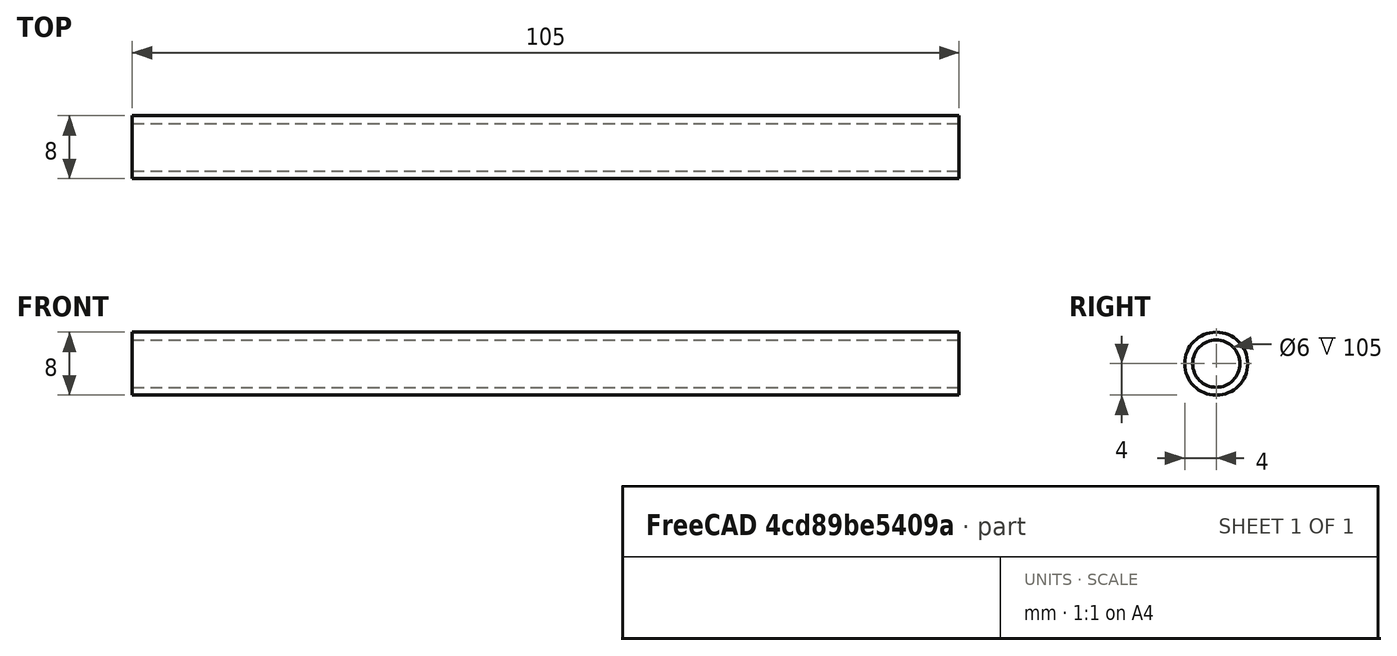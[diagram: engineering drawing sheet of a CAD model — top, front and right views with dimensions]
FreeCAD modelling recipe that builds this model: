
FCSTD DOCUMENT  (FreeCAD 0.19R24344 (Git))
Label: Inexpensive-Treadmill_Assembly
License: All rights reserved
LicenseURL: http://en.wikipedia.org/wiki/All_rights_reserved
objects: App::Link×22, App::DocumentObjectGroup×2, PartDesign::CoordinateSystem×1, App::FeaturePython×1, Part::FeaturePython×1, App::Part×1
note: 2 computed .brp shape members not serialized (recipe doc carries the construction recipe); baked Part::Feature solids carry a one-line shape summary decoded from their .brp
EXTERNAL_REF file=../../Miscellaneous/Baseplate/Baseplate.FCStd obj=Body
EXTERNAL_REF file=../../Miscellaneous/Baseplate/Baseplate.FCStd obj=LCS_Camera_Stand
EXTERNAL_REF file=../Stand_Camera-Case/Stand_Camera-Case.FCStd obj=LCS_Baseplate_Right
EXTERNAL_REF file=../Stand_Camera-Case/Stand_Camera-Case.FCStd obj=Body
EXTERNAL_REF file=../../Miscellaneous/PS-Eye/PS-Eye.FCStd obj=LCS_Camera_Base
EXTERNAL_REF file=../Stand_Camera-Case/Stand_Camera-Case.FCStd obj=LCS_Top_Mount
EXTERNAL_REF file=../../Miscellaneous/PS-Eye/PS-Eye.FCStd obj=Part
EXTERNAL_REF file=../../Miscellaneous/Baseplate/Baseplate.FCStd obj=LCS_Table_Foot1
EXTERNAL_REF file=../Stand_Treadmill_Sphere_Holder/Stand_Treadmill_Sphere_Holder.FCStd obj=LCS_Foot_Base
EXTERNAL_REF file=../Stand_Treadmill_Sphere_Holder/Stand_Treadmill_Sphere_Holder.FCStd obj=Body001
EXTERNAL_REF file=../Stand_Treadmill_Sphere_Holder/Stand_Treadmill_Sphere_Holder.FCStd obj=LCS_Base
EXTERNAL_REF file=../Stand_Treadmill_Sphere_Holder/Stand_Treadmill_Sphere_Holder.FCStd obj=LCS_Top001
EXTERNAL_REF file=../Stand_Treadmill_Sphere_Holder/Stand_Treadmill_Sphere_Holder.FCStd obj=Body
EXTERNAL_REF file=../Stand_Treadmill_Sphere_Holder/Stand_Treadmill_Sphere_Holder.FCStd obj=LCS_Top
EXTERNAL_REF file=../Treadmill_Sphere_Holder/Treadmill_Sphere_Holder.FCStd obj=LCS_Bottom
EXTERNAL_REF file=../Treadmill_Sphere_Holder/Treadmill_Sphere_Holder.FCStd obj=Treadmill_Sphere_Holder
EXTERNAL_REF file=../../Miscellaneous/Baseplate/Baseplate.FCStd obj=LCS_Foot2
EXTERNAL_REF file=../../Miscellaneous/Baseplate/Baseplate.FCStd obj=LCS_Foot3
EXTERNAL_REF file=../../Miscellaneous/Baseplate/Baseplate.FCStd obj=LCS_Foot4
EXTERNAL_REF file=../../Miscellaneous/Baseplate/Baseplate.FCStd obj=LCS_Light1
EXTERNAL_REF file=../Lamp_LED_5mm/Lamp_post_60.FCStd obj=LCS_Base
EXTERNAL_REF file=../Lamp_LED_5mm/Lamp_post_60.FCStd obj=LampPost
EXTERNAL_REF file=../../Miscellaneous/Baseplate/Baseplate.FCStd obj=LCS_Light3
EXTERNAL_REF file=../Lamp_LED_5mm/Lamp_post_40.FCStd obj=LCS_Base
EXTERNAL_REF file=../Lamp_LED_5mm/Lamp_post_40.FCStd obj=LampPost
EXTERNAL_REF file=../../Miscellaneous/Baseplate/Baseplate.FCStd obj=LCS_Light2
EXTERNAL_REF file=../Lamp_LED_5mm/Lamp_post.FCStd obj=LCS_Base
EXTERNAL_REF file=../Lamp_LED_5mm/Lamp_post.FCStd obj=LampPost
EXTERNAL_REF file=../Lamp_LED_5mm/Lamp_post_60.FCStd obj=LCS_Shade
EXTERNAL_REF file=../Lamp_LED_5mm/Lamp_shade.FCStd obj=LCS_Shade
EXTERNAL_REF file=../Lamp_LED_5mm/Lamp_shade.FCStd obj=Body
EXTERNAL_REF file=../Lamp_LED_5mm/Lamp_post_40.FCStd obj=LCS_Shade
EXTERNAL_REF file=../Lamp_LED_5mm/Lamp_post.FCStd obj=LCS_Shade
EXTERNAL_REF file=../../Miscellaneous/Baseplate/Baseplate.FCStd obj=LCS_Tablet001
EXTERNAL_REF file=../../Miscellaneous/Holder_Tablet/Holder_Tablet.FCStd obj=LCS_Base
EXTERNAL_REF file=../../Miscellaneous/Holder_Tablet/Holder_Tablet.FCStd obj=Body
EXTERNAL_REF file=../../Miscellaneous/Tablet/FireTablet.FCStd obj=LCS_Tablet_Back
EXTERNAL_REF file=../../Miscellaneous/Holder_Tablet/Holder_Tablet.FCStd obj=LCS_Tablet
EXTERNAL_REF file=../../Miscellaneous/Tablet/FireTablet.FCStd obj=Fire7
EXTERNAL_REF file=../../Miscellaneous/Baseplate/Baseplate.FCStd obj=LCS_Micro
EXTERNAL_REF file=../Stand_MicroManipulator/Stand_MicroManipulator.FCStd obj=LCS_Base
EXTERNAL_REF file=../Stand_MicroManipulator/Stand_MicroManipulator.FCStd obj=Body
EXTERNAL_REF file=../../Tethering/MicroManipulator/MicroManipulator_Assembly.FCStd obj=LCS_Origin
EXTERNAL_REF file=../Stand_MicroManipulator/Stand_MicroManipulator.FCStd obj=LCS_Top
EXTERNAL_REF file=../../Tethering/MicroManipulator/MicroManipulator_Assembly.FCStd obj=Model
EXTERNAL_REF file=../../Miscellaneous/Baseplate/Baseplate.FCStd obj=LCS_Heat
EXTERNAL_REF file=../../Miscellaneous/Baseplate/Heating-Base.FCStd obj=LCS_Base
EXTERNAL_REF file=../../Miscellaneous/Baseplate/Heating-Base.FCStd obj=Body
EXTERNAL_REF file=../../Miscellaneous/Spheres/Sphere-9mm-plain.FCStd obj=LCS_Sphere
EXTERNAL_REF file=../Treadmill_Sphere_Holder/Treadmill_Sphere_Holder.FCStd obj=LCS_Ball
EXTERNAL_REF file=../../Miscellaneous/Spheres/Sphere-9mm-plain.FCStd obj=Sphere001
EXTERNAL_REF file=../../Miscellaneous/Scale-Bar/Scale-Bar.FCStd obj=LCS_0
EXTERNAL_REF file=../../Miscellaneous/Scale-Bar/Scale-Bar.FCStd obj=Scalebar

FEATURE [App::DocumentObjectGroup] Parts
FEATURE [PartDesign::CoordinateSystem] LCS_Origin
  AttacherType = Attacher::AttachEngine3D
  MapMode = 2
  Support = -> [X_Axis]
FEATURE [App::DocumentObjectGroup] Constraints
FEATURE [App::FeaturePython] Variables  # WARN: FeaturePython — macro-defined, semantics opaque (R4)
FEATURE [App::Link] Baseplate_Baseplate
  LinkedObject = -> <external ../../Miscellaneous/Baseplate/Baseplate.FCStd>#Body
FEATURE [App::Link] Stand_Camera_Case_Stand_Camera
  AssemblyType = Asm4EE
  AttachedBy = #LCS_Baseplate_Right
  AttachedTo = Baseplate_Baseplate#LCS_Camera_Stand
  LinkPlacement = pos=(-80.3633,0.000175563,29) rot=(0,0,-1;1.57078rad)
  LinkedObject = -> <external ../Stand_Camera-Case/Stand_Camera-Case.FCStd>#Body
  Placement = pos=(-80.3633,0.000175563,29) rot=(0,0,-1;1.57078rad)
  expr: Placement = Baseplate_Baseplate.Placement * Baseplate#LCS_Camera_Stand.Placement * AttachmentOffset * Stand_Camera_Case#LCS_Baseplate_Right.Placement ^ -1
FEATURE [App::Link] PS_Eye_PSEye
  AssemblyType = Asm4EE
  AttachedBy = #LCS_Camera_Base
  AttachedTo = Stand_Camera_Case_Stand_Camera#LCS_Top_Mount
  AttachmentOffset = pos=(0,0,0) rot=(0,0,1;4.71239rad)
  LinkPlacement = pos=(-82.4061,2.32459,50) rot=(-0.577358,0.577346,0.577346;4.1888rad)
  LinkedObject = -> <external ../../Miscellaneous/PS-Eye/PS-Eye.FCStd>#Part
  Placement = pos=(-82.4061,2.32459,50) rot=(-0.577358,0.577346,0.577346;4.1888rad)
  expr: Placement = Stand_Camera_Case_Stand_Camera.Placement * Stand_Camera_Case#LCS_Top_Mount.Placement * AttachmentOffset * PS_Eye#LCS_Camera_Base.Placement ^ -1
FEATURE [App::Link] Stand_Treadmill_Sphere_Holder_Stand_Foot
  AssemblyType = Asm4EE
  AttachedBy = #LCS_Foot_Base
  AttachedTo = Baseplate_Baseplate#LCS_Table_Foot1
  AttachmentOffset = pos=(0,0,0) rot=(0,0,1;4.71239rad)
  LinkPlacement = pos=(38.0043,-0.0918805,46.2) rot=(0,0,1;3.14256rad)
  LinkedObject = -> <external ../Stand_Treadmill_Sphere_Holder/Stand_Treadmill_Sphere_Holder.FCStd>#Body001
  Placement = pos=(38.0043,-0.0918805,46.2) rot=(0,0,1;3.14256rad)
  expr: Placement = Baseplate_Baseplate.Placement * Baseplate#LCS_Table_Foot1.Placement * AttachmentOffset * Stand_Treadmill_Sphere_Holder#LCS_Foot_Base.Placement ^ -1
FEATURE [App::Link] Stand_Treadmill_Sphere_Holder_Stand
  AssemblyType = Asm4EE
  AttachedBy = #LCS_Base
  AttachedTo = Stand_Treadmill_Sphere_Holder_Stand_Foot#LCS_Top001
  AttachmentOffset = pos=(0,0,0) rot=(0,0,1;1.5708rad)
  LinkPlacement = pos=(38.0046,-0.0921835,43.2) rot=(0,0,1;4.71335rad)
  LinkedObject = -> <external ../Stand_Treadmill_Sphere_Holder/Stand_Treadmill_Sphere_Holder.FCStd>#Body
  Placement = pos=(38.0046,-0.0921835,43.2) rot=(0,0,1;4.71335rad)
  expr: Placement = Stand_Treadmill_Sphere_Holder_Stand_Foot.Placement * Stand_Treadmill_Sphere_Holder#LCS_Top001.Placement * AttachmentOffset * Stand_Treadmill_Sphere_Holder#LCS_Base.Placement ^ -1
FEATURE [App::Link] Treadmill_Sphere_Holder_Treadmill_Sphere_Holder
  AssemblyType = Asm4EE
  AttachedBy = #LCS_Bottom
  AttachedTo = Stand_Treadmill_Sphere_Holder_Stand#LCS_Top
  LinkPlacement = pos=(38.0046,-0.0921842,82.125) rot=(-1,-0.000479,-0.000479;4.71239rad)
  LinkedObject = -> <external ../Treadmill_Sphere_Holder/Treadmill_Sphere_Holder.FCStd>#Treadmill_Sphere_Holder
  Placement = pos=(38.0046,-0.0921842,82.125) rot=(-1,-0.000479,-0.000479;4.71239rad)
  expr: Placement = Stand_Treadmill_Sphere_Holder_Stand.Placement * Stand_Treadmill_Sphere_Holder#LCS_Top.Placement * AttachmentOffset * Treadmill_Sphere_Holder#LCS_Bottom.Placement ^ -1
FEATURE [App::Link] Stand_Treadmill_Sphere_Holder_Stand_Foot001
  AssemblyType = Asm4EE
  AttachedBy = #LCS_Foot_Base
  AttachedTo = Baseplate_Baseplate#LCS_Foot2
  AttachmentOffset = pos=(0,0,0) rot=(0,0,1;1.5708rad)
  LinkPlacement = pos=(38.0082,0.0956894,46.2) rot=(0,0,1;1.57177rad)
  LinkedObject = -> <external ../Stand_Treadmill_Sphere_Holder/Stand_Treadmill_Sphere_Holder.FCStd>#Body001
  Placement = pos=(38.0082,0.0956894,46.2) rot=(0,0,1;1.57177rad)
  expr: Placement = Baseplate_Baseplate.Placement * Baseplate#LCS_Foot2.Placement * AttachmentOffset * Stand_Treadmill_Sphere_Holder#LCS_Foot_Base.Placement ^ -1
FEATURE [App::Link] Stand_Treadmill_Sphere_Holder_Stand_Foot002
  AssemblyType = Asm4EE
  AttachedBy = #LCS_Foot_Base
  AttachedTo = Baseplate_Baseplate#LCS_Foot3
  LinkPlacement = pos=(38.1957,0.091848,46.2) rot=(0,0,1;0.00097rad)
  LinkedObject = -> <external ../Stand_Treadmill_Sphere_Holder/Stand_Treadmill_Sphere_Holder.FCStd>#Body001
  Placement = pos=(38.1957,0.091848,46.2) rot=(0,0,1;0.00097rad)
  expr: Placement = Baseplate_Baseplate.Placement * Baseplate#LCS_Foot3.Placement * AttachmentOffset * Stand_Treadmill_Sphere_Holder#LCS_Foot_Base.Placement ^ -1
FEATURE [App::Link] Stand_Treadmill_Sphere_Holder_Stand_Foot003
  AssemblyType = Asm4EE
  AttachedBy = #LCS_Foot_Base
  AttachedTo = Baseplate_Baseplate#LCS_Foot4
  AttachmentOffset = pos=(0,0,0) rot=(0,0,1;4.71239rad)
  LinkPlacement = pos=(38.1918,-0.0956894,46.2) rot=(0,0,1;4.71336rad)
  LinkedObject = -> <external ../Stand_Treadmill_Sphere_Holder/Stand_Treadmill_Sphere_Holder.FCStd>#Body001
  Placement = pos=(38.1918,-0.0956894,46.2) rot=(0,0,1;4.71336rad)
  expr: Placement = Baseplate_Baseplate.Placement * Baseplate#LCS_Foot4.Placement * AttachmentOffset * Stand_Treadmill_Sphere_Holder#LCS_Foot_Base.Placement ^ -1
FEATURE [App::Link] Lamp_post_lamp_post_60
  AssemblyType = Asm4EE
  AttachedBy = #LCS_Base
  AttachedTo = Baseplate_Baseplate#LCS_Light1
  AttachmentOffset = pos=(0,0,0) rot=(0,0,1;0.349066rad)
  LinkPlacement = pos=(-41.0097,-26.459,10) rot=(0,0,1;1.91986rad)
  LinkedObject = -> <external ../Lamp_LED_5mm/Lamp_post_60.FCStd>#LampPost
  Placement = pos=(-41.0097,-26.459,10) rot=(0,0,1;1.91986rad)
  expr: Placement = Baseplate_Baseplate.Placement * Baseplate#LCS_Light1.Placement * AttachmentOffset * Lamp_post_60#LCS_Base.Placement ^ -1
FEATURE [App::Link] Lamp_post_40_lamp_post_40
  AssemblyType = Asm4EE
  AttachedBy = #LCS_Base
  AttachedTo = Baseplate_Baseplate#LCS_Light3
  AttachmentOffset = pos=(0,0,0) rot=(0,0,1;5.44543rad)
  LinkPlacement = pos=(-14.7719,53.1011,10) rot=(0,0,-1;5.55015rad)
  LinkedObject = -> <external ../Lamp_LED_5mm/Lamp_post_40.FCStd>#LampPost
  Placement = pos=(-14.7719,53.1011,10) rot=(0,0,-1;5.55015rad)
  expr: Placement = Baseplate_Baseplate.Placement * Baseplate#LCS_Light3.Placement * AttachmentOffset * Lamp_post_40#LCS_Base.Placement ^ -1
FEATURE [App::Link] Lamp_post_lamp_post
  AssemblyType = Asm4EE
  AttachedBy = #LCS_Base
  AttachedTo = Baseplate_Baseplate#LCS_Light2
  AttachmentOffset = pos=(0,0,0) rot=(0,0,1;-0.349066rad)
  LinkPlacement = pos=(-41.0097,26.459,10) rot=(0,0,-1;5.06145rad)
  LinkedObject = -> <external ../Lamp_LED_5mm/Lamp_post.FCStd>#LampPost
  Placement = pos=(-41.0097,26.459,10) rot=(0,0,-1;5.06145rad)
  expr: Placement = Baseplate_Baseplate.Placement * Baseplate#LCS_Light2.Placement * AttachmentOffset * Lamp_post#LCS_Base.Placement ^ -1
FEATURE [App::Link] Lamp_shade_lamp_shade
  AssemblyType = Asm4EE
  AttachedBy = #LCS_Shade
  AttachedTo = Lamp_post_lamp_post_60#LCS_Shade
  AttachmentOffset = pos=(0,0,0) rot=(0.707107,-0.707107,0;3.14159rad)
  LinkPlacement = pos=(-33.7179,-23.805,70.5) rot=(0.443713,0.633687,0.633687;2.30637rad)
  LinkedObject = -> <external ../Lamp_LED_5mm/Lamp_shade.FCStd>#Body
  Placement = pos=(-33.7179,-23.805,70.5) rot=(0.443713,0.633687,0.633687;2.30637rad)
  expr: Placement = Lamp_post_lamp_post_60.Placement * Lamp_post_60#LCS_Shade.Placement * AttachmentOffset * Lamp_shade#LCS_Shade.Placement ^ -1
FEATURE [App::Link] Lamp_shade_lamp_shade001
  AssemblyType = Asm4EE
  AttachedBy = #LCS_Shade
  AttachedTo = Lamp_post_40_lamp_post_40#LCS_Shade
  AttachmentOffset = pos=(0,0,0) rot=(0,0,1;2.32129rad)
  LinkPlacement = pos=(-9.4181,47.1551,52.8953) rot=(0.819087,0.314418,0.47983;1.34948rad)
  LinkedObject = -> <external ../Lamp_LED_5mm/Lamp_shade.FCStd>#Body
  Placement = pos=(-9.4181,47.1551,52.8953) rot=(0.819087,0.314418,0.47983;1.34948rad)
  expr: Placement = Lamp_post_40_lamp_post_40.Placement * Lamp_post_40#LCS_Shade.Placement * AttachmentOffset * Lamp_shade#LCS_Shade.Placement ^ -1
FEATURE [App::Link] Lamp_shade_lamp_shade002
  AssemblyType = Asm4EE
  AttachedBy = #LCS_Shade
  AttachedTo = Lamp_post_lamp_post#LCS_Shade
  AttachmentOffset = pos=(0,0,0) rot=(0,0,1;2.9147rad)
  LinkPlacement = pos=(-33.1668,23.6045,89.1503) rot=(0.745251,0.52183,0.415083;2.07138rad)
  LinkedObject = -> <external ../Lamp_LED_5mm/Lamp_shade.FCStd>#Body
  Placement = pos=(-33.1668,23.6045,89.1503) rot=(0.745251,0.52183,0.415083;2.07138rad)
  expr: Placement = Lamp_post_lamp_post.Placement * Lamp_post#LCS_Shade.Placement * AttachmentOffset * Lamp_shade#LCS_Shade.Placement ^ -1
FEATURE [App::Link] Holder_Tablet_FireHolder
  AssemblyType = Asm4EE
  AttachedBy = #LCS_Base
  AttachedTo = Baseplate_Baseplate#LCS_Tablet001
  AttachmentOffset = pos=(-12.7,40,0) rot=(0,0,1;4.71239rad)
  LinkPlacement = pos=(85.5,50,37) rot=(0,0,1;0rad)
  LinkedObject = -> <external ../../Miscellaneous/Holder_Tablet/Holder_Tablet.FCStd>#Body
  Placement = pos=(85.5,50,37) rot=(0,0,1;0rad)
  expr: Placement = Baseplate_Baseplate.Placement * Baseplate#LCS_Tablet001.Placement * AttachmentOffset * Holder_Tablet#LCS_Base.Placement ^ -1
FEATURE [App::Link] FireTablet_Fire7
  AssemblyType = Asm4EE
  AttachedBy = #LCS_Tablet_Back
  AttachedTo = Holder_Tablet_FireHolder#LCS_Tablet
  AttachmentOffset = pos=(12.7,-5,0) rot=(0.707107,0.707107,0;3.14159rad)
  LinkPlacement = pos=(78.5,12.7,89.518) rot=(0.57735,-0.57735,-0.57735;2.0944rad)
  LinkedObject = -> <external ../../Miscellaneous/Tablet/FireTablet.FCStd>#Fire7
  Placement = pos=(78.5,12.7,89.518) rot=(0.57735,-0.57735,-0.57735;2.0944rad)
  expr: Placement = Holder_Tablet_FireHolder.Placement * Holder_Tablet#LCS_Tablet.Placement * AttachmentOffset * FireTablet#LCS_Tablet_Back.Placement ^ -1
FEATURE [App::Link] Stand_MicroManipulator_Stand
  AssemblyType = Asm4EE
  AttachedBy = #LCS_Base
  AttachedTo = Baseplate_Baseplate#LCS_Micro
  AttachmentOffset = pos=(25.4,0,0) rot=(0,0,1;3.14159rad)
  LinkPlacement = pos=(-2.66e-14,-63.5,8) rot=(0,0,1;3.14159rad)
  LinkedObject = -> <external ../Stand_MicroManipulator/Stand_MicroManipulator.FCStd>#Body
  Placement = pos=(-2.66e-14,-63.5,8) rot=(0,0,1;3.14159rad)
  expr: Placement = Baseplate_Baseplate.Placement * Baseplate#LCS_Micro.Placement * AttachmentOffset * Stand_MicroManipulator#LCS_Base.Placement ^ -1
FEATURE [App::Link] MicroManipulator_Assembly
  AssemblyType = Asm4EE
  AttachedBy = #LCS_Origin
  AttachedTo = Stand_MicroManipulator_Stand#LCS_Top
  AttachmentOffset = pos=(0,0,0) rot=(0,0,1;3.14159rad)
  LinkPlacement = pos=(12.7,-50.8,58) rot=(0,0,-1;4.71239rad)
  LinkedObject = -> <external ../../Tethering/MicroManipulator/MicroManipulator_Assembly.FCStd>#Model
  Placement = pos=(12.7,-50.8,58) rot=(0,0,-1;4.71239rad)
  expr: Placement = Stand_MicroManipulator_Stand.Placement * Stand_MicroManipulator#LCS_Top.Placement * AttachmentOffset * MicroManipulator_Assembly#LCS_Origin.Placement ^ -1
FEATURE [App::Link] Heating_Base_Heat_pad
  AssemblyType = Asm4EE
  AttachedBy = #LCS_Base
  AttachedTo = Baseplate_Baseplate#LCS_Heat
  LinkPlacement = pos=(38.1,7.1e-15,33) rot=(0,0,1;1.5708rad)
  LinkedObject = -> <external ../../Miscellaneous/Baseplate/Heating-Base.FCStd>#Body
  Placement = pos=(38.1,7.1e-15,33) rot=(0,0,1;1.5708rad)
  expr: Placement = Baseplate_Baseplate.Placement * Baseplate#LCS_Heat.Placement * AttachmentOffset * Heating_Base#LCS_Base.Placement ^ -1
FEATURE [App::Link] Sphere_9mm_plain_Sphere001
  AssemblyType = Asm4EE
  AttachedBy = #LCS_Sphere
  AttachedTo = Treadmill_Sphere_Holder_Treadmill_Sphere_Holder#LCS_Ball
  LinkPlacement = pos=(38.0046,-0.0921842,82.1448) rot=(0,0,-1;3.14063rad)
  LinkedObject = -> <external ../../Miscellaneous/Spheres/Sphere-9mm-plain.FCStd>#Sphere001
  Placement = pos=(38.0046,-0.0921842,82.1448) rot=(0,0,-1;3.14063rad)
  expr: Placement = Treadmill_Sphere_Holder_Treadmill_Sphere_Holder.Placement * Treadmill_Sphere_Holder#LCS_Ball.Placement * AttachmentOffset * Sphere_9mm_plain#LCS_Sphere.Placement ^ -1
FEATURE [Part::FeaturePython] Tube  # WARN: FeaturePython — macro-defined, semantics opaque (R4)
  AttacherType = Attacher::AttachEngine3D
  Height = 105
  InnerRadius = 3
  OuterRadius = 4
  Placement = pos=(-67,-1,54) rot=(0,1,0;1.5708rad)
FEATURE [App::Link] Scale_Bar_Scalebar
  AssemblyType = Asm4EE
  AttachedBy = #LCS_0
  AttachedTo = Parent Assembly#LCS_Origin
  AttachmentOffset = pos=(-55,-185,0) rot=(-0.57735,0.57735,0.57735;4.18879rad)
  LinkPlacement = pos=(-55,-185,0) rot=(-0.57735,0.57735,0.57735;4.18879rad)
  LinkedObject = -> <external ../../Miscellaneous/Scale-Bar/Scale-Bar.FCStd>#Scalebar
  Placement = pos=(-55,-185,0) rot=(-0.57735,0.57735,0.57735;4.18879rad)
  expr: Placement = LCS_Origin.Placement * AttachmentOffset * Scale_Bar#LCS_0.Placement ^ -1
FEATURE [App::Part] Model
  Configuration = 0
  Group = -> [LCS_Origin,Constraints,Variables,Baseplate_Baseplate,Stand_Camera_Case_Stand_Camera,PS_Eye_PSEye,Stand_Treadmill_Sphere_Holder_Stand_Foot,Stand_Treadmill_Sphere_Holder_Stand,Treadmill_Sphere_Holder_Treadmill_Sphere_Holder,Stand_Treadmill_Sphere_Holder_Stand_Foot001,Stand_Treadmill_Sphere_Holder_Stand_Foot002,Stand_Treadmill_Sphere_Holder_Stand_Foot003,Lamp_post_lamp_post_60,+12 more]
  Origin = -> Origin
  Type = Assembly4 Model

RESOLVED EXTERNAL PARTS (link-assembly join: the EXTERNAL_REF files above that resolve inside this repo's crawl, each included once):
---- part ../../Miscellaneous/Baseplate/Baseplate.FCStd = doc fcstd_f7cd438ebf0e ----
FCSTD DOCUMENT  (FreeCAD 0.19R24344 (Git))
Label: Baseplate
License: All rights reserved
LicenseURL: http://en.wikipedia.org/wiki/All_rights_reserved
objects: PartDesign::CoordinateSystem×13, Sketcher::SketchObject×1, PartDesign::Pad×1, PartDesign::Body×1
note: 17 computed .brp shape members not serialized (recipe doc carries the construction recipe); baked Part::Feature solids carry a one-line shape summary decoded from their .brp

FEATURE [Sketcher::SketchObject] Sketch
  FullyConstrained = true
  MapMode = 5
  Support = -> [XY_Plane]
  sketch-geometry (140):
    g0: LineSegment StartX=-139.7 StartY=139.7 StartZ=0 EndX=139.7 EndY=139.7 EndZ=0
    g1: LineSegment StartX=152.4 StartY=127 StartZ=0 EndX=152.4 EndY=-127 EndZ=0
    g2: LineSegment StartX=139.7 StartY=-139.7 StartZ=0 EndX=-139.7 EndY=-139.7 EndZ=0
    g3: LineSegment StartX=-152.4 StartY=-127 StartZ=0 EndX=-152.4 EndY=127 EndZ=0
    g4: ArcOfCircle CenterX=-139.7 CenterY=127 CenterZ=0 NormalX=0 NormalY=0 NormalZ=1 AngleXU=0 Radius=12.7 StartAngle=1.5708 EndAngle=3.14159
    g5: ArcOfCircle CenterX=-139.7 CenterY=-127 CenterZ=0 NormalX=0 NormalY=0 NormalZ=1 AngleXU=0 Radius=12.7 StartAngle=3.14159 EndAngle=4.71239
    g6: ArcOfCircle CenterX=139.7 CenterY=-127 CenterZ=0 NormalX=0 NormalY=0 NormalZ=1 AngleXU=0 Radius=12.7 StartAngle=4.71239 EndAngle=6.28319
    g7: ArcOfCircle CenterX=139.7 CenterY=127 CenterZ=0 NormalX=0 NormalY=0 NormalZ=1 AngleXU=0 Radius=12.7 StartAngle=2e-16 EndAngle=1.5708
    g8: Circle CenterX=-139.7 CenterY=127 CenterZ=0 NormalX=0 NormalY=0 NormalZ=1 AngleXU=0 Radius=3.175
    g9: Circle CenterX=-114.3 CenterY=127 CenterZ=0 NormalX=0 NormalY=0 NormalZ=1 AngleXU=0 Radius=3.175
    g10: Circle CenterX=-88.9 CenterY=127 CenterZ=0 NormalX=0 NormalY=0 NormalZ=1 AngleXU=0 Radius=3.175
    g11: Circle CenterX=-63.5 CenterY=127 CenterZ=0 NormalX=0 NormalY=0 NormalZ=1 AngleXU=0 Radius=3.175
    g12: Circle CenterX=-38.1 CenterY=127 CenterZ=0 NormalX=0 NormalY=0 NormalZ=1 AngleXU=0 Radius=3.175
    g13: Circle CenterX=-12.7 CenterY=127 CenterZ=0 NormalX=0 NormalY=0 NormalZ=1 AngleXU=0 Radius=3.175
    g14: Circle CenterX=12.7 CenterY=127 CenterZ=0 NormalX=0 NormalY=0 NormalZ=1 AngleXU=0 Radius=3.175
    g15: Circle CenterX=38.1 CenterY=127 CenterZ=0 NormalX=0 NormalY=0 NormalZ=1 AngleXU=0 Radius=3.175
    g16: Circle CenterX=63.5 CenterY=127 CenterZ=0 NormalX=0 NormalY=0 NormalZ=1 AngleXU=0 Radius=3.175
    g17: Circle CenterX=88.9 CenterY=127 CenterZ=0 NormalX=0 NormalY=0 NormalZ=1 AngleXU=0 Radius=3.175
    g18: Circle CenterX=114.3 CenterY=127 CenterZ=0 NormalX=0 NormalY=0 NormalZ=1 AngleXU=0 Radius=3.175
    g19: Circle CenterX=139.7 CenterY=127 CenterZ=0 NormalX=0 NormalY=0 NormalZ=1 AngleXU=0 Radius=3.175
    g20: Circle CenterX=-139.7 CenterY=101.6 CenterZ=0 NormalX=0 NormalY=0 NormalZ=1 AngleXU=0 Radius=3.175
    g21: Circle CenterX=-114.3 CenterY=101.6 CenterZ=0 NormalX=0 NormalY=0 NormalZ=1 AngleXU=0 Radius=3.175
    g22: Circle CenterX=-88.9 CenterY=101.6 CenterZ=0 NormalX=0 NormalY=0 NormalZ=1 AngleXU=0 Radius=3.175
    g23: Circle CenterX=-63.5 CenterY=101.6 CenterZ=0 NormalX=0 NormalY=0 NormalZ=1 AngleXU=0 Radius=3.175
    g24: Circle CenterX=-38.1 CenterY=101.6 CenterZ=0 NormalX=0 NormalY=0 NormalZ=1 AngleXU=0 Radius=3.175
    g25: Circle CenterX=-12.7 CenterY=101.6 CenterZ=0 NormalX=0 NormalY=0 NormalZ=1 AngleXU=0 Radius=3.175
    g26: Circle CenterX=12.7 CenterY=101.6 CenterZ=0 NormalX=0 NormalY=0 NormalZ=1 AngleXU=0 Radius=3.175
    g27: Circle CenterX=38.1 CenterY=101.6 CenterZ=0 NormalX=0 NormalY=0 NormalZ=1 AngleXU=0 Radius=3.175
    g28: Circle CenterX=63.5 CenterY=101.6 CenterZ=0 NormalX=0 NormalY=0 NormalZ=1 AngleXU=0 Radius=3.175
    g29: Circle CenterX=88.9 CenterY=101.6 CenterZ=0 NormalX=0 NormalY=0 NormalZ=1 AngleXU=0 Radius=3.175
    g30: Circle CenterX=114.3 CenterY=101.6 CenterZ=0 NormalX=0 NormalY=0 NormalZ=1 AngleXU=0 Radius=3.175
    g31: Circle CenterX=139.7 CenterY=101.6 CenterZ=0 NormalX=0 NormalY=0 NormalZ=1 AngleXU=0 Radius=3.175
    g32: Circle CenterX=-139.7 CenterY=76.2 CenterZ=0 NormalX=0 NormalY=0 NormalZ=1 AngleXU=0 Radius=3.175
    g33: Circle CenterX=-114.3 CenterY=76.2 CenterZ=0 NormalX=0 NormalY=0 NormalZ=1 AngleXU=0 Radius=3.175
    g34: Circle CenterX=-88.9 CenterY=76.2 CenterZ=0 NormalX=0 NormalY=0 NormalZ=1 AngleXU=0 Radius=3.175
    g35: Circle CenterX=-63.5 CenterY=76.2 CenterZ=0 NormalX=0 NormalY=0 NormalZ=1 AngleXU=0 Radius=3.175
    g36: Circle CenterX=-38.1 CenterY=76.2 CenterZ=0 NormalX=0 NormalY=0 NormalZ=1 AngleXU=0 Radius=3.175
    g37: Circle CenterX=-12.7 CenterY=76.2 CenterZ=0 NormalX=0 NormalY=0 NormalZ=1 AngleXU=0 Radius=3.175
    g38: Circle CenterX=12.7 CenterY=76.2 CenterZ=0 NormalX=0 NormalY=0 NormalZ=1 AngleXU=0 Radius=3.175
    g39: Circle CenterX=38.1 CenterY=76.2 CenterZ=0 NormalX=0 NormalY=0 NormalZ=1 AngleXU=0 Radius=3.175
    g40: Circle CenterX=63.5 CenterY=76.2 CenterZ=0 NormalX=0 NormalY=0 NormalZ=1 AngleXU=0 Radius=3.175
    g41: Circle CenterX=88.9 CenterY=76.2 CenterZ=0 NormalX=0 NormalY=0 NormalZ=1 AngleXU=0 Radius=3.175
    g42: Circle CenterX=114.3 CenterY=76.2 CenterZ=0 NormalX=0 NormalY=0 NormalZ=1 AngleXU=0 Radius=3.175
    g43: Circle CenterX=139.7 CenterY=76.2 CenterZ=0 NormalX=0 NormalY=0 NormalZ=1 AngleXU=0 Radius=3.175
    g44: Circle CenterX=-139.7 CenterY=50.8 CenterZ=0 NormalX=0 NormalY=0 NormalZ=1 AngleXU=0 Radius=3.175
    g45: Circle CenterX=-114.3 CenterY=50.8 CenterZ=0 NormalX=0 NormalY=0 NormalZ=1 AngleXU=0 Radius=3.175
    g46: Circle CenterX=-88.9 CenterY=50.8 CenterZ=0 NormalX=0 NormalY=0 NormalZ=1 AngleXU=0 Radius=3.175
    g47: Circle CenterX=-63.5 CenterY=50.8 CenterZ=0 NormalX=0 NormalY=0 NormalZ=1 AngleXU=0 Radius=3.175
    g48: Circle CenterX=-38.1 CenterY=50.8 CenterZ=0 NormalX=0 NormalY=0 NormalZ=1 AngleXU=0 Radius=3.175
    g49: Circle CenterX=-12.7 CenterY=50.8 CenterZ=0 NormalX=0 NormalY=0 NormalZ=1 AngleXU=0 Radius=3.175
    g50: Circle CenterX=12.7 CenterY=50.8 CenterZ=0 NormalX=0 NormalY=0 NormalZ=1 AngleXU=0 Radius=3.175
    g51: Circle CenterX=38.1 CenterY=50.8 CenterZ=0 NormalX=0 NormalY=0 NormalZ=1 AngleXU=0 Radius=3.175
    g52: Circle CenterX=63.5 CenterY=50.8 CenterZ=0 NormalX=0 NormalY=0 NormalZ=1 AngleXU=0 Radius=3.175
    g53: Circle CenterX=88.9 CenterY=50.8 CenterZ=0 NormalX=0 NormalY=0 NormalZ=1 AngleXU=0 Radius=3.175
    g54: Circle CenterX=114.3 CenterY=50.8 CenterZ=0 NormalX=0 NormalY=0 NormalZ=1 AngleXU=0 Radius=3.175
    g55: Circle CenterX=139.7 CenterY=50.8 CenterZ=0 NormalX=0 NormalY=0 NormalZ=1 AngleXU=0 Radius=3.175
    g56: Circle CenterX=-139.7 CenterY=25.4 CenterZ=0 NormalX=0 NormalY=0 NormalZ=1 AngleXU=0 Radius=3.175
    g57: Circle CenterX=-114.3 CenterY=25.4 CenterZ=0 NormalX=0 NormalY=0 NormalZ=1 AngleXU=0 Radius=3.175
    g58: Circle CenterX=-88.9 CenterY=25.4 CenterZ=0 NormalX=0 NormalY=0 NormalZ=1 AngleXU=0 Radius=3.175
    g59: Circle CenterX=-63.5 CenterY=25.4 CenterZ=0 NormalX=0 NormalY=0 NormalZ=1 AngleXU=0 Radius=3.175
    g60: Circle CenterX=-38.1 CenterY=25.4 CenterZ=0 NormalX=0 NormalY=0 NormalZ=1 AngleXU=0 Radius=3.175
    g61: Circle CenterX=-12.7 CenterY=25.4 CenterZ=0 NormalX=0 NormalY=0 NormalZ=1 AngleXU=0 Radius=3.175
    g62: Circle CenterX=12.7 CenterY=25.4 CenterZ=0 NormalX=0 NormalY=0 NormalZ=1 AngleXU=0 Radius=3.175
    g63: Circle CenterX=38.1 CenterY=25.4 CenterZ=0 NormalX=0 NormalY=0 NormalZ=1 AngleXU=0 Radius=3.175
    g64: Circle CenterX=63.5 CenterY=25.4 CenterZ=0 NormalX=0 NormalY=0 NormalZ=1 AngleXU=0 Radius=3.175
    g65: Circle CenterX=88.9 CenterY=25.4 CenterZ=0 NormalX=0 NormalY=0 NormalZ=1 AngleXU=0 Radius=3.175
    g66: Circle CenterX=114.3 CenterY=25.4 CenterZ=0 NormalX=0 NormalY=0 NormalZ=1 AngleXU=0 Radius=3.175
    g67: Circle CenterX=139.7 CenterY=25.4 CenterZ=0 NormalX=0 NormalY=0 NormalZ=1 AngleXU=0 Radius=3.175
    g68: Circle CenterX=-139.7 CenterY=8e-15 CenterZ=0 NormalX=0 NormalY=0 NormalZ=1 AngleXU=0 Radius=3.175
    g69: Circle CenterX=-114.3 CenterY=8e-15 CenterZ=0 NormalX=0 NormalY=0 NormalZ=1 AngleXU=0 Radius=3.175
    g70: Circle CenterX=-88.9 CenterY=8e-15 CenterZ=0 NormalX=0 NormalY=0 NormalZ=1 AngleXU=0 Radius=3.175
    g71: Circle CenterX=-63.5 CenterY=8e-15 CenterZ=0 NormalX=0 NormalY=0 NormalZ=1 AngleXU=0 Radius=3.175
    g72: Circle CenterX=-38.1 CenterY=8e-15 CenterZ=0 NormalX=0 NormalY=0 NormalZ=1 AngleXU=0 Radius=3.175
    g73: Circle CenterX=-12.7 CenterY=8e-15 CenterZ=0 NormalX=0 NormalY=0 NormalZ=1 AngleXU=0 Radius=3.175
    g74: Circle CenterX=12.7 CenterY=8e-15 CenterZ=0 NormalX=0 NormalY=0 NormalZ=1 AngleXU=0 Radius=3.175
    g75: Circle CenterX=38.1 CenterY=8e-15 CenterZ=0 NormalX=0 NormalY=0 NormalZ=1 AngleXU=0 Radius=3.175
    g76: Circle CenterX=63.5 CenterY=8e-15 CenterZ=0 NormalX=0 NormalY=0 NormalZ=1 AngleXU=0 Radius=3.175
    g77: Circle CenterX=88.9 CenterY=8e-15 CenterZ=0 NormalX=0 NormalY=0 NormalZ=1 AngleXU=0 Radius=3.175
    g78: Circle CenterX=114.3 CenterY=8e-15 CenterZ=0 NormalX=0 NormalY=0 NormalZ=1 AngleXU=0 Radius=3.175
    g79: Circle CenterX=139.7 CenterY=8e-15 CenterZ=0 NormalX=0 NormalY=0 NormalZ=1 AngleXU=0 Radius=3.175
    g80: Circle CenterX=-139.7 CenterY=-25.4 CenterZ=0 NormalX=0 NormalY=0 NormalZ=1 AngleXU=0 Radius=3.175
    g81: Circle CenterX=-114.3 CenterY=-25.4 CenterZ=0 NormalX=0 NormalY=0 NormalZ=1 AngleXU=0 Radius=3.175
    g82: Circle CenterX=-88.9 CenterY=-25.4 CenterZ=0 NormalX=0 NormalY=0 NormalZ=1 AngleXU=0 Radius=3.175
    g83: Circle CenterX=-63.5 CenterY=-25.4 CenterZ=0 NormalX=0 NormalY=0 NormalZ=1 AngleXU=0 Radius=3.175
    g84: Circle CenterX=-38.1 CenterY=-25.4 CenterZ=0 NormalX=0 NormalY=0 NormalZ=1 AngleXU=0 Radius=3.175
    g85: Circle CenterX=-12.7 CenterY=-25.4 CenterZ=0 NormalX=0 NormalY=0 NormalZ=1 AngleXU=0 Radius=3.175
    g86: Circle CenterX=12.7 CenterY=-25.4 CenterZ=0 NormalX=0 NormalY=0 NormalZ=1 AngleXU=0 Radius=3.175
    g87: Circle CenterX=38.1 CenterY=-25.4 CenterZ=0 NormalX=0 NormalY=0 NormalZ=1 AngleXU=0 Radius=3.175
    g88: Circle CenterX=63.5 CenterY=-25.4 CenterZ=0 NormalX=0 NormalY=0 NormalZ=1 AngleXU=0 Radius=3.175
    g89: Circle CenterX=88.9 CenterY=-25.4 CenterZ=0 NormalX=0 NormalY=0 NormalZ=1 AngleXU=0 Radius=3.175
    g90: Circle CenterX=114.3 CenterY=-25.4 CenterZ=0 NormalX=0 NormalY=0 NormalZ=1 AngleXU=0 Radius=3.175
    g91: Circle CenterX=139.7 CenterY=-25.4 CenterZ=0 NormalX=0 NormalY=0 NormalZ=1 AngleXU=0 Radius=3.175
    g92: Circle CenterX=-139.7 CenterY=-50.8 CenterZ=0 NormalX=0 NormalY=0 NormalZ=1 AngleXU=0 Radius=3.175
    g93: Circle CenterX=-114.3 CenterY=-50.8 CenterZ=0 NormalX=0 NormalY=0 NormalZ=1 AngleXU=0 Radius=3.175
    g94: Circle CenterX=-88.9 CenterY=-50.8 CenterZ=0 NormalX=0 NormalY=0 NormalZ=1 AngleXU=0 Radius=3.175
    g95: Circle CenterX=-63.5 CenterY=-50.8 CenterZ=0 NormalX=0 NormalY=0 NormalZ=1 AngleXU=0 Radius=3.175
    g96: Circle CenterX=-38.1 CenterY=-50.8 CenterZ=0 NormalX=0 NormalY=0 NormalZ=1 AngleXU=0 Radius=3.175
    g97: Circle CenterX=-12.7 CenterY=-50.8 CenterZ=0 NormalX=0 NormalY=0 NormalZ=1 AngleXU=0 Radius=3.175
    g98: Circle CenterX=12.7 CenterY=-50.8 CenterZ=0 NormalX=0 NormalY=0 NormalZ=1 AngleXU=0 Radius=3.175
    g99: Circle CenterX=38.1 CenterY=-50.8 CenterZ=0 NormalX=0 NormalY=0 NormalZ=1 AngleXU=0 Radius=3.175
    g100: Circle CenterX=63.5 CenterY=-50.8 CenterZ=0 NormalX=0 NormalY=0 NormalZ=1 AngleXU=0 Radius=3.175
    g101: Circle CenterX=88.9 CenterY=-50.8 CenterZ=0 NormalX=0 NormalY=0 NormalZ=1 AngleXU=0 Radius=3.175
    g102: Circle CenterX=114.3 CenterY=-50.8 CenterZ=0 NormalX=0 NormalY=0 NormalZ=1 AngleXU=0 Radius=3.175
    g103: Circle CenterX=139.7 CenterY=-50.8 CenterZ=0 NormalX=0 NormalY=0 NormalZ=1 AngleXU=0 Radius=3.175
    g104: Circle CenterX=-139.7 CenterY=-76.2 CenterZ=0 NormalX=0 NormalY=0 NormalZ=1 AngleXU=0 Radius=3.175
    g105: Circle CenterX=-114.3 CenterY=-76.2 CenterZ=0 NormalX=0 NormalY=0 NormalZ=1 AngleXU=0 Radius=3.175
    g106: Circle CenterX=-88.9 CenterY=-76.2 CenterZ=0 NormalX=0 NormalY=0 NormalZ=1 AngleXU=0 Radius=3.175
    g107: Circle CenterX=-63.5 CenterY=-76.2 CenterZ=0 NormalX=0 NormalY=0 NormalZ=1 AngleXU=0 Radius=3.175
    g108: Circle CenterX=-38.1 CenterY=-76.2 CenterZ=0 NormalX=0 NormalY=0 NormalZ=1 AngleXU=0 Radius=3.175
    g109: Circle CenterX=-12.7 CenterY=-76.2 CenterZ=0 NormalX=0 NormalY=0 NormalZ=1 AngleXU=0 Radius=3.175
    g110: Circle CenterX=12.7 CenterY=-76.2 CenterZ=0 NormalX=0 NormalY=0 NormalZ=1 AngleXU=0 Radius=3.175
    g111: Circle CenterX=38.1 CenterY=-76.2 CenterZ=0 NormalX=0 NormalY=0 NormalZ=1 AngleXU=0 Radius=3.175
    g112: Circle CenterX=63.5 CenterY=-76.2 CenterZ=0 NormalX=0 NormalY=0 NormalZ=1 AngleXU=0 Radius=3.175
    g113: Circle CenterX=88.9 CenterY=-76.2 CenterZ=0 NormalX=0 NormalY=0 NormalZ=1 AngleXU=0 Radius=3.175
    g114: Circle CenterX=114.3 CenterY=-76.2 CenterZ=0 NormalX=0 NormalY=0 NormalZ=1 AngleXU=0 Radius=3.175
    g115: Circle CenterX=139.7 CenterY=-76.2 CenterZ=0 NormalX=0 NormalY=0 NormalZ=1 AngleXU=0 Radius=3.175
    g116: Circle CenterX=-139.7 CenterY=-101.6 CenterZ=0 NormalX=0 NormalY=0 NormalZ=1 AngleXU=0 Radius=3.175
    g117: Circle CenterX=-114.3 CenterY=-101.6 CenterZ=0 NormalX=0 NormalY=0 NormalZ=1 AngleXU=0 Radius=3.175
    g118: Circle CenterX=-88.9 CenterY=-101.6 CenterZ=0 NormalX=0 NormalY=0 NormalZ=1 AngleXU=0 Radius=3.175
    g119: Circle CenterX=-63.5 CenterY=-101.6 CenterZ=0 NormalX=0 NormalY=0 NormalZ=1 AngleXU=0 Radius=3.175
    g120: Circle CenterX=-38.1 CenterY=-101.6 CenterZ=0 NormalX=0 NormalY=0 NormalZ=1 AngleXU=0 Radius=3.175
    g121: Circle CenterX=-12.7 CenterY=-101.6 CenterZ=0 NormalX=0 NormalY=0 NormalZ=1 AngleXU=0 Radius=3.175
    g122: Circle CenterX=12.7 CenterY=-101.6 CenterZ=0 NormalX=0 NormalY=0 NormalZ=1 AngleXU=0 Radius=3.175
    g123: Circle CenterX=38.1 CenterY=-101.6 CenterZ=0 NormalX=0 NormalY=0 NormalZ=1 AngleXU=0 Radius=3.175
    g124: Circle CenterX=63.5 CenterY=-101.6 CenterZ=0 NormalX=0 NormalY=0 NormalZ=1 AngleXU=0 Radius=3.175
    g125: Circle CenterX=88.9 CenterY=-101.6 CenterZ=0 NormalX=0 NormalY=0 NormalZ=1 AngleXU=0 Radius=3.175
    g126: Circle CenterX=114.3 CenterY=-101.6 CenterZ=0 NormalX=0 NormalY=0 NormalZ=1 AngleXU=0 Radius=3.175
    g127: Circle CenterX=139.7 CenterY=-101.6 CenterZ=0 NormalX=0 NormalY=0 NormalZ=1 AngleXU=0 Radius=3.175
    g128: Circle CenterX=-139.7 CenterY=-127 CenterZ=0 NormalX=0 NormalY=0 NormalZ=1 AngleXU=0 Radius=3.175
    g129: Circle CenterX=-114.3 CenterY=-127 CenterZ=0 NormalX=0 NormalY=0 NormalZ=1 AngleXU=0 Radius=3.175
    g130: Circle CenterX=-88.9 CenterY=-127 CenterZ=0 NormalX=0 NormalY=0 NormalZ=1 AngleXU=0 Radius=3.175
    g131: Circle CenterX=-63.5 CenterY=-127 CenterZ=0 NormalX=0 NormalY=0 NormalZ=1 AngleXU=0 Radius=3.175
    g132: Circle CenterX=-38.1 CenterY=-127 CenterZ=0 NormalX=0 NormalY=0 NormalZ=1 AngleXU=0 Radius=3.175
    g133: Circle CenterX=-12.7 CenterY=-127 CenterZ=0 NormalX=0 NormalY=0 NormalZ=1 AngleXU=0 Radius=3.175
    g134: Circle CenterX=12.7 CenterY=-127 CenterZ=0 NormalX=0 NormalY=0 NormalZ=1 AngleXU=0 Radius=3.175
    g135: Circle CenterX=38.1 CenterY=-127 CenterZ=0 NormalX=0 NormalY=0 NormalZ=1 AngleXU=0 Radius=3.175
    g136: Circle CenterX=63.5 CenterY=-127 CenterZ=0 NormalX=0 NormalY=0 NormalZ=1 AngleXU=0 Radius=3.175
    g137: Circle CenterX=88.9 CenterY=-127 CenterZ=0 NormalX=0 NormalY=0 NormalZ=1 AngleXU=0 Radius=3.175
    g138: Circle CenterX=114.3 CenterY=-127 CenterZ=0 NormalX=0 NormalY=0 NormalZ=1 AngleXU=0 Radius=3.175
    g139: Circle CenterX=139.7 CenterY=-127 CenterZ=0 NormalX=0 NormalY=0 NormalZ=1 AngleXU=0 Radius=3.175
  constraints (414):
    c: Horizontal(g2)
    c: Vertical(g1)
    c: Tangent(g3,g4) = 1.5708
    c: Tangent(g0,g4) = 1.5708
    c: Tangent(g3,g5) = 1.5708
    c: Tangent(g2,g5) = 1.5708
    c: Tangent(g2,g6) = 1.5708
    c: Tangent(g1,g6) = 1.5708
    c: Tangent(g0,g7) = 1.5708
    c: Tangent(g1,g7) = 1.5708
    c: Diameter(g8) = 6.35
    c: Equal(g8,g9) = 6.35
    c: DistanceX(g8,g9) = 25.4
    c: DistanceX(g9,g10) = 25.4
    c: DistanceX(g10,g11) = 25.4
    c: DistanceX(g11,g12) = 25.4
    c: DistanceX(g12,g13) = 25.4
    c: DistanceX(g13,g14) = 25.4
    c: DistanceX(g14,g15) = 25.4
    c: DistanceX(g15,g16) = 25.4
    c: DistanceX(g16,g17) = 25.4
    c: DistanceX(g17,g18) = 25.4
    c: DistanceX(g18,g19) = 25.4
    c: Radius(g4) = 12.7
    c: Vertical(g3)
    c: Equal(g4,g5)
    c: Equal(g4,g7)
    c: DistanceX(g3,g1) = 304.8
    c: DistanceY(g2,g0) = 279.4
    c: Symmetric(g3,g1,g-2)
    c: Symmetric(g0,g2,g-1)
    c: Horizontal(g8,g9)
    c: Horizontal(g9,g10)
    c: Horizontal(g10,g11)
    c: Horizontal(g12,g13)
    c: Horizontal(g13,g14)
    c: Horizontal(g14,g15)
    c: Horizontal(g15,g16)
    c: Horizontal(g16,g17)
    c: Horizontal(g17,g18)
    c: Horizontal(g18,g19)
    c: Horizontal(g12,g11)
    c: Equal(g9,g10)
    c: Equal(g10,g11)
    c: Equal(g11,g12)
    c: Equal(g12,g13)
    c: Equal(g13,g14)
    c: Equal(g14,g15)
    c: Equal(g15,g16)
    c: Equal(g16,g17)
    c: Equal(g17,g18)
    c: Equal(g18,g19)
    c: Equal(g8,g20) = 6.35
    c: Equal(g20,g21) = 6.35
    c: DistanceX(g20,g21) = 25.4
    c: DistanceX(g21,g22) = 25.4
    c: DistanceX(g22,g23) = 25.4
    c: DistanceX(g23,g24) = 25.4
    c: DistanceX(g24,g25) = 25.4
    c: DistanceX(g25,g26) = 25.4
    c: DistanceX(g26,g27) = 25.4
    c: DistanceX(g27,g28) = 25.4
    c: DistanceX(g28,g29) = 25.4
    c: DistanceX(g29,g30) = 25.4
    c: DistanceX(g30,g31) = 25.4
    c: Horizontal(g20,g21)
    c: Horizontal(g21,g22)
    c: Horizontal(g22,g23)
    c: Horizontal(g24,g25)
    c: Horizontal(g25,g26)
    c: Horizontal(g26,g27)
    c: Horizontal(g27,g28)
    c: Horizontal(g28,g29)
    c: Horizontal(g29,g30)
    c: Horizontal(g30,g31)
    c: Horizontal(g24,g23)
    c: Equal(g21,g22)
    c: Equal(g22,g23)
    c: Equal(g23,g24)
    c: Equal(g24,g25)
    c: Equal(g25,g26)
    c: Equal(g26,g27)
    c: Equal(g27,g28)
    c: Equal(g28,g29)
    c: Equal(g29,g30)
    c: Equal(g30,g31)
    c: DistanceY(g20,g8) = 25.4
    c: Vertical(g20,g8)
    c: Equal(g8,g32) = 6.35
    c: Equal(g32,g33) = 6.35
    c: DistanceX(g32,g33) = 25.4
    c: DistanceX(g33,g34) = 25.4
    c: DistanceX(g34,g35) = 25.4
    c: DistanceX(g35,g36) = 25.4
    c: DistanceX(g36,g37) = 25.4
    c: DistanceX(g37,g38) = 25.4
    c: DistanceX(g38,g39) = 25.4
    c: DistanceX(g39,g40) = 25.4
    c: DistanceX(g40,g41) = 25.4
    c: DistanceX(g41,g42) = 25.4
    c: DistanceX(g42,g43) = 25.4
    c: Horizontal(g32,g33)
    c: Horizontal(g33,g34)
    c: Horizontal(g34,g35)
    c: Horizontal(g36,g37)
    c: Horizontal(g37,g38)
    c: Horizontal(g38,g39)
    c: Horizontal(g39,g40)
    c: Horizontal(g40,g41)
    c: Horizontal(g41,g42)
    c: Horizontal(g42,g43)
    c: Horizontal(g36,g35)
    c: Equal(g33,g34)
    c: Equal(g34,g35)
    c: Equal(g35,g36)
    c: Equal(g36,g37)
    c: Equal(g37,g38)
    c: Equal(g38,g39)
    c: Equal(g39,g40)
    c: Equal(g40,g41)
    c: Equal(g41,g42)
    c: Equal(g42,g43)
    c: Equal(g32,g44) = 6.35
    c: Equal(g44,g45) = 6.35
    c: DistanceX(g44,g45) = 25.4
    c: DistanceX(g45,g46) = 25.4
    c: DistanceX(g46,g47) = 25.4
    c: DistanceX(g47,g48) = 25.4
    c: DistanceX(g48,g49) = 25.4
    c: DistanceX(g49,g50) = 25.4
    c: DistanceX(g50,g51) = 25.4
    c: DistanceX(g51,g52) = 25.4
    c: DistanceX(g52,g53) = 25.4
    c: DistanceX(g53,g54) = 25.4
    c: DistanceX(g54,g55) = 25.4
    c: Horizontal(g44,g45)
    c: Horizontal(g45,g46)
    c: Horizontal(g46,g47)
    c: Horizontal(g48,g49)
    c: Horizontal(g49,g50)
    c: Horizontal(g50,g51)
    c: Horizontal(g51,g52)
    c: Horizontal(g52,g53)
    c: Horizontal(g53,g54)
    c: Horizontal(g54,g55)
    c: Horizontal(g48,g47)
    c: Equal(g45,g46)
    c: Equal(g46,g47)
    c: Equal(g47,g48)
    c: Equal(g48,g49)
    c: Equal(g49,g50)
    c: Equal(g50,g51)
    c: Equal(g51,g52)
    c: Equal(g52,g53)
    c: Equal(g53,g54)
    c: Equal(g54,g55)
    c: DistanceY(g44,g32) = 25.4
    c: Vertical(g44,g32)
    c: Vertical(g32,g20)
    c: DistanceY(g32,g20) = 25.4
    c: Equal(g8,g56) = 6.35
    c: Equal(g56,g57) = 6.35
    c: DistanceX(g56,g57) = 25.4
    c: DistanceX(g57,g58) = 25.4
    c: DistanceX(g58,g59) = 25.4
    c: DistanceX(g59,g60) = 25.4
    c: DistanceX(g60,g61) = 25.4
    c: DistanceX(g61,g62) = 25.4
    c: DistanceX(g62,g63) = 25.4
    c: DistanceX(g63,g64) = 25.4
    c: DistanceX(g64,g65) = 25.4
    c: DistanceX(g65,g66) = 25.4
    c: DistanceX(g66,g67) = 25.4
    c: Horizontal(g56,g57)
    c: Horizontal(g57,g58)
    c: Horizontal(g58,g59)
    c: Horizontal(g60,g61)
    c: Horizontal(g61,g62)
    c: Horizontal(g62,g63)
    c: Horizontal(g63,g64)
    c: Horizontal(g64,g65)
    c: Horizontal(g65,g66)
    c: Horizontal(g66,g67)
    c: Horizontal(g60,g59)
    c: Equal(g57,g58)
    c: Equal(g58,g59)
    c: Equal(g59,g60)
    c: Equal(g60,g61)
    c: Equal(g61,g62)
    c: Equal(g62,g63)
    c: Equal(g63,g64)
    c: Equal(g64,g65)
    c: Equal(g65,g66)
    c: Equal(g66,g67)
    c: Equal(g56,g68) = 6.35
    c: Equal(g68,g69) = 6.35
    c: DistanceX(g68,g69) = 25.4
    c: DistanceX(g69,g70) = 25.4
    c: DistanceX(g70,g71) = 25.4
    c: DistanceX(g71,g72) = 25.4
    c: DistanceX(g72,g73) = 25.4
    c: DistanceX(g73,g74) = 25.4
    c: DistanceX(g74,g75) = 25.4
    c: DistanceX(g75,g76) = 25.4
    c: DistanceX(g76,g77) = 25.4
    c: DistanceX(g77,g78) = 25.4
    c: DistanceX(g78,g79) = 25.4
    c: Horizontal(g68,g69)
    c: Horizontal(g69,g70)
    c: Horizontal(g70,g71)
    c: Horizontal(g72,g73)
    c: Horizontal(g73,g74)
    c: Horizontal(g74,g75)
    c: Horizontal(g75,g76)
    c: Horizontal(g76,g77)
    c: Horizontal(g77,g78)
    c: Horizontal(g78,g79)
    c: Horizontal(g72,g71)
    c: Equal(g69,g70)
    c: Equal(g70,g71)
    c: Equal(g71,g72)
    c: Equal(g72,g73)
    c: Equal(g73,g74)
    c: Equal(g74,g75)
    c: Equal(g75,g76)
    c: Equal(g76,g77)
    c: Equal(g77,g78)
    c: Equal(g78,g79)
    c: DistanceY(g68,g56) = 25.4
    c: Vertical(g68,g56)
    c: Equal(g56,g80) = 6.35
    c: Equal(g80,g81) = 6.35
    c: DistanceX(g80,g81) = 25.4
    c: DistanceX(g81,g82) = 25.4
    c: DistanceX(g82,g83) = 25.4
    c: DistanceX(g83,g84) = 25.4
    c: DistanceX(g84,g85) = 25.4
    c: DistanceX(g85,g86) = 25.4
    c: DistanceX(g86,g87) = 25.4
    c: DistanceX(g87,g88) = 25.4
    c: DistanceX(g88,g89) = 25.4
    c: DistanceX(g89,g90) = 25.4
    c: DistanceX(g90,g91) = 25.4
    c: Horizontal(g80,g81)
    c: Horizontal(g81,g82)
    c: Horizontal(g82,g83)
    c: Horizontal(g84,g85)
    c: Horizontal(g85,g86)
    c: Horizontal(g86,g87)
    c: Horizontal(g87,g88)
    c: Horizontal(g88,g89)
    c: Horizontal(g89,g90)
    c: Horizontal(g90,g91)
    c: Horizontal(g84,g83)
    c: Equal(g81,g82)
    c: Equal(g82,g83)
    c: Equal(g83,g84)
    c: Equal(g84,g85)
    c: Equal(g85,g86)
    c: Equal(g86,g87)
    c: Equal(g87,g88)
    c: Equal(g88,g89)
    c: Equal(g89,g90)
    c: Equal(g90,g91)
    c: Equal(g80,g92) = 6.35
    c: Equal(g92,g93) = 6.35
    c: DistanceX(g92,g93) = 25.4
    c: DistanceX(g93,g94) = 25.4
    c: DistanceX(g94,g95) = 25.4
    c: DistanceX(g95,g96) = 25.4
    c: DistanceX(g96,g97) = 25.4
    c: DistanceX(g97,g98) = 25.4
    c: DistanceX(g98,g99) = 25.4
    c: DistanceX(g99,g100) = 25.4
    c: DistanceX(g100,g101) = 25.4
    c: DistanceX(g101,g102) = 25.4
    c: DistanceX(g102,g103) = 25.4
    c: Horizontal(g92,g93)
    c: Horizontal(g93,g94)
    c: Horizontal(g94,g95)
    c: Horizontal(g96,g97)
    c: Horizontal(g97,g98)
    c: Horizontal(g98,g99)
    c: Horizontal(g99,g100)
    c: Horizontal(g100,g101)
    c: Horizontal(g101,g102)
    c: Horizontal(g102,g103)
    c: Horizontal(g96,g95)
    c: Equal(g93,g94)
    c: Equal(g94,g95)
    c: Equal(g95,g96)
    c: Equal(g96,g97)
    c: Equal(g97,g98)
    c: Equal(g98,g99)
    c: Equal(g99,g100)
    c: Equal(g100,g101)
    c: Equal(g101,g102)
    c: Equal(g102,g103)
    c: DistanceY(g92,g80) = 25.4
    c: Vertical(g92,g80)
    c: Vertical(g80,g68)
    c: DistanceY(g80,g68) = 25.4
    c: DistanceY(g56,g44) = 25.4
    c: Vertical(g56,g44)
    c: Equal(g104,g105) = 6.35
    c: DistanceX(g104,g105) = 25.4
    c: DistanceX(g105,g106) = 25.4
    c: DistanceX(g106,g107) = 25.4
    c: DistanceX(g107,g108) = 25.4
    c: DistanceX(g108,g109) = 25.4
    c: DistanceX(g109,g110) = 25.4
    c: DistanceX(g110,g111) = 25.4
    c: DistanceX(g111,g112) = 25.4
    c: DistanceX(g112,g113) = 25.4
    c: DistanceX(g113,g114) = 25.4
    c: DistanceX(g114,g115) = 25.4
    c: Horizontal(g104,g105)
    c: Horizontal(g105,g106)
    c: Horizontal(g106,g107)
    c: Horizontal(g108,g109)
    c: Horizontal(g109,g110)
    c: Horizontal(g110,g111)
    c: Horizontal(g111,g112)
    c: Horizontal(g112,g113)
    c: Horizontal(g113,g114)
    c: Horizontal(g114,g115)
    c: Horizontal(g108,g107)
    c: Equal(g105,g106)
    c: Equal(g106,g107)
    c: Equal(g107,g108)
    c: Equal(g108,g109)
    c: Equal(g109,g110)
    c: Equal(g110,g111)
    c: Equal(g111,g112)
    c: Equal(g112,g113)
    c: Equal(g113,g114)
    c: Equal(g114,g115)
    c: Equal(g116,g117) = 6.35
    c: DistanceX(g116,g117) = 25.4
    c: DistanceX(g117,g118) = 25.4
    c: DistanceX(g118,g119) = 25.4
    c: DistanceX(g119,g120) = 25.4
    c: DistanceX(g120,g121) = 25.4
    c: DistanceX(g121,g122) = 25.4
    c: DistanceX(g122,g123) = 25.4
    c: DistanceX(g123,g124) = 25.4
    c: DistanceX(g124,g125) = 25.4
    c: DistanceX(g125,g126) = 25.4
    c: DistanceX(g126,g127) = 25.4
    c: Horizontal(g116,g117)
    c: Horizontal(g117,g118)
    c: Horizontal(g118,g119)
    c: Horizontal(g120,g121)
    c: Horizontal(g121,g122)
    c: Horizontal(g122,g123)
    c: Horizontal(g123,g124)
    c: Horizontal(g124,g125)
    c: Horizontal(g125,g126)
    c: Horizontal(g126,g127)
    c: Horizontal(g120,g119)
    c: Equal(g117,g118)
    c: Equal(g118,g119)
    c: Equal(g119,g120)
    c: Equal(g120,g121)
    c: Equal(g121,g122)
    c: Equal(g122,g123)
    c: Equal(g123,g124)
    c: Equal(g124,g125)
    c: Equal(g125,g126)
    c: Equal(g126,g127)
    c: Equal(g116,g128) = 6.35
    c: Equal(g128,g129) = 6.35
    c: DistanceX(g128,g129) = 25.4
    c: DistanceX(g129,g130) = 25.4
    c: DistanceX(g130,g131) = 25.4
    c: DistanceX(g131,g132) = 25.4
    c: DistanceX(g132,g133) = 25.4
    c: DistanceX(g133,g134) = 25.4
    c: DistanceX(g134,g135) = 25.4
    c: DistanceX(g135,g136) = 25.4
    c: DistanceX(g136,g137) = 25.4
    c: DistanceX(g137,g138) = 25.4
    c: DistanceX(g138,g139) = 25.4
    c: Horizontal(g128,g129)
    c: Horizontal(g129,g130)
    c: Horizontal(g130,g131)
    c: Horizontal(g132,g133)
    c: Horizontal(g133,g134)
    c: Horizontal(g134,g135)
    c: Horizontal(g135,g136)
    c: Horizontal(g136,g137)
    c: Horizontal(g137,g138)
    c: Horizontal(g138,g139)
    c: Horizontal(g132,g131)
    c: Equal(g129,g130)
    c: Equal(g130,g131)
    c: Equal(g131,g132)
    c: Equal(g132,g133)
    c: Equal(g133,g134)
    c: Equal(g134,g135)
    c: Equal(g135,g136)
    c: Equal(g136,g137)
    c: Equal(g137,g138)
    c: Equal(g138,g139)
    c: DistanceY(g128,g116) = 25.4
    c: Vertical(g128,g116)
    c: Vertical(g116,g104)
    c: DistanceY(g116,g104) = 25.4
    c: Equal(g104,g92)
    c: DistanceY(g104,g92) = 25.4
    c: Vertical(g104,g92)
    c: Vertical(g128,g2)
    c: Horizontal(g128,g3)
    c: Equal(g116,g104)
FEATURE [PartDesign::Pad] Pad
  Direction = (1,1,1)
  Length = 8
  Length2 = 100
  Profile = -> Sketch
  Type = 0
FEATURE [PartDesign::CoordinateSystem] LCS_Edge
  AttacherType = Attacher::AttachEngine3D
  MapMode = 45
  Placement = pos=(-139.7,-127,8) rot=(0,0,-1;8.2e-05rad)
  Support = -> [Pad]
FEATURE [PartDesign::CoordinateSystem] LCS_Camera_Stand
  AttacherType = Attacher::AttachEngine3D
  MapMode = 45
  Placement = pos=(-88.9,-25.4,8) rot=(0,0,1;2.1e-05rad)
  Support = -> [Pad]
FEATURE [PartDesign::CoordinateSystem] LCS_Table_Foot1
  AttacherType = Attacher::AttachEngine3D
  MapMode = 45
  Placement = pos=(12.7,-25.4,8) rot=(0,0,-1;1e-06rad)
  Support = -> [Pad]
FEATURE [PartDesign::CoordinateSystem] LCS_Foot2
  AttacherType = Attacher::AttachEngine3D
  MapMode = 11
  Placement = pos=(12.7,25.4,8) rot=(0,0,1;1.5708rad)
  Support = -> [Pad]
FEATURE [PartDesign::CoordinateSystem] LCS_Foot3
  AttacherType = Attacher::AttachEngine3D
  MapMode = 11
  Placement = pos=(63.5,25.4,8) rot=(0,0,1;1.5708rad)
  Support = -> [Pad]
FEATURE [PartDesign::CoordinateSystem] LCS_Foot4
  AttacherType = Attacher::AttachEngine3D
  MapMode = 11
  Placement = pos=(63.5,-25.4,8) rot=(0,0,1;1.5708rad)
  Support = -> [Pad]
FEATURE [PartDesign::CoordinateSystem] LCS_Light1
  AttacherType = Attacher::AttachEngine3D
  MapMode = 11
  Placement = pos=(-38.1,-25.4,8) rot=(0,0,1;1.5708rad)
  Support = -> [Pad]
FEATURE [PartDesign::CoordinateSystem] LCS_Light2
  AttacherType = Attacher::AttachEngine3D
  MapMode = 11
  Placement = pos=(-38.1,25.4,8) rot=(0,0,1;1.5708rad)
  Support = -> [Pad]
FEATURE [PartDesign::CoordinateSystem] LCS_Light3
  AttacherType = Attacher::AttachEngine3D
  MapMode = 11
  Placement = pos=(-12.7,50.8,8) rot=(0,0,1;1.5708rad)
  Support = -> [Pad]
FEATURE [PartDesign::CoordinateSystem] LCS_Tablet
  AttacherType = Attacher::AttachEngine3D
FEATURE [PartDesign::CoordinateSystem] LCS_Tablet001
  AttacherType = Attacher::AttachEngine3D
  MapMode = 11
  Placement = pos=(114.3,25.4,8) rot=(0,0,1;1.5708rad)
  Support = -> [Pad]
FEATURE [PartDesign::CoordinateSystem] LCS_Micro
  AttacherType = Attacher::AttachEngine3D
  MapMode = 11
  Placement = pos=(12.7,-76.2,8) rot=(0,0,1;1.5708rad)
  Support = -> [Pad]
FEATURE [PartDesign::CoordinateSystem] LCS_Heat
  AttacherType = Attacher::AttachEngine3D
  MapMode = 11
  Placement = pos=(38.1,8e-15,8) rot=(0,0,1;1.5708rad)
  Support = -> [Pad]
FEATURE [PartDesign::Body] Body  label="Baseplate"
  Group = -> [Sketch,Pad,LCS_Edge,LCS_Camera_Stand,LCS_Table_Foot1,LCS_Foot2,LCS_Foot3,LCS_Foot4,LCS_Light1,LCS_Light2,LCS_Light3,LCS_Tablet,LCS_Tablet001,LCS_Micro,LCS_Heat]
  Origin = -> Origin
  Tip = -> Pad
---- part ../../Miscellaneous/Baseplate/Heating-Base.FCStd = doc fcstd_02965d79355e ----
FCSTD DOCUMENT  (FreeCAD 0.19R24344 (Git))
Label: Heating-Base
License: All rights reserved
LicenseURL: http://en.wikipedia.org/wiki/All_rights_reserved
objects: Sketcher::SketchObject×2, PartDesign::Pad×2, PartDesign::CoordinateSystem×1, PartDesign::Body×1
note: 8 computed .brp shape members not serialized (recipe doc carries the construction recipe); baked Part::Feature solids carry a one-line shape summary decoded from their .brp

FEATURE [Sketcher::SketchObject] Sketch
  FullyConstrained = true
  MapMode = 5
  Support = -> [XY_Plane]
  sketch-geometry (1):
    g0: Circle CenterX=0 CenterY=0 CenterZ=0 NormalX=0 NormalY=0 NormalZ=1 AngleXU=0 Radius=35
  constraints (2):
    c: Coincident(g0,g-1)
    c: Diameter(g0) = 70
FEATURE [PartDesign::Pad] Pad
  Direction = (1,1,1)
  Length = 5
  Length2 = 100
  Profile = -> Sketch
  Type = 0
FEATURE [Sketcher::SketchObject] Sketch001
  FullyConstrained = true
  MapMode = 5
  Placement = pos=(0,0,0) rot=(1,0,0;3.14159rad)
  Support = -> [Pad]
  sketch-geometry (1):
    g0: Circle CenterX=0 CenterY=0 CenterZ=0 NormalX=0 NormalY=0 NormalZ=1 AngleXU=0 Radius=3.175
  constraints (2):
    c: Coincident(g0,g-1)
    c: Diameter(g0) = 6.35
FEATURE [PartDesign::Pad] Pad001
  BaseFeature = -> Pad
  Direction = (1,1,1)
  Length = 25
  Length2 = 100
  Profile = -> Sketch001
  Type = 0
FEATURE [PartDesign::CoordinateSystem] LCS_Base
  AttacherType = Attacher::AttachEngine3D
  MapMode = 45
  Placement = pos=(9e-16,-6e-16,-25) rot=(0,0,1;0rad)
  Support = -> [Pad001]
FEATURE [PartDesign::Body] Body  label="Heat_pad"
  Group = -> [Sketch,Pad,Sketch001,Pad001,LCS_Base]
  Origin = -> Origin
  Tip = -> Pad001
---- part ../../Miscellaneous/Holder_Tablet/Holder_Tablet.FCStd = doc fcstd_169d3be56f88 ----
FCSTD DOCUMENT  (FreeCAD 0.19R24344 (Git))
Label: Holder_Tablet
Comment: First draft for a tablet holder. Ended up using a comercially available tablet holder instead.
License: Creative Commons Attribution-NonCommercial-ShareAlike
LicenseURL: http://creativecommons.org/licenses/by-nc-sa/4.0/
objects: PartDesign::Fillet×11, Sketcher::SketchObject×5, PartDesign::Pad×3, PartDesign::CoordinateSystem×2, PartDesign::Pocket×1, PartDesign::Revolution×1, PartDesign::Body×1
note: 40 computed .brp shape members not serialized (recipe doc carries the construction recipe); baked Part::Feature solids carry a one-line shape summary decoded from their .brp

FEATURE [Sketcher::SketchObject] Sketch
  FullyConstrained = true
  MapMode = 5
  Placement = pos=(0,0,0) rot=(1,0,0;1.5708rad)
  Support = -> [XZ_Plane]
  sketch-geometry (10):
    g0: LineSegment StartX=0 StartY=104.8 StartZ=0 EndX=0 EndY=0 EndZ=0
    g1: ArcOfCircle CenterX=-4.9 CenterY=104.8 CenterZ=0 NormalX=0 NormalY=0 NormalZ=1 AngleXU=0 Radius=4.9 StartAngle=1.3e-15 EndAngle=1.5708
    g2: ArcOfCircle CenterX=-4.9 CenterY=-1.25256e-05 CenterZ=0 NormalX=0 NormalY=0 NormalZ=1 AngleXU=0 Radius=4.9 StartAngle=3.14159 EndAngle=6.28319
    g3: LineSegment StartX=3 StartY=0 StartZ=0 EndX=3 EndY=104.8 EndZ=0
    g4: ArcOfCircle CenterX=-4.5 CenterY=0 CenterZ=0 NormalX=0 NormalY=0 NormalZ=1 AngleXU=0 Radius=7.5 StartAngle=3.14159 EndAngle=6.28319
    g5: ArcOfCircle CenterX=-4.9 CenterY=104.388 CenterZ=0 NormalX=0 NormalY=0 NormalZ=1 AngleXU=0 Radius=5.31162 StartAngle=1.5708 EndAngle=3.66519
    g6: ArcOfCircle CenterX=-4.19834 CenterY=105.681 CenterZ=0 NormalX=0 NormalY=0 NormalZ=1 AngleXU=0 Radius=7.25201 StartAngle=6.16144 EndAngle=10.1757
    g7: ArcOfCircle CenterX=-10.9 CenterY=-1e-16 CenterZ=0 NormalX=0 NormalY=0 NormalZ=1 AngleXU=0 Radius=1.1 StartAngle=1e-16 EndAngle=3.14159
    g8: ArcOfCircle CenterX=-10 CenterY=101.233 CenterZ=0 NormalX=0 NormalY=0 NormalZ=1 AngleXU=0 Radius=0.707107 StartAngle=5.49779 EndAngle=7.06858
    g9: LineSegment StartX=-4.9 StartY=-4.90001 StartZ=0 EndX=0.1 EndY=-4.90001 EndZ=0
  constraints (34):
    c: PointOnObject(g0,g-2)
    c: Coincident(g2,g0)
    c: Vertical(g3)
    c: Coincident(g4,g3)
    c: Horizontal(g2,g3)
    c: DistanceX(g2,g0) = 9.8
    c: Radius(g2) = 4.9
    c: Angle(g1) = 1.5708
    c: Radius(g1) = 4.9
    c: Tangent(g1,g0) = 1.5708
    c: DistanceX(g5,g0) = 9.5
    c: Tangent(g5,g1) = -1.5708
    c: DistanceX(g0,g3) = 3
    c: Coincident(g3,g6)
    c: Radius(g4) = 7.5
    c: Coincident(g7,g4)
    c: Coincident(g7,g2)
    c: Angle(g7) = 3.14159
    c: Horizontal(g4,g2)
    c: Horizontal(g2,g0)
    c: Angle(g4) = 3.14159
    c: Coincident(g8,g5)
    c: Coincident(g8,g6)
    c: Angle(g8) = 1.5708
    c: Vertical(g6,g5)
    c: Horizontal(g3,g0)
    c: Angle(g6) = 4.01426
    c: DistanceY(g6,g5) = 1
    c: Angle(g5) = 2.0944
    c: Coincident(g0,g-1)
    c: Horizontal(g9)
    c: Tangent(g9,g2) = -1.5708
    c: DistanceX(g9,g9) = 5
    c: DistanceY(g9,g1) = 114.6
FEATURE [PartDesign::Pad] Pad
  Direction = (1,1,1)
  Length = 100
  Length2 = 100
  Placement = pos=(0,0,0) rot=(1,0,0;1.5708rad)
  Profile = -> Sketch
  Type = 0
FEATURE [Sketcher::SketchObject] Sketch001
  ExternalGeometry = -> [Pad]
  FullyConstrained = true
  MapMode = 5
  Placement = pos=(3,0,0) rot=(0.707107,0,0.707107;3.14159rad)
  Support = -> [Pad]
  sketch-geometry (8):
    g0: Circle CenterX=52.4 CenterY=108.5 CenterZ=0 NormalX=0 NormalY=0 NormalZ=1 AngleXU=0 Radius=55
    g1: Circle CenterX=-23.6 CenterY=50 CenterZ=0 NormalX=0 NormalY=0 NormalZ=1 AngleXU=0 Radius=36.5
    g2: Circle CenterX=52.4 CenterY=-8.5 CenterZ=0 NormalX=0 NormalY=0 NormalZ=1 AngleXU=0 Radius=55
    g3: Circle CenterX=131.4 CenterY=50 CenterZ=0 NormalX=0 NormalY=0 NormalZ=1 AngleXU=0 Radius=36.5
    g4: LineSegment StartX=6.66e-14 StartY=100 StartZ=0 EndX=104.8 EndY=-7.11e-14 EndZ=0
    g5: LineSegment StartX=104.8 StartY=100 StartZ=0 EndX=0 EndY=0 EndZ=0
    g6: GeomPoint X=52.4 Y=50 Z=0
    g7: LineSegment StartX=-47.6 StartY=50 StartZ=0 EndX=152.4 EndY=50 EndZ=0
  constraints (21):
    c: Radius(g0) = 55
    c: Coincident(g4,g-3)
    c: Coincident(g4,g-4)
    c: Coincident(g5,g-3)
    c: Coincident(g5,g-1)
    c: PointOnObject(g6,g5)
    c: PointOnObject(g6,g4)
    c: Horizontal(g7)
    c: PointOnObject(g6,g7)
    c: Symmetric(g2,g0,g7)
    c: Equal(g2,g0)
    c: PointOnObject(g1,g7)
    c: Equal(g1,g3)
    c: PointOnObject(g3,g7)
    c: Radius(g1) = 36.5
    c: Vertical(g0,g6)
    c: DistanceX(g1,g6) = 76
    c: DistanceX(g6,g3) = 79
    c: DistanceX(g7,g7) = 200
    c: DistanceX(g7,g6) = 100
    c: DistanceY(g6,g0) = 58.5
FEATURE [PartDesign::Pocket] Pocket
  BaseFeature = -> Pad
  Length = 32
  Length2 = 100
  Midplane = true
  Placement = pos=(0,0,0) rot=(1,0,0;1.5708rad)
  Profile = -> Sketch001
  Type = 0
FEATURE [Sketcher::SketchObject] Sketch002
  FullyConstrained = true
  MapMode = 5
  Placement = pos=(3,0,0) rot=(0.707107,0,0.707107;3.14159rad)
  Support = -> [Pocket]
  sketch-geometry (4):
    g0: LineSegment StartX=15 StartY=65 StartZ=0 EndX=15 EndY=35 EndZ=0
    g1: LineSegment StartX=-25 StartY=35 StartZ=0 EndX=-25 EndY=65 EndZ=0
    g2: ArcOfCircle CenterX=-5 CenterY=85 CenterZ=0 NormalX=0 NormalY=0 NormalZ=1 AngleXU=0 Radius=28.2843 StartAngle=3.92699 EndAngle=5.49779
    g3: ArcOfCircle CenterX=-5 CenterY=15 CenterZ=0 NormalX=0 NormalY=0 NormalZ=1 AngleXU=0 Radius=28.2843 StartAngle=0.785398 EndAngle=2.35619
  constraints (14):
    c: Vertical(g0)
    c: Vertical(g1)
    c: DistanceY(g1,g1) = 30
    c: DistanceX(g1,g0) = 40
    c: Coincident(g2,g1)
    c: Coincident(g2,g0)
    c: Coincident(g3,g1)
    c: Coincident(g3,g0)
    c: DistanceX(g-1,g0) = 15
    c: DistanceY(g-1,g0) = 35
    c: Horizontal(g1,g0)
    c: Horizontal(g1,g0)
    c: Angle(g2) = 1.5708
    c: Angle(g3) = 1.5708
FEATURE [PartDesign::Pad] Pad001
  BaseFeature = -> Pocket
  Direction = (1,1,1)
  Length = 3
  Length2 = 100
  Placement = pos=(0,0,0) rot=(1,0,0;1.5708rad)
  Profile = -> Sketch002
  Reversed = true
  Type = 0
FEATURE [Sketcher::SketchObject] Sketch003
  ExternalGeometry = -> [Pad001]
  FullyConstrained = true
  MapMode = 5
  Placement = pos=(-5.5e-15,-5.5e-15,-25) rot=(1,0,0;3.14159rad)
  Support = -> [Pad001]
  sketch-geometry (16):
    g0: LineSegment StartX=25.3157 StartY=36.25 StartZ=0 EndX=25.3157 EndY=63.75 EndZ=0
    g1: LineSegment StartX=25.3157 StartY=63.75 StartZ=0 EndX=1.5 EndY=77.5 EndZ=0
    g2: LineSegment StartX=1.5 StartY=77.5 StartZ=0 EndX=-22.3157 EndY=63.75 EndZ=0
    g3: LineSegment StartX=-22.3157 StartY=63.75 StartZ=0 EndX=-22.3157 EndY=36.25 EndZ=0
    g4: LineSegment StartX=-22.3157 StartY=36.25 StartZ=0 EndX=1.5 EndY=22.5 EndZ=0
    g5: LineSegment StartX=1.5 StartY=22.5 StartZ=0 EndX=25.3157 EndY=36.25 EndZ=0
    g6: Circle CenterX=1.5 CenterY=50 CenterZ=0 NormalX=0 NormalY=0 NormalZ=1 AngleXU=0 Radius=27.5
    g7: Circle CenterX=-11.2 CenterY=62.7 CenterZ=0 NormalX=0 NormalY=0 NormalZ=1 AngleXU=0 Radius=3.2
    g8: Circle CenterX=-11.2 CenterY=37.3 CenterZ=0 NormalX=0 NormalY=0 NormalZ=1 AngleXU=0 Radius=3.2
    g9: Circle CenterX=14.2 CenterY=37.3 CenterZ=0 NormalX=0 NormalY=0 NormalZ=1 AngleXU=0 Radius=3.2
    g10: Circle CenterX=14.2 CenterY=62.7 CenterZ=0 NormalX=0 NormalY=0 NormalZ=1 AngleXU=0 Radius=3.2
    g11: LineSegment StartX=-4e-16 StartY=65 StartZ=0 EndX=3 EndY=35 EndZ=0
    g12: LineSegment StartX=3 StartY=65 StartZ=0 EndX=-4e-16 EndY=35 EndZ=0
    g13: GeomPoint X=1.5 Y=50 Z=0
    g14: LineSegment StartX=-18.5 StartY=50 StartZ=0 EndX=21.5 EndY=50 EndZ=0
    g15: LineSegment StartX=1.5 StartY=70 StartZ=0 EndX=1.5 EndY=30 EndZ=0
  constraints (38):
    c: Coincident(g0,g1)
    c: Coincident(g1,g2)
    c: Coincident(g2,g3)
    c: Coincident(g3,g4)
    c: Coincident(g4,g5)
    c: Coincident(g5,g0)
    c: Equal(g0, g1-g5) x5
    c: PointOnObject(g0,g6)
    c: PointOnObject(g1,g6)
    c: PointOnObject(g2,g6)
    c: PointOnObject(g3,g6)
    c: PointOnObject(g4,g6)
    c: Vertical(g0)
    c: Diameter(g7) = 6.4
    c: Equal(g7,g10)
    c: Equal(g8,g7)
    c: Equal(g9,g7)
    c: DistanceX(g7,g10) = 25.4
    c: DistanceY(g8,g7) = 25.4
    c: DistanceX(g8,g9) = 25.4
    c: DistanceY(g9,g10) = 25.4
    c: DistanceY(g4,g1) = 55
    c: Coincident(g11,g-3)
    c: Coincident(g11,g-4)
    c: Coincident(g12,g-3)
    c: Coincident(g12,g-4)
    c: PointOnObject(g13,g11)
    c: PointOnObject(g13,g12)
    c: DistanceY(g15,g15) = 40
    c: DistanceX(g14,g14) = 40
    c: PointOnObject(g13,g14)
    c: PointOnObject(g13,g15)
    c: Symmetric(g7,g10,g15)
    c: Symmetric(g10,g9,g14)
    c: Symmetric(g0,g2,g15)
    c: Symmetric(g0,g0,g14)
    c: Symmetric(g14,g14,g15)
    c: Symmetric(g15,g15,g14)
FEATURE [PartDesign::Pad] Pad002
  BaseFeature = -> Pad001
  Direction = (1,1,1)
  Length = 4
  Length2 = 100
  Placement = pos=(0,0,0) rot=(1,0,0;1.5708rad)
  Profile = -> Sketch003
  Type = 0
FEATURE [Sketcher::SketchObject] Sketch004
  FullyConstrained = true
  MapMode = 5
  Placement = pos=(-5.5e-15,-1.07e-14,-25) rot=(0,0,1;3.14159rad)
  Support = -> [Pad002]
  sketch-geometry (4):
    g0: LineSegment StartX=-10 StartY=51.5 StartZ=0 EndX=0 EndY=51.5 EndZ=0
    g1: LineSegment StartX=0 StartY=48.5 StartZ=0 EndX=-10 EndY=48.5 EndZ=0
    g2: ArcOfCircle CenterX=-10 CenterY=50 CenterZ=0 NormalX=0 NormalY=0 NormalZ=1 AngleXU=0 Radius=1.5 StartAngle=1.5708 EndAngle=4.71239
    g3: LineSegment StartX=0 StartY=51.5 StartZ=0 EndX=0 EndY=48.5 EndZ=0
  constraints (13):
    c: PointOnObject(g0,g-2)
    c: Horizontal(g0)
    c: PointOnObject(g1,g-2)
    c: Horizontal(g1)
    c: Coincident(g2,g1)
    c: Coincident(g2,g0)
    c: Angle(g2) = 3.14159
    c: DistanceY(g1,g0) = 3
    c: DistanceX(g0,g0) = 10
    c: Vertical(g1,g0)
    c: DistanceY(g-1,g2) = 50
    c: Coincident(g3,g0)
    c: Coincident(g3,g1)
FEATURE [PartDesign::Revolution] Revolution
  Angle = 180
  Axis = (0,-1,9e-16)
  Base = (-5.6e-15,-2.19e-14,-25)
  BaseFeature = -> Pad002
  Placement = pos=(0,0,0) rot=(1,0,0;1.5708rad)
  Profile = -> Sketch004
  ReferenceAxis = -> Sketch004 [V_Axis]
FEATURE [PartDesign::Fillet] Fillet
  Base = -> Revolution [Edge38]
  BaseFeature = -> Revolution
  Placement = pos=(0,0,0) rot=(1,0,0;1.5708rad)
  Radius = 2
  SupportTransform = false
FEATURE [PartDesign::Fillet] Fillet001
  Base = -> Fillet [Edge25]
  BaseFeature = -> Fillet
  Placement = pos=(0,0,0) rot=(1,0,0;1.5708rad)
  Radius = 2
  SupportTransform = false
FEATURE [PartDesign::Fillet] Fillet002
  Base = -> Fillet001 [Edge32]
  BaseFeature = -> Fillet001
  Placement = pos=(0,0,0) rot=(1,0,0;1.5708rad)
  Radius = 2
  SupportTransform = false
FEATURE [PartDesign::Fillet] Fillet003
  Base = -> Fillet002 [Edge33]
  BaseFeature = -> Fillet002
  Placement = pos=(0,0,0) rot=(1,0,0;1.5708rad)
  Radius = 2
  SupportTransform = false
FEATURE [PartDesign::Fillet] Fillet004
  Base = -> Fillet003 [Edge34]
  BaseFeature = -> Fillet003
  Placement = pos=(0,0,0) rot=(1,0,0;1.5708rad)
  Radius = 2
  SupportTransform = false
FEATURE [PartDesign::Fillet] Fillet005
  Base = -> Fillet004 [Edge35]
  BaseFeature = -> Fillet004
  Placement = pos=(0,0,0) rot=(1,0,0;1.5708rad)
  Radius = 2
  SupportTransform = false
FEATURE [PartDesign::Fillet] Fillet006
  Base = -> Fillet005 [Edge124]
  BaseFeature = -> Fillet005
  Placement = pos=(0,0,0) rot=(1,0,0;1.5708rad)
  Radius = 1
  SupportTransform = false
FEATURE [PartDesign::Fillet] Fillet007
  Base = -> Fillet006 [Edge38]
  BaseFeature = -> Fillet006
  Placement = pos=(0,0,0) rot=(1,0,0;1.5708rad)
  Radius = 1
  SupportTransform = false
FEATURE [PartDesign::Fillet] Fillet008
  Base = -> Fillet007 [Edge60]
  BaseFeature = -> Fillet007
  Placement = pos=(0,0,0) rot=(1,0,0;1.5708rad)
  Radius = 1
  SupportTransform = false
FEATURE [PartDesign::Fillet] Fillet009
  Base = -> Fillet008 [Edge96]
  BaseFeature = -> Fillet008
  Placement = pos=(0,0,0) rot=(1,0,0;1.5708rad)
  Radius = 1
  SupportTransform = false
FEATURE [PartDesign::Fillet] Fillet010
  Base = -> Fillet009 [Edge37]
  BaseFeature = -> Fillet009
  Placement = pos=(0,0,0) rot=(1,0,0;1.5708rad)
  Radius = 1
  SupportTransform = false
FEATURE [PartDesign::CoordinateSystem] LCS_Base
  AttacherType = Attacher::AttachEngine3D
  MapMode = 45
  Placement = pos=(-11.2,-37.3,-29) rot=(0,0,1;0rad)
  Support = -> [Fillet010]
FEATURE [PartDesign::CoordinateSystem] LCS_Tablet
  AttacherType = Attacher::AttachEngine3D
  MapMode = 45
  Placement = pos=(0,-50,57.518) rot=(0.57735,0.57735,0.57735;2.0944rad)
  Support = -> [Fillet010]
FEATURE [PartDesign::Body] Body  label="FireHolder"
  Group = -> [Sketch,Pad,Sketch001,Pocket,Sketch002,Pad001,Sketch003,Pad002,Sketch004,Revolution,Fillet,Fillet001,Fillet002,Fillet003,Fillet004,Fillet005,Fillet006,Fillet007,Fillet008,Fillet009,Fillet010,LCS_Base,LCS_Tablet]
  Origin = -> Origin
  Tip = -> Fillet010
---- part ../../Miscellaneous/Scale-Bar/Scale-Bar.FCStd = doc fcstd_313a3d742b27 ----
FCSTD DOCUMENT  (FreeCAD 0.19R24344 (Git))
Label: Scale Bar
License: Creative Commons Attribution-NonCommercial-ShareAlike
LicenseURL: http://creativecommons.org/licenses/by-nc-sa/4.0/
objects: Part::Box×15, Part::Part2DObjectPython×2, PartDesign::CoordinateSystem×1, App::Part×1
note: 18 computed .brp shape members not serialized (recipe doc carries the construction recipe); baked Part::Feature solids carry a one-line shape summary decoded from their .brp

FEATURE [Part::Box] Box  label="Cube"
  AttacherType = Attacher::AttachEngine3D
  Height = 1
  Length = 10
  Placement = pos=(-10,0,0) rot=(0,0,1;0rad)
  Width = 1
FEATURE [Part::Box] Box001  label="Cube001"
  AttacherType = Attacher::AttachEngine3D
  Height = 1
  Length = 1
  Placement = pos=(-16,0,0) rot=(0,0,1;0rad)
  Width = 1
FEATURE [Part::Box] Box002  label="Cube002"
  AttacherType = Attacher::AttachEngine3D
  Height = 1
  Length = 1
  Placement = pos=(-18,0,0) rot=(0,0,1;0rad)
  Width = 1
FEATURE [Part::Box] Box003  label="Cube003"
  AttacherType = Attacher::AttachEngine3D
  Height = 1
  Length = 1
  Placement = pos=(-20,0,0) rot=(0,0,1;0rad)
  Width = 1
FEATURE [PartDesign::CoordinateSystem] LCS_0
  AttacherType = Attacher::AttachEngine3D
  MapMode = 2
  Support = -> [X_Axis]
FEATURE [Part::Box] Box004  label="Cube004"
  AttacherType = Attacher::AttachEngine3D
  Height = 1
  Length = 10
  Placement = pos=(-1,10,0) rot=(0,0,-1;1.5708rad)
  Width = 1
FEATURE [Part::Box] Box005  label="Cube005"
  AttacherType = Attacher::AttachEngine3D
  Height = 1
  Length = 1
  Placement = pos=(-1,16,0) rot=(0,0,-1;1.5708rad)
  Width = 1
FEATURE [Part::Box] Box006  label="Cube006"
  AttacherType = Attacher::AttachEngine3D
  Height = 1
  Length = 1
  Placement = pos=(-1,18,0) rot=(0,0,-1;1.5708rad)
  Width = 1
FEATURE [Part::Box] Box007  label="Cube007"
  AttacherType = Attacher::AttachEngine3D
  Height = 1
  Length = 1
  Placement = pos=(-1,20,0) rot=(0,0,-1;1.5708rad)
  Width = 1
FEATURE [Part::Box] Box010  label="Cube010"
  AttacherType = Attacher::AttachEngine3D
  Height = 1
  Length = 1
  Placement = pos=(-1,0,18) rot=(0,1,0;1.5708rad)
  Width = 1
FEATURE [Part::Box] Box008  label="Cube008"
  AttacherType = Attacher::AttachEngine3D
  Height = 1
  Length = 10
  Placement = pos=(-1,0,10) rot=(0,1,0;1.5708rad)
  Width = 1
FEATURE [Part::Box] Box009  label="Cube009"
  AttacherType = Attacher::AttachEngine3D
  Height = 1
  Length = 1
  Placement = pos=(-1,0,16) rot=(0,1,0;1.5708rad)
  Width = 1
FEATURE [Part::Box] Box011  label="Cube011"
  AttacherType = Attacher::AttachEngine3D
  Height = 1
  Length = 1
  Placement = pos=(-1,0,20) rot=(0,1,0;1.5708rad)
  Width = 1
FEATURE [Part::Box] Box012  label="Cube012"
  AttacherType = Attacher::AttachEngine3D
  Height = 19.9
  Length = 0.9
  Placement = pos=(-0.95,0.05,0) rot=(0,0,1;0rad)
  Width = 0.9
FEATURE [Part::Box] Box013  label="Cube013"
  AttacherType = Attacher::AttachEngine3D
  Height = 0.9
  Length = 19.9
  Placement = pos=(-19.95,0.05,0.05) rot=(0,0,1;0rad)
  Width = 0.9
FEATURE [Part::Box] Box014  label="Cube014"
  AttacherType = Attacher::AttachEngine3D
  Height = 0.9
  Length = 0.9
  Placement = pos=(-0.95,0.05,0.05) rot=(0,0,1;0rad)
  Width = 19.9
FEATURE [Part::Part2DObjectPython] ShapeString  label="X-Label"  # Draft 2D object (typed FeaturePython)
  FontFile = <userpath>/prj/2019_Janelia_Component-Design/Extra/Scale Bar/DejaVuSans.ttf
  Placement = pos=(-18.94,2,0) rot=(0,0,1;0rad)
  Size = 4
  String = 20mm
  Tracking = 0
FEATURE [Part::Part2DObjectPython] ShapeString001  label="Y-Label"  # Draft 2D object (typed FeaturePython)
  FontFile = <userpath>/prj/2019_Janelia_Component-Design/Extra/Scale Bar/DejaVuSans.ttf
  Placement = pos=(0,2,2) rot=(0,1,0;36.1283rad)
  Size = 4
  String = 20mm
  Tracking = 0
FEATURE [App::Part] Scalebar
  Group = -> [LCS_0,Box,Box001,Box002,Box003,Box004,Box005,Box006,Box007,Box008,Box009,Box010,Box011,Box012,Box013,Box014,ShapeString,ShapeString001]
  Origin = -> Origin
---- part ../../Miscellaneous/Spheres/Sphere-9mm-plain.FCStd = doc fcstd_c3aec2aec0a9 ----
FCSTD DOCUMENT  (FreeCAD 0.19R24344 (Git))
Label: Sphere-9mm-plain
License: All rights reserved
LicenseURL: http://en.wikipedia.org/wiki/All_rights_reserved
objects: PartDesign::CoordinateSystem×2, Part::Sphere×1, App::Part×1
note: 3 computed .brp shape members not serialized (recipe doc carries the construction recipe); baked Part::Feature solids carry a one-line shape summary decoded from their .brp

FEATURE [Part::Sphere] Sphere
  Angle1 = -90
  Angle2 = 90
  Angle3 = 360
  AttacherType = Attacher::AttachEngine3D
  Radius = 4.5
FEATURE [PartDesign::CoordinateSystem] LCS_0
  AttacherType = Attacher::AttachEngine3D
  MapMode = 2
  Support = -> [X_Axis]
FEATURE [PartDesign::CoordinateSystem] LCS_Sphere
  AttacherType = Attacher::AttachEngine3D
  MapMode = 45
  Support = -> [Sphere]
FEATURE [App::Part] Sphere001
  Group = -> [LCS_0,Sphere,LCS_Sphere]
  Origin = -> Origin
---- part ../../Miscellaneous/Tablet/FireTablet.FCStd = doc fcstd_a8faa1765717 ----
FCSTD DOCUMENT  (FreeCAD 0.19R24344 (Git))
Label: FireTablet
Comment: Rough sketch of the Amazon Fire tablet.
License: Creative Commons Attribution-NonCommercial-ShareAlike
LicenseURL: http://creativecommons.org/licenses/by-nc-sa/4.0/
objects: Sketcher::SketchObject×9, PartDesign::Pad×5, PartDesign::Revolution×4, PartDesign::Body×3, PartDesign::CoordinateSystem×2, App::Part×1
note: 32 computed .brp shape members not serialized (recipe doc carries the construction recipe); baked Part::Feature solids carry a one-line shape summary decoded from their .brp

FEATURE [Sketcher::SketchObject] Sketch
  FullyConstrained = true
  MapMode = 5
  Support = -> [XY_Plane]
  sketch-geometry (4):
    g0: LineSegment StartX=-95 StartY=56.5 StartZ=0 EndX=95 EndY=56.5 EndZ=0
    g1: LineSegment StartX=95 StartY=56.5 StartZ=0 EndX=95 EndY=-56.5 EndZ=0
    g2: LineSegment StartX=95 StartY=-56.5 StartZ=0 EndX=-95 EndY=-56.5 EndZ=0
    g3: LineSegment StartX=-95 StartY=-56.5 StartZ=0 EndX=-95 EndY=56.5 EndZ=0
  constraints (10):
    c: Coincident(g0,g1)
    c: Coincident(g1,g2)
    c: Coincident(g2,g3)
    c: Coincident(g3,g0)
    c: Horizontal(g2)
    c: Vertical(g1)
    c: DistanceX(g0,g0) = 190
    c: DistanceY(g3,g3) = 113
    c: Symmetric(g0,g0,g-2)
    c: Symmetric(g0,g2,g-1)
FEATURE [PartDesign::Pad] Pad
  Direction = (1,1,1)
  Length = 3
  Length2 = 100
  Profile = -> Sketch
  Type = 0
FEATURE [PartDesign::Body] Body  label="Front Glass"
  Group = -> [Sketch,Pad]
  Origin = -> Origin
  Tip = -> Pad
FEATURE [Sketcher::SketchObject] Sketch001
  FullyConstrained = true
  MapMode = 5
  Placement = pos=(0,0,0) rot=(0.57735,0.57735,0.57735;2.0944rad)
  Support = -> [YZ_Plane001]
  sketch-geometry (6):
    g0: ArcOfCircle CenterX=-54.4289 CenterY=-2 CenterZ=0 NormalX=0 NormalY=0 NormalZ=1 AngleXU=0 Radius=5.41196 StartAngle=1.9635 EndAngle=4.31969
    g1: ArcOfCircle CenterX=54.4289 CenterY=-2 CenterZ=0 NormalX=0 NormalY=0 NormalZ=1 AngleXU=0 Radius=5.41196 StartAngle=5.10509 EndAngle=7.46128
    g2: LineSegment StartX=-56.5 StartY=-7 StartZ=0 EndX=56.5 EndY=-7 EndZ=0
    g3: LineSegment StartX=-56.5 StartY=3 StartZ=0 EndX=-56.5 EndY=0 EndZ=0
    g4: LineSegment StartX=-56.5 StartY=0 StartZ=0 EndX=56.5 EndY=0 EndZ=0
    g5: LineSegment StartX=56.5 StartY=0 StartZ=0 EndX=56.5 EndY=3 EndZ=0
  constraints (19):
    c: DistanceY(g0,g0) = 10
    c: DistanceY(g1,g1) = 10
    c: Vertical(g0,g0)
    c: Vertical(g1,g1)
    c: DistanceX(g0,g-1) = 56.5
    c: DistanceY(g-1,g0) = 3
    c: Symmetric(g0,g1,g-2)
    c: Angle(g0) = 2.35619
    c: Angle(g1) = 2.35619
    c: Coincident(g2,g0)
    c: Coincident(g2,g1)
    c: Coincident(g3,g0)
    c: PointOnObject(g3,g-1)
    c: Vertical(g3)
    c: Coincident(g4,g3)
    c: PointOnObject(g4,g-1)
    c: Coincident(g5,g4)
    c: Coincident(g5,g1)
    c: Vertical(g5)
FEATURE [PartDesign::Pad] Pad001
  Direction = (1,1,1)
  Length = 190
  Length2 = 100
  Midplane = true
  Placement = pos=(0,0,0) rot=(0.57735,0.57735,0.57735;2.0944rad)
  Profile = -> Sketch001
  Type = 0
FEATURE [Sketcher::SketchObject] Sketch002
  ExternalGeometry = -> [Pad001]
  FullyConstrained = true
  MapMode = 5
  Placement = pos=(0,0,0) rot=(1,0,0;1.5708rad)
  Support = -> [XZ_Plane001]
  sketch-geometry (2):
    g0: ArcOfCircle CenterX=-92.9289 CenterY=-2 CenterZ=0 NormalX=0 NormalY=0 NormalZ=1 AngleXU=0 Radius=5.41196 StartAngle=1.9635 EndAngle=4.31969
    g1: LineSegment StartX=-95 StartY=3 StartZ=0 EndX=-95 EndY=-7 EndZ=0
  constraints (5):
    c: Coincident(g0,g-3)
    c: Coincident(g0,g-3)
    c: Angle(g0) = 2.35619
    c: Coincident(g1,g0)
    c: Coincident(g1,g0)
FEATURE [PartDesign::Pad] Pad002
  BaseFeature = -> Pad001
  Direction = (1,1,1)
  Length = 113
  Length2 = 100
  Midplane = true
  Placement = pos=(0,0,0) rot=(0.57735,0.57735,0.57735;2.0944rad)
  Profile = -> Sketch002
  Type = 0
FEATURE [Sketcher::SketchObject] Sketch003
  ExternalGeometry = -> [Pad002]
  FullyConstrained = true
  MapMode = 5
  Placement = pos=(0,0,0) rot=(1,0,0;1.5708rad)
  Support = -> [XZ_Plane001]
  sketch-geometry (2):
    g0: ArcOfCircle CenterX=92.9289 CenterY=-2 CenterZ=0 NormalX=0 NormalY=0 NormalZ=1 AngleXU=0 Radius=5.41196 StartAngle=5.10509 EndAngle=7.46128
    g1: LineSegment StartX=95 StartY=3 StartZ=0 EndX=95 EndY=-7 EndZ=0
  constraints (5):
    c: Coincident(g0,g-3)
    c: Coincident(g0,g-3)
    c: Coincident(g1,g0)
    c: Coincident(g1,g0)
    c: Angle(g0) = 2.35619
FEATURE [PartDesign::Pad] Pad003
  BaseFeature = -> Pad002
  Direction = (1,1,1)
  Length = 113
  Length2 = 100
  Midplane = true
  Placement = pos=(0,0,0) rot=(0.57735,0.57735,0.57735;2.0944rad)
  Profile = -> Sketch003
  Type = 0
FEATURE [Sketcher::SketchObject] Sketch005
  ExternalGeometry = -> [Pad003]
  FullyConstrained = true
  MapMode = 5
  Placement = pos=(0,-56.5,1.24e-14) rot=(0.57735,0.57735,-0.57735;2.0944rad)
  Support = -> [Pad003]
  sketch-geometry (2):
    g0: ArcOfCircle CenterX=2 CenterY=-92.9289 CenterZ=0 NormalX=0 NormalY=0 NormalZ=1 AngleXU=0 Radius=5.41196 StartAngle=3.53429 EndAngle=5.89049
    g1: LineSegment StartX=-3 StartY=-95 StartZ=0 EndX=7 EndY=-95 EndZ=0
  constraints (5):
    c: Coincident(g0,g-3)
    c: Coincident(g0,g-3)
    c: Tangent(g0,g-3)
    c: Coincident(g1,g0)
    c: Coincident(g1,g0)
FEATURE [PartDesign::Revolution] Revolution
  Angle = 90
  Axis = (7e-16,-4e-16,-1)
  Base = (-95,-56.5,3)
  BaseFeature = -> Pad003
  Placement = pos=(0,0,0) rot=(0.57735,0.57735,0.57735;2.0944rad)
  Profile = -> Sketch005
  ReferenceAxis = -> Pad003 [Edge11]
  Reversed = true
FEATURE [Sketcher::SketchObject] Sketch006
  ExternalGeometry = -> [Revolution]
  FullyConstrained = true
  MapMode = 5
  Placement = pos=(-95,2.09e-14,-2.09e-14) rot=(0.57735,0.57735,-0.57735;4.18879rad)
  Support = -> [Revolution]
  sketch-geometry (2):
    g0: ArcOfCircle CenterX=54.4289 CenterY=2 CenterZ=0 NormalX=0 NormalY=0 NormalZ=1 AngleXU=0 Radius=5.41196 StartAngle=5.10509 EndAngle=7.46128
    g1: LineSegment StartX=56.5 StartY=7 StartZ=0 EndX=56.5 EndY=-3 EndZ=0
  constraints (5):
    c: Coincident(g0,g-3)
    c: Coincident(g0,g-3)
    c: Coincident(g0,g1)
    c: Coincident(g1,g0)
    c: Angle(g0) = 2.35619
FEATURE [PartDesign::Revolution] Revolution001
  Angle = 90
  Axis = (1e-15,-6e-16,-1)
  Base = (-95,56.5,3)
  BaseFeature = -> Revolution
  Placement = pos=(0,0,0) rot=(0.57735,0.57735,0.57735;2.0944rad)
  Profile = -> Sketch006
  ReferenceAxis = -> Revolution [Edge28]
  Reversed = true
FEATURE [Sketcher::SketchObject] Sketch007
  ExternalGeometry = -> [Revolution001]
  FullyConstrained = true
  MapMode = 5
  Placement = pos=(95,-2.09e-14,2.09e-14) rot=(0.57735,0.57735,0.57735;2.0944rad)
  Support = -> [Revolution001]
  sketch-geometry (2):
    g0: ArcOfCircle CenterX=54.4289 CenterY=-2 CenterZ=0 NormalX=0 NormalY=0 NormalZ=1 AngleXU=0 Radius=5.41196 StartAngle=5.10509 EndAngle=7.46128
    g1: LineSegment StartX=56.5 StartY=3 StartZ=0 EndX=56.5 EndY=-7 EndZ=0
  constraints (5):
    c: Coincident(g0,g-3)
    c: Coincident(g0,g-3)
    c: Tangent(g0,g-3)
    c: Coincident(g1,g0)
    c: Coincident(g1,g0)
FEATURE [PartDesign::Revolution] Revolution002
  Angle = 90
  Axis = (3.8e-15,-6e-16,-1)
  Base = (95,56.5,3)
  BaseFeature = -> Revolution001
  Placement = pos=(0,0,0) rot=(0.57735,0.57735,0.57735;2.0944rad)
  Profile = -> Sketch007
  ReferenceAxis = -> Revolution001 [Edge30]
FEATURE [Sketcher::SketchObject] Sketch008
  ExternalGeometry = -> [Revolution002]
  FullyConstrained = true
  MapMode = 5
  Placement = pos=(95,-2.09e-14,2.09e-14) rot=(0.57735,0.57735,0.57735;2.0944rad)
  Support = -> [Revolution002]
  sketch-geometry (2):
    g0: ArcOfCircle CenterX=-54.4289 CenterY=-2 CenterZ=0 NormalX=0 NormalY=0 NormalZ=1 AngleXU=0 Radius=5.41196 StartAngle=1.9635 EndAngle=4.31969
    g1: LineSegment StartX=-56.5 StartY=3 StartZ=0 EndX=-56.5 EndY=-7 EndZ=0
  constraints (5):
    c: Coincident(g0,g-3)
    c: Coincident(g0,g-3)
    c: Tangent(g0,g-3)
    c: Coincident(g1,g0)
    c: Coincident(g1,g0)
FEATURE [PartDesign::Revolution] Revolution003
  Angle = 90
  Axis = (4.2e-15,-7e-16,-1)
  Base = (95,-56.5,3)
  BaseFeature = -> Revolution002
  Placement = pos=(0,0,0) rot=(0.57735,0.57735,0.57735;2.0944rad)
  Profile = -> Sketch008
  ReferenceAxis = -> Revolution002 [Edge14]
  Reversed = true
FEATURE [PartDesign::Body] Body001  label="Case"
  Group = -> [Sketch001,Pad001,Sketch002,Pad002,Sketch003,Pad003,Sketch005,Revolution,Sketch006,Revolution001,Sketch007,Revolution002,Sketch008,Revolution003]
  Origin = -> Origin001
  Tip = -> Revolution003
FEATURE [Sketcher::SketchObject] Sketch009
  FullyConstrained = true
  MapMode = 5
  Support = -> [XY_Plane002]
  sketch-geometry (4):
    g0: LineSegment StartX=-77 StartY=45 StartZ=0 EndX=77 EndY=45 EndZ=0
    g1: LineSegment StartX=77 StartY=45 StartZ=0 EndX=77 EndY=-45 EndZ=0
    g2: LineSegment StartX=77 StartY=-45 StartZ=0 EndX=-77 EndY=-45 EndZ=0
    g3: LineSegment StartX=-77 StartY=-45 StartZ=0 EndX=-77 EndY=45 EndZ=0
  constraints (10):
    c: Coincident(g0,g1)
    c: Coincident(g1,g2)
    c: Coincident(g2,g3)
    c: Coincident(g3,g0)
    c: Horizontal(g2)
    c: Vertical(g1)
    c: DistanceX(g0,g0) = 154
    c: DistanceY(g3,g3) = 90
    c: Symmetric(g0,g0,g-2)
    c: Symmetric(g0,g2,g-1)
FEATURE [PartDesign::Pad] Pad004
  Direction = (1,1,1)
  Length = 1
  Length2 = 100
  Profile = -> Sketch009
  Reversed = true
  Type = 0
FEATURE [PartDesign::Body] Body002  label="Screen"
  Group = -> [Sketch009,Pad004]
  Origin = -> Origin002
  Placement = pos=(0,0,0.1) rot=(0,0,1;0rad)
  Tip = -> Pad004
FEATURE [PartDesign::CoordinateSystem] LCS_0
  AttacherType = Attacher::AttachEngine3D
  MapMode = 2
  Support = -> [X_Axis003]
FEATURE [PartDesign::CoordinateSystem] LCS_Tablet_Back
  AttacherType = Attacher::AttachEngine3D
  MapMode = 45
  Placement = pos=(6.5e-15,3e-16,-7) rot=(0,0,1;1.5708rad)
  Support = -> [Revolution003]
FEATURE [App::Part] Fire7
  Group = -> [LCS_0,Body,Body001,Body002,LCS_Tablet_Back]
  Origin = -> Origin003
---- part ../../Tethering/MicroManipulator/MicroManipulator_Assembly.FCStd = doc fcstd_2ffb4ee6dabc ----
FCSTD DOCUMENT  (FreeCAD 0.19R24344 (Git))
Label: MicroManipulator_Assembly
Comment: The assembled MicroManipulator. This assembly consists of six parts. The type of arm depends on the application, the one currently shown is intended for the tethering station.
License: Creative Commons Attribution-NonCommercial-ShareAlike
LicenseURL: http://creativecommons.org/licenses/by-nc-sa/4.0/
objects: Part::FeaturePython×25, App::Link×10, App::DocumentObjectGroup×2, PartDesign::CoordinateSystem×1, App::FeaturePython×1, App::Part×1
note: 26 computed .brp shape members not serialized (recipe doc carries the construction recipe); baked Part::Feature solids carry a one-line shape summary decoded from their .brp
EXTERNAL_REF file=MicroManipulator_Rail_bottom.FCStd obj=Bottom_Mount_Edge
EXTERNAL_REF file=MicroManipulator_Rail_bottom.FCStd obj=Body
EXTERNAL_REF file=MicroManipulator_Carriage_bottom-center.FCStd obj=ScrewBottom_LCS
EXTERNAL_REF file=MicroManipulator_Rail_bottom.FCStd obj=Bottom_Cage_LCS
EXTERNAL_REF file=MicroManipulator_Carriage_bottom-center.FCStd obj=CenterSlider
EXTERNAL_REF file=MicroManipulator_Carriage_bottom-center.FCStd obj=ScrewTop_LCS
EXTERNAL_REF file=MicroManipulator_Rail_center.FCStd obj=Screw_LCS
EXTERNAL_REF file=MicroManipulator_Rail_center.FCStd obj=CenterCage
EXTERNAL_REF file=MicroManipulator_Rail_center.FCStd obj=Top_Mount_LCS
EXTERNAL_REF file=MicroManipulator_Rail_top.FCStd obj=MountPoint_LCS
EXTERNAL_REF file=MicroManipulator_Rail_top.FCStd obj=CageTop
EXTERNAL_REF file=MicroManipulator_Carriage_Hinge_top.FCStd obj=Screw_LCS
EXTERNAL_REF file=MicroManipulator_Rail_top.FCStd obj=Screw_LCS
EXTERNAL_REF file=MicroManipulator_Carriage_Hinge_top.FCStd obj=Slider
EXTERNAL_REF file=MicroManipulator_Arm_TetherStation.FCStd obj=ArmMount_LCS
EXTERNAL_REF file=MicroManipulator_Carriage_Hinge_top.FCStd obj=ArmMount_LCS
EXTERNAL_REF file=MicroManipulator_Arm_TetherStation.FCStd obj=TetherArm
EXTERNAL_REF file=MicroManipulator_Arm_tilted_Arena.FCStd obj=LCS_Hinge
EXTERNAL_REF file=MicroManipulator_Arm_tilted_Arena.FCStd obj=Body
EXTERNAL_REF file=MicroManipulator_Arm_tilted_Arena.FCStd obj=LCS_Luer
EXTERNAL_REF file=../../Miscellaneous/Luer-Tether/Luer-Tether.FCStd obj=Part
EXTERNAL_REF file=MicroManipulator_Rail_top.FCStd obj=LCS_Fasten_1
EXTERNAL_REF file=MicroManipulator_Rail_top.FCStd obj=LCS_Fasten_2
EXTERNAL_REF file=MicroManipulator_Rail_top.FCStd obj=LCS_Fasten_3
EXTERNAL_REF file=MicroManipulator_Rail_top.FCStd obj=LCS_Fasten_4

FEATURE [App::DocumentObjectGroup] Parts
FEATURE [PartDesign::CoordinateSystem] LCS_Origin
  AttacherType = Attacher::AttachEngine3D
  MapMode = 2
  Support = -> [X_Axis]
FEATURE [App::DocumentObjectGroup] Constraints
FEATURE [App::FeaturePython] Variables  # WARN: FeaturePython — macro-defined, semantics opaque (R4)
  ArmRotation = 0
  BottomMovement = 8.3
  CenterMovement = 14
  TopMovement = 5
FEATURE [App::Link] Micro_Cage_bottom
FEATURE [App::Link] Micro_Cage_bottom001
FEATURE [App::Link] Micro_Cage_bottom_Body
  AssemblyType = Asm4EE
  AttachedBy = #Bottom_Mount_Edge
  AttachedTo = Parent Assembly#LCS_Origin
  LinkPlacement = pos=(-12.7,32.4,4) rot=(0,0,-1;1.5708rad)
  LinkedObject = -> <external MicroManipulator_Rail_bottom.FCStd>#Body
  Placement = pos=(-12.7,32.4,4) rot=(0,0,-1;1.5708rad)
  expr: Placement = LCS_Origin.Placement * AttachmentOffset * MicroManipulator_Rail_bottom#Bottom_Mount_Edge.Placement ^ -1
FEATURE [App::Link] CenterSliderCombined_CenterSlider
  AssemblyType = Asm4EE
  AttachedBy = #ScrewBottom_LCS
  AttachedTo = Micro_Cage_bottom_Body#Bottom_Cage_LCS
  AttachmentOffset = pos=(0,0,8.3) rot=(0,0,1;0rad)
  LinkPlacement = pos=(-12.7,24.1,4) rot=(0,0,-1;1.5708rad)
  LinkedObject = -> <external MicroManipulator_Carriage_bottom-center.FCStd>#CenterSlider
  Placement = pos=(-12.7,24.1,4) rot=(0,0,-1;1.5708rad)
  expr: .AttachmentOffset.Base.z = Variables.BottomMovement
  expr: Placement = Micro_Cage_bottom_Body.Placement * MicroManipulator_Rail_bottom#Bottom_Cage_LCS.Placement * AttachmentOffset * MicroManipulator_Carriage_bottom_center#ScrewBottom_LCS.Placement ^ -1
FEATURE [App::Link] CenterCage
  AssemblyType = Asm4EE
  AttachedBy = #Screw_LCS
  AttachedTo = CenterSliderCombined_CenterSlider#ScrewTop_LCS
  AttachmentOffset = pos=(0,0,14) rot=(0,1,0;3.14159rad)
  LinkPlacement = pos=(-36.7,12.1,23) rot=(1,0,0;3.14159rad)
  LinkedObject = -> <external MicroManipulator_Rail_center.FCStd>#CenterCage
  Placement = pos=(-36.7,12.1,23) rot=(1,0,0;3.14159rad)
  expr: .AttachmentOffset.Base.z = Variables.CenterMovement
  expr: Placement = CenterSliderCombined_CenterSlider.Placement * MicroManipulator_Carriage_bottom_center#ScrewTop_LCS.Placement * AttachmentOffset * MicroManipulator_Rail_center#Screw_LCS.Placement ^ -1
FEATURE [App::Link] CageTop
  AssemblyType = Asm4EE
  AttachedBy = #MountPoint_LCS
  AttachedTo = CenterCage#Top_Mount_LCS
  AttachmentOffset = pos=(0,0,0) rot=(0,0,1;3.14159rad)
  LinkPlacement = pos=(-20.7,12.1,66) rot=(-3e-06,-1,2e-06;4.71239rad)
  LinkedObject = -> <external MicroManipulator_Rail_top.FCStd>#CageTop
  Placement = pos=(-20.7,12.1,66) rot=(-3e-06,-1,2e-06;4.71239rad)
  expr: Placement = CenterCage.Placement * MicroManipulator_Rail_center#Top_Mount_LCS.Placement * AttachmentOffset * MicroManipulator_Rail_top#MountPoint_LCS.Placement ^ -1
FEATURE [App::Link] SliderTop
  AssemblyType = Asm4EE
  AttachedBy = #Screw_LCS
  AttachedTo = CageTop#Screw_LCS
  AttachmentOffset = pos=(0,0,5) rot=(0,0,1;0rad)
  LinkPlacement = pos=(-20.7,12.1,63) rot=(-3e-06,-1,2e-06;4.71239rad)
  LinkedObject = -> <external MicroManipulator_Carriage_Hinge_top.FCStd>#Slider
  Placement = pos=(-20.7,12.1,63) rot=(-3e-06,-1,2e-06;4.71239rad)
  expr: .AttachmentOffset.Base.z = Variables.TopMovement
  expr: Placement = CageTop.Placement * MicroManipulator_Rail_top#Screw_LCS.Placement * AttachmentOffset * MicroManipulator_Carriage_Hinge_top#Screw_LCS.Placement ^ -1
FEATURE [App::Link] TetherArm
  AssemblyType = Asm4EE
  AttachedBy = #ArmMount_LCS
  AttachedTo = SliderTop#ArmMount_LCS
  LinkPlacement = pos=(-3.70005,12.1,50.5) rot=(0,0,-1;3.1416rad)
  LinkedObject = -> <external MicroManipulator_Arm_TetherStation.FCStd>#TetherArm
  Placement = pos=(-3.70005,12.1,50.5) rot=(0,0,-1;3.1416rad)
  expr: .AttachmentOffset.Rotation.Angle = Variables.ArmRotation
  expr: Placement = SliderTop.Placement * MicroManipulator_Carriage_Hinge_top#ArmMount_LCS.Placement * AttachmentOffset * MicroManipulator_Arm_TetherStation#ArmMount_LCS.Placement ^ -1
FEATURE [Part::FeaturePython] Screw  # WARN: FeaturePython — macro-defined, semantics opaque (R4)
  invert = false
  offset = 0
FEATURE [Part::FeaturePython] Screw001  # WARN: FeaturePython — macro-defined, semantics opaque (R4)
  invert = false
  offset = 0
FEATURE [App::Link] MicroManipulator_Arm_tilted_Arena_Arm_tilted_Arena
  AssemblyType = Asm4EE
  AttachedBy = #LCS_Hinge
  AttachedTo = SliderTop#ArmMount_LCS
  AttachmentOffset = pos=(0,0,0) rot=(0,0,1;-0.471239rad)
  LinkPlacement = pos=(-3.70005,12.1,50.5) rot=(0,0,1;2.67035rad)
  LinkedObject = -> <external MicroManipulator_Arm_tilted_Arena.FCStd>#Body
  Placement = pos=(-3.70005,12.1,50.5) rot=(0,0,1;2.67035rad)
  expr: Placement = SliderTop.Placement * MicroManipulator_Carriage_Hinge_top#ArmMount_LCS.Placement * AttachmentOffset * MicroManipulator_Arm_tilted_Arena#LCS_Hinge.Placement ^ -1
FEATURE [App::Link] Luer_Tether_Part
  AssemblyType = Asm4EE
  AttachedBy = #LCS_Luer
  AttachedTo = MicroManipulator_Arm_tilted_Arena_Arm_tilted_Arena#LCS_Luer
  AttachmentOffset = pos=(0,0,6) rot=(0,0,1;0rad)
  LinkPlacement = pos=(52.5794,-20.6202,50.0652) rot=(0.443537,-0.72379,0.528586;1.71809rad)
  LinkedObject = -> <external ../../Miscellaneous/Luer-Tether/Luer-Tether.FCStd>#Part
  Placement = pos=(52.5794,-20.6202,50.0652) rot=(0.443537,-0.72379,0.528586;1.71809rad)
  expr: Placement = MicroManipulator_Arm_tilted_Arena_Arm_tilted_Arena.Placement * MicroManipulator_Arm_tilted_Arena#LCS_Luer.Placement * AttachmentOffset * Luer_Tether#LCS_Luer.Placement ^ -1
FEATURE [Part::FeaturePython] Washer  label="M3-Washer"  # Fasteners workbench fastener (typed FeaturePython)
  AssemblyType = Asm4EE
  AttachedBy = Origin
  AttachedTo = CageTop#Screw_LCS
  AttachmentOffset = pos=(0,0,0) rot=(1,0,0;3.14159rad)
  Placement = pos=(-15.7,12.1,68) rot=(0,0,1;1.57079rad)
  diameter = 4
  invert = false
  matchOuter = false
  offset = 0
  type = 3
  expr: Placement = CageTop.Placement * MicroManipulator_Rail_top#Screw_LCS.Placement * AttachmentOffset
FEATURE [Part::FeaturePython] Washer001  label="M3-Washer024"  # Fasteners workbench fastener (typed FeaturePython)
  AssemblyType = Asm4EE
  AttachedBy = Origin
  AttachedTo = CageTop#Screw_LCS
  AttachmentOffset = pos=(0,0,2.7) rot=(1,0,0;3.14159rad)
  Placement = pos=(-15.7,12.1,65.3) rot=(0,0,1;1.57079rad)
  diameter = 4
  invert = false
  matchOuter = false
  offset = 0
  type = 3
  expr: Placement = CageTop.Placement * MicroManipulator_Rail_top#Screw_LCS.Placement * AttachmentOffset
FEATURE [Part::FeaturePython] Screw002  label="M3x40-Screw"  # Fasteners workbench fastener (typed FeaturePython)
  AssemblyType = Asm4EE
  AttachedBy = Origin
  AttachedTo = CageTop#Screw_LCS
  AttachmentOffset = pos=(0,0,-0.5) rot=(1,0,0;3.14159rad)
  Placement = pos=(-15.7,12.1,68.5) rot=(0,0,1;1.57079rad)
  diameter = 4
  invert = false
  length = 10
  lengthCustom = 40
  matchOuter = false
  offset = 0
  thread = true
  type = 27
  expr: Placement = CageTop.Placement * MicroManipulator_Rail_top#Screw_LCS.Placement * AttachmentOffset
FEATURE [Part::FeaturePython] Nut  label="M3-Nut040"  # Fasteners workbench fastener (typed FeaturePython)
  AssemblyType = Asm4EE
  AttachedBy = Origin
  AttachedTo = CageTop#Screw_LCS
  AttachmentOffset = pos=(0,0,2.8) rot=(0,0,1;0rad)
  Placement = pos=(-15.7,12.1,65.2) rot=(0.707109,0.707105,0;3.14159rad)
  diameter = 4
  invert = false
  matchOuter = false
  offset = 0
  thread = false
  type = 7
  expr: Placement = CageTop.Placement * MicroManipulator_Rail_top#Screw_LCS.Placement * AttachmentOffset
FEATURE [Part::FeaturePython] Nut001  label="M3-Nut041"  # Fasteners workbench fastener (typed FeaturePython)
  AssemblyType = Asm4EE
  AttachedBy = Origin
  AttachedTo = SliderTop#ArmMount_LCS
  AttachmentOffset = pos=(0,0,-5) rot=(0,0,1;0rad)
  Placement = pos=(-3.70005,12.1,45.5) rot=(0,0,-1;1.5708rad)
  diameter = 4
  invert = false
  matchOuter = false
  offset = 0
  thread = false
  type = 7
  expr: Placement = SliderTop.Placement * MicroManipulator_Carriage_Hinge_top#ArmMount_LCS.Placement * AttachmentOffset
FEATURE [Part::FeaturePython] Screw003  label="M3x10-Screw"  # Fasteners workbench fastener (typed FeaturePython)
  AssemblyType = Asm4EE
  AttachedBy = Origin
  AttachedTo = SliderTop#ArmMount_LCS
  AttachmentOffset = pos=(0,0,4.4) rot=(0,0,1;0rad)
  Placement = pos=(-3.70005,12.1,54.9) rot=(0,0,-1;1.5708rad)
  diameter = 4
  invert = false
  length = 3
  lengthCustom = 10
  matchOuter = false
  offset = 0
  thread = false
  type = 27
  expr: Placement = SliderTop.Placement * MicroManipulator_Carriage_Hinge_top#ArmMount_LCS.Placement * AttachmentOffset
FEATURE [Part::FeaturePython] Screw004  label="M3x6-Screw"  # Fasteners workbench fastener (typed FeaturePython)
  AssemblyType = Asm4EE
  AttachedBy = Origin
  AttachedTo = CageTop#LCS_Fasten_1
  AttachmentOffset = pos=(0,0,0) rot=(1,0,0;3.14159rad)
  Placement = pos=(-11.7001,2.1,28) rot=(0.009203,0.012998,-0.999873;5e-06rad)
  diameter = 4
  invert = false
  length = 1
  lengthCustom = 6
  matchOuter = false
  offset = 0
  thread = false
  type = 27
  expr: Placement = CageTop.Placement * MicroManipulator_Rail_top#LCS_Fasten_1.Placement * AttachmentOffset
FEATURE [Part::FeaturePython] Screw005  label="M3x6-Screw016"  # Fasteners workbench fastener (typed FeaturePython)
  AssemblyType = Asm4EE
  AttachedBy = Origin
  AttachedTo = CageTop#LCS_Fasten_2
  AttachmentOffset = pos=(0,0,0) rot=(0,-1,0;3.14159rad)
  Placement = pos=(-21.7001,2.10005,28) rot=(0,0,1;3.14159rad)
  diameter = 4
  invert = false
  length = 1
  lengthCustom = 6
  matchOuter = false
  offset = 0
  thread = false
  type = 27
  expr: Placement = CageTop.Placement * MicroManipulator_Rail_top#LCS_Fasten_2.Placement * AttachmentOffset
FEATURE [Part::FeaturePython] Screw006  label="M3x6-Screw017"  # Fasteners workbench fastener (typed FeaturePython)
  AssemblyType = Asm4EE
  AttachedBy = Origin
  AttachedTo = CageTop#LCS_Fasten_3
  AttachmentOffset = pos=(0,0,0) rot=(1,0,0;3.14159rad)
  Placement = pos=(-11.7,22.1,28) rot=(0.009203,0.012998,-0.999873;5e-06rad)
  diameter = 4
  invert = false
  length = 1
  lengthCustom = 6
  matchOuter = false
  offset = 0
  thread = false
  type = 27
  expr: Placement = CageTop.Placement * MicroManipulator_Rail_top#LCS_Fasten_3.Placement * AttachmentOffset
FEATURE [Part::FeaturePython] Screw007  label="M3x6-Screw018"  # Fasteners workbench fastener (typed FeaturePython)
  AssemblyType = Asm4EE
  AttachedBy = Origin
  AttachedTo = CageTop#LCS_Fasten_4
  AttachmentOffset = pos=(0,0,0) rot=(1,0,0;3.14159rad)
  Placement = pos=(-21.7,22.1,28) rot=(0.009203,0.012998,-0.999873;5e-06rad)
  diameter = 4
  invert = false
  length = 1
  lengthCustom = 6
  matchOuter = false
  offset = 0
  thread = false
  type = 27
  expr: Placement = CageTop.Placement * MicroManipulator_Rail_top#LCS_Fasten_4.Placement * AttachmentOffset
FEATURE [Part::FeaturePython] Nut002  label="M3-Nut"  # Fasteners workbench fastener (typed FeaturePython)
  AssemblyType = Asm4EE
  AttachedBy = Origin
  AttachedTo = SliderTop#Screw_LCS
  AttachmentOffset = pos=(0,0,4.5) rot=(0,0,-1;1.5708rad)
  Placement = pos=(-15.7,12.1,58.5) rot=(2e-06,1,0;3.14159rad)
  diameter = 4
  invert = false
  matchOuter = false
  offset = 0
  thread = false
  type = 7
  expr: Placement = SliderTop.Placement * MicroManipulator_Carriage_Hinge_top#Screw_LCS.Placement * AttachmentOffset
FEATURE [Part::FeaturePython] Nut003  label="M3-Nut042"  # Fasteners workbench fastener (typed FeaturePython)
  AssemblyType = Asm4EE
  AttachedBy = Origin
  AttachedTo = CageTop#LCS_Fasten_1
  AttachmentOffset = pos=(0,0,4) rot=(0,0,-1;3.14159rad)
  Placement = pos=(-11.7001,2.1,24) rot=(3e-06,1,0;3.14159rad)
  diameter = 4
  invert = false
  matchOuter = false
  offset = 0
  thread = false
  type = 7
  expr: Placement = CageTop.Placement * MicroManipulator_Rail_top#LCS_Fasten_1.Placement * AttachmentOffset
FEATURE [Part::FeaturePython] Nut004  label="M3-Nut043"  # Fasteners workbench fastener (typed FeaturePython)
  AssemblyType = Asm4EE
  AttachedBy = Origin
  AttachedTo = CageTop#LCS_Fasten_2
  AttachmentOffset = pos=(0,0,4) rot=(0,0,1;0rad)
  Placement = pos=(-21.7001,2.10005,24) rot=(1,-3e-06,0;3.14159rad)
  diameter = 4
  invert = false
  matchOuter = false
  offset = 0
  thread = false
  type = 7
  expr: Placement = CageTop.Placement * MicroManipulator_Rail_top#LCS_Fasten_2.Placement * AttachmentOffset
FEATURE [Part::FeaturePython] Nut005  label="M3-Nut044"  # Fasteners workbench fastener (typed FeaturePython)
  AssemblyType = Asm4EE
  AttachedBy = Origin
  AttachedTo = CageTop#LCS_Fasten_3
  AttachmentOffset = pos=(0,0,4) rot=(0,0,1;0rad)
  Placement = pos=(-11.7,22.1,24) rot=(1,-3e-06,0;3.14159rad)
  diameter = 4
  invert = false
  matchOuter = false
  offset = 0
  thread = false
  type = 7
  expr: Placement = CageTop.Placement * MicroManipulator_Rail_top#LCS_Fasten_3.Placement * AttachmentOffset
FEATURE [Part::FeaturePython] Nut006  label="M3-Nut045"  # Fasteners workbench fastener (typed FeaturePython)
  AssemblyType = Asm4EE
  AttachedBy = Origin
  AttachedTo = CageTop#LCS_Fasten_4
  AttachmentOffset = pos=(0,0,4) rot=(0,0,1;0rad)
  Placement = pos=(-21.7,22.1,24) rot=(1,-3e-06,0;3.14159rad)
  diameter = 4
  invert = false
  matchOuter = false
  offset = 0
  thread = false
  type = 7
  expr: Placement = CageTop.Placement * MicroManipulator_Rail_top#LCS_Fasten_4.Placement * AttachmentOffset
FEATURE [Part::FeaturePython] Screw008  label="M3x40-Screw005"  # Fasteners workbench fastener (typed FeaturePython)
  AssemblyType = Asm4EE
  AttachedBy = Origin
  AttachedTo = CenterCage#Screw_LCS
  AttachmentOffset = pos=(0,0,-0.7) rot=(1,0,0;3.14159rad)
  Placement = pos=(-39.4,12.1,18) rot=(0.57735,-0.57735,-0.57735;2.0944rad)
  diameter = 4
  invert = false
  length = 10
  lengthCustom = 40
  matchOuter = false
  offset = 0
  thread = true
  type = 27
  expr: Placement = CenterCage.Placement * MicroManipulator_Rail_center#Screw_LCS.Placement * AttachmentOffset
FEATURE [Part::FeaturePython] Washer002  label="M3-Washer022"  # Fasteners workbench fastener (typed FeaturePython)
  AssemblyType = Asm4EE
  AttachedBy = Origin
  AttachedTo = CenterCage#Screw_LCS
  AttachmentOffset = pos=(0,0,0) rot=(1,0,0;3.14159rad)
  Placement = pos=(-38.7,12.1,18) rot=(0.57735,-0.57735,-0.57735;2.0944rad)
  diameter = 4
  invert = false
  matchOuter = false
  offset = 0
  type = 3
  expr: Placement = CenterCage.Placement * MicroManipulator_Rail_center#Screw_LCS.Placement * AttachmentOffset
FEATURE [Part::FeaturePython] Washer003  label="M3-Washer023"  # Fasteners workbench fastener (typed FeaturePython)
  AssemblyType = Asm4EE
  AttachedBy = Origin
  AttachedTo = CenterCage#Screw_LCS
  AttachmentOffset = pos=(0,0,2) rot=(0,0,1;0rad)
  Placement = pos=(-36.7,12.1,18) rot=(0.57735,-0.57735,0.57735;4.18879rad)
  diameter = 4
  invert = false
  matchOuter = false
  offset = 0
  type = 3
  expr: Placement = CenterCage.Placement * MicroManipulator_Rail_center#Screw_LCS.Placement * AttachmentOffset
FEATURE [Part::FeaturePython] Nut007  label="M3-Nut046"  # Fasteners workbench fastener (typed FeaturePython)
  AssemblyType = Asm4EE
  AttachedBy = Origin
  AttachedTo = CenterCage#Screw_LCS
  AttachmentOffset = pos=(0,0,2.8) rot=(0,0,1;0rad)
  Placement = pos=(-35.9,12.1,18) rot=(0.57735,-0.57735,0.57735;4.18879rad)
  diameter = 4
  invert = false
  matchOuter = false
  offset = 0
  thread = false
  type = 7
  expr: Placement = CenterCage.Placement * MicroManipulator_Rail_center#Screw_LCS.Placement * AttachmentOffset
FEATURE [Part::FeaturePython] Screw009  label="M3x40-Screw004"  # Fasteners workbench fastener (typed FeaturePython)
  AssemblyType = Asm4EE
  AttachedBy = Origin
  AttachedTo = Micro_Cage_bottom_Body#Bottom_Cage_LCS
  AttachmentOffset = pos=(0,0,-0.7) rot=(1,0,0;3.14159rad)
  Placement = pos=(-12.7,33.1,9) rot=(-1,0,0;1.5708rad)
  diameter = 4
  invert = false
  length = 10
  lengthCustom = 40
  matchOuter = false
  offset = 0
  thread = true
  type = 27
  expr: Placement = Micro_Cage_bottom_Body.Placement * MicroManipulator_Rail_bottom#Bottom_Cage_LCS.Placement * AttachmentOffset
FEATURE [Part::FeaturePython] Washer004  label="M3-Washer017"  # Fasteners workbench fastener (typed FeaturePython)
  AssemblyType = Asm4EE
  AttachedBy = Origin
  AttachedTo = Micro_Cage_bottom_Body#Bottom_Cage_LCS
  AttachmentOffset = pos=(0,0,0) rot=(1,0,0;3.14159rad)
  Placement = pos=(-12.7,32.4,9) rot=(-1,0,0;1.5708rad)
  diameter = 4
  invert = false
  matchOuter = false
  offset = 0
  type = 3
  expr: Placement = Micro_Cage_bottom_Body.Placement * MicroManipulator_Rail_bottom#Bottom_Cage_LCS.Placement * AttachmentOffset
FEATURE [Part::FeaturePython] Washer005  label="M3-Washer018"  # Fasteners workbench fastener (typed FeaturePython)
  AssemblyType = Asm4EE
  AttachedBy = Origin
  AttachedTo = Micro_Cage_bottom_Body#Bottom_Cage_LCS
  AttachmentOffset = pos=(0,0,2) rot=(0,0,1;0rad)
  Placement = pos=(-12.7,30.4,9) rot=(1,0,0;1.5708rad)
  diameter = 4
  invert = false
  matchOuter = false
  offset = 0
  type = 3
  expr: Placement = Micro_Cage_bottom_Body.Placement * MicroManipulator_Rail_bottom#Bottom_Cage_LCS.Placement * AttachmentOffset
FEATURE [Part::FeaturePython] Nut008  label="M3-Nut031"  # Fasteners workbench fastener (typed FeaturePython)
  AssemblyType = Asm4EE
  AttachedBy = Origin
  AttachedTo = Micro_Cage_bottom_Body#Bottom_Cage_LCS
  AttachmentOffset = pos=(0,0,2.7) rot=(0,0,1;0rad)
  Placement = pos=(-12.7,29.7,9) rot=(1,0,0;1.5708rad)
  diameter = 4
  invert = false
  matchOuter = false
  offset = 0
  thread = false
  type = 7
  expr: Placement = Micro_Cage_bottom_Body.Placement * MicroManipulator_Rail_bottom#Bottom_Cage_LCS.Placement * AttachmentOffset
FEATURE [App::Part] Model  label="Assembled Manipulator"
  Configuration = 0
  Group = -> [LCS_Origin,Constraints,Variables,Micro_Cage_bottom,Micro_Cage_bottom001,Micro_Cage_bottom_Body,CenterSliderCombined_CenterSlider,CenterCage,CageTop,SliderTop,TetherArm,MicroManipulator_Arm_tilted_Arena_Arm_tilted_Arena,Luer_Tether_Part,Washer,Screw002,Nut002,Nut,Nut001,Screw003,Screw004,Screw005,Screw006,Screw007,Nut003,Nut004,Nut005,Nut006,Screw008,Washer002,Washer003,Nut007,Washer001,Screw009,+3 more]
  Origin = -> Origin
  Type = Assembly4 Model
---- part ../Lamp_LED_5mm/Lamp_post.FCStd = doc fcstd_83ec7c9602ad ----
FCSTD DOCUMENT  (FreeCAD 0.19R24344 (Git))
Label: Lamp_post
Comment: Lamp post to be used with a 5mm LED lamp shade. The foot can be plugged into a 1/4" breadboard.
License: Creative Commons Attribution-NonCommercial-ShareAlike
LicenseURL: http://creativecommons.org/licenses/by-nc-sa/4.0/
objects: Sketcher::SketchObject×7, PartDesign::Pad×4, PartDesign::Pocket×3, PartDesign::CoordinateSystem×3, PartDesign::Fillet×1, PartDesign::Plane×1, PartDesign::Body×1, App::Part×1
note: 28 computed .brp shape members not serialized (recipe doc carries the construction recipe); baked Part::Feature solids carry a one-line shape summary decoded from their .brp

FEATURE [Sketcher::SketchObject] Sketch
  FullyConstrained = true
  MapMode = 5
  Support = -> [XY_Plane]
  sketch-geometry (9):
    g0: LineSegment StartX=-2.5 StartY=0 StartZ=0 EndX=2.5 EndY=0 EndZ=0
    g1: LineSegment StartX=2.5 StartY=0 StartZ=0 EndX=2.5 EndY=-2.5 EndZ=0
    g2: LineSegment StartX=-2.5 StartY=-2.5 StartZ=0 EndX=-2.5 EndY=0 EndZ=0
    g3: ArcOfCircle CenterX=1e-16 CenterY=-2.5 CenterZ=0 NormalX=0 NormalY=0 NormalZ=1 AngleXU=0 Radius=2.5 StartAngle=3.14159 EndAngle=4.71239
    g4: ArcOfCircle CenterX=1e-16 CenterY=-2.5 CenterZ=0 NormalX=0 NormalY=0 NormalZ=1 AngleXU=0 Radius=2.5 StartAngle=4.71239 EndAngle=6.28319
    g5: ArcOfCircle CenterX=1e-16 CenterY=-2.5 CenterZ=0 NormalX=0 NormalY=0 NormalZ=1 AngleXU=0 Radius=1.5 StartAngle=3.14159 EndAngle=6.28319
    g6: LineSegment StartX=-1.5 StartY=-2.5 StartZ=0 EndX=-1.5 EndY=-1 EndZ=0
    g7: LineSegment StartX=-1.5 StartY=-1 StartZ=0 EndX=1.5 EndY=-1 EndZ=0
    g8: LineSegment StartX=1.5 StartY=-1 StartZ=0 EndX=1.5 EndY=-2.5 EndZ=0
  constraints (25):
    c: Equal(g4,g3)
    c: Tangent(g4,g1) = 1.5708
    c: Tangent(g2,g3) = 1.5708
    c: Vertical(g1)
    c: Vertical(g2)
    c: Coincident(g2,g0)
    c: Coincident(g0,g1)
    c: Symmetric(g0,g0,g-2)
    c: Tangent(g4,g3) = -1.5708
    c: PointOnObject(g3,g-2)
    c: PointOnObject(g0,g-1)
    c: Distance(g0) = 5
    c: DistanceY(g3,g-1) = 5
    c: Coincident(g5,g3)
    c: Coincident(g6,g5)
    c: Vertical(g6)
    c: Coincident(g7,g6)
    c: Horizontal(g7)
    c: Coincident(g8,g7)
    c: Coincident(g8,g5)
    c: Vertical(g8)
    c: DistanceX(g0,g6) = 1
    c: DistanceY(g6,g0) = 1
    c: Angle(g5) = 3.14159
    c: Horizontal(g5,g1)
FEATURE [PartDesign::Pad] Pad
  Direction = (1,1,1)
  Length = 73.5
  Length2 = 100
  Profile = -> Sketch
  Type = 0
FEATURE [Sketcher::SketchObject] Sketch001
  FullyConstrained = true
  MapMode = 5
  Placement = pos=(0,0,0) rot=(1,0,0;3.14159rad)
  Support = -> [Pad]
  sketch-geometry (4):
    g0: LineSegment StartX=-4 StartY=0 StartZ=0 EndX=4 EndY=0 EndZ=0
    g1: LineSegment StartX=4 StartY=0 StartZ=0 EndX=4 EndY=8 EndZ=0
    g2: LineSegment StartX=4 StartY=8 StartZ=0 EndX=-4 EndY=8 EndZ=0
    g3: LineSegment StartX=-4 StartY=8 StartZ=0 EndX=-4 EndY=0 EndZ=0
  constraints (11):
    c: Coincident(g0,g1)
    c: Coincident(g1,g2)
    c: Coincident(g2,g3)
    c: Coincident(g3,g0)
    c: Horizontal(g2)
    c: Vertical(g1)
    c: Vertical(g3)
    c: PointOnObject(g0,g-1)
    c: Distance(g0) = 8
    c: Distance(g1) = 8
    c: Symmetric(g0,g0,g-2)
FEATURE [PartDesign::Pad] Pad001
  BaseFeature = -> Pad
  Direction = (1,1,1)
  Length = 2
  Length2 = 100
  Profile = -> Sketch001
  Type = 0
FEATURE [Sketcher::SketchObject] Sketch002
  ExternalGeometry = -> [Pad]
  FullyConstrained = true
  MapMode = 5
  Placement = pos=(0,0,0) rot=(1,0,0;3.14159rad)
  Support = -> [Pad]
  sketch-geometry (2):
    g0: Circle CenterX=0 CenterY=3.15 CenterZ=0 NormalX=0 NormalY=0 NormalZ=1 AngleXU=0 Radius=3.15
    g1: Circle CenterX=0 CenterY=3.15 CenterZ=0 NormalX=0 NormalY=0 NormalZ=1 AngleXU=0 Radius=1.85
  constraints (5):
    c: Diameter(g0) = 6.3
    c: Coincident(g1,g0)
    c: PointOnObject(g-4,g1)
    c: PointOnObject(g-1,g0)
    c: PointOnObject(g0,g-2)
FEATURE [PartDesign::Pad] Pad002
  BaseFeature = -> Pad001
  Direction = (1,1,1)
  Length = 12
  Length2 = 100
  Profile = -> Sketch002
  Type = 0
FEATURE [Sketcher::SketchObject] Sketch003
  FullyConstrained = true
  MapMode = 5
  Placement = pos=(0,0,-12) rot=(1,0,0;3.14159rad)
  Support = -> [Pad002]
  sketch-geometry (8):
    g0: LineSegment StartX=-0.5 StartY=7 StartZ=0 EndX=0.5 EndY=7 EndZ=0
    g1: LineSegment StartX=0.5 StartY=7 StartZ=0 EndX=0.5 EndY=0 EndZ=0
    g2: LineSegment StartX=0.5 StartY=0 StartZ=0 EndX=-0.5 EndY=0 EndZ=0
    g3: LineSegment StartX=-0.5 StartY=0 StartZ=0 EndX=-0.5 EndY=7 EndZ=0
    g4: LineSegment StartX=-3.5 StartY=3.54 StartZ=0 EndX=3.5 EndY=3.54 EndZ=0
    g5: LineSegment StartX=3.5 StartY=3.54 StartZ=0 EndX=3.5 EndY=2.54 EndZ=0
    g6: LineSegment StartX=3.5 StartY=2.54 StartZ=0 EndX=-3.5 EndY=2.54 EndZ=0
    g7: LineSegment StartX=-3.5 StartY=2.54 StartZ=0 EndX=-3.5 EndY=3.54 EndZ=0
  constraints (22):
    c: Coincident(g0,g1)
    c: Coincident(g1,g2)
    c: Coincident(g2,g3)
    c: Coincident(g3,g0)
    c: Horizontal(g2)
    c: Vertical(g1)
    c: Vertical(g3)
    c: PointOnObject(g1,g-1)
    c: Symmetric(g0,g0,g-2)
    c: Distance(g3) = 7
    c: Distance(g0) = 1
    c: Coincident(g4,g5)
    c: Coincident(g5,g6)
    c: Coincident(g6,g7)
    c: Coincident(g7,g4)
    c: Horizontal(g6)
    c: Vertical(g5)
    c: Vertical(g7)
    c: Distance(g4) = 7
    c: Symmetric(g4,g4,g-2)
    c: DistanceY(g-1,g5) = 2.54
    c: Distance(g5) = 1
FEATURE [PartDesign::Pocket] Pocket
  BaseFeature = -> Pad002
  Length = 10
  Length2 = 100
  Profile = -> Sketch003
  Type = 0
FEATURE [Sketcher::SketchObject] Sketch004
  ExternalGeometry = -> [Pocket]
  FullyConstrained = true
  MapMode = 5
  Placement = pos=(0,0,73.5) rot=(0,0,1;0rad)
  Support = -> [Pocket]
  sketch-geometry (8):
    g0: LineSegment StartX=-3 StartY=0 StartZ=0 EndX=-1 EndY=0 EndZ=0
    g1: LineSegment StartX=-1 StartY=0 StartZ=0 EndX=-1 EndY=-5 EndZ=0
    g2: LineSegment StartX=-1 StartY=-5 StartZ=0 EndX=-3 EndY=-5 EndZ=0
    g3: LineSegment StartX=-3 StartY=-5 StartZ=0 EndX=-3 EndY=0 EndZ=0
    g4: LineSegment StartX=3 StartY=0 StartZ=0 EndX=1 EndY=0 EndZ=0
    g5: LineSegment StartX=1 StartY=0 StartZ=0 EndX=1 EndY=-5 EndZ=0
    g6: LineSegment StartX=1 StartY=-5 StartZ=0 EndX=3 EndY=-5 EndZ=0
    g7: LineSegment StartX=3 StartY=-5 StartZ=0 EndX=3 EndY=0 EndZ=0
  constraints (23):
    c: Coincident(g0,g1)
    c: Coincident(g1,g2)
    c: Coincident(g2,g3)
    c: Coincident(g3,g0)
    c: Horizontal(g0)
    c: Horizontal(g2)
    c: Vertical(g1)
    c: Vertical(g3)
    c: Coincident(g4,g5)
    c: Coincident(g5,g6)
    c: Coincident(g6,g7)
    c: Coincident(g7,g4)
    c: Horizontal(g4)
    c: Horizontal(g6)
    c: Vertical(g5)
    c: Vertical(g7)
    c: PointOnObject(g4,g-1)
    c: Symmetric(g0,g4,g-2)
    c: DistanceX(g0,g4) = 2
    c: Distance(g2) = 2
    c: Distance(g6) = 2
    c: Horizontal(g5,g1)
    c: Distance(g3) = 5
FEATURE [PartDesign::Pad] Pad003
  BaseFeature = -> Pocket
  Direction = (1,1,1)
  Length = 10
  Length2 = 100
  Profile = -> Sketch004
  Type = 0
FEATURE [PartDesign::Fillet] Fillet
  Base = -> Pad003 [Edge101,Edge113]
  BaseFeature = -> Pad003
  Radius = 3
  SupportTransform = false
FEATURE [Sketcher::SketchObject] Sketch005
  ExternalGeometry = -> [Fillet]
  FullyConstrained = true
  MapMode = 5
  Placement = pos=(-3,0,0) rot=(0.57735,-0.57735,-0.57735;2.0944rad)
  Support = -> [Fillet]
  sketch-geometry (1):
    g0: Circle CenterX=2.5 CenterY=80.5 CenterZ=0 NormalX=0 NormalY=0 NormalZ=1 AngleXU=0 Radius=1.5
  constraints (3):
    c: Diameter(g0) = 3
    c: DistanceX(g-1,g0) = 2.5
    c: DistanceY(g0,g-3) = 3
FEATURE [PartDesign::Pocket] Pocket001
  BaseFeature = -> Fillet
  Length = 5
  Length2 = 100
  Profile = -> Sketch005
  Type = 1
FEATURE [PartDesign::Plane] DatumPlane
  AttachmentOffset = pos=(0,0,0) rot=(1,0,0;1.5708rad)
  Length = 60
  MapMode = 7
  Placement = pos=(0,-5,0) rot=(0,0.707107,-0.707107;3.14159rad)
  ResizeMode = 0
  Support = -> [Pocket001]
  Width = 60
FEATURE [Sketcher::SketchObject] Sketch006
  FullyConstrained = true
  MapMode = 5
  Placement = pos=(0,-5,0) rot=(0,0.707107,-0.707107;3.14159rad)
  Support = -> [DatumPlane]
  sketch-geometry (16):
    g0: LineSegment StartX=-1.25 StartY=-2 StartZ=0 EndX=1.25 EndY=-2 EndZ=0
    g1: LineSegment StartX=1.25 StartY=-2 StartZ=0 EndX=1.25 EndY=-18 EndZ=0
    g2: LineSegment StartX=1.25 StartY=-18 StartZ=0 EndX=-1.25 EndY=-18 EndZ=0
    g3: LineSegment StartX=-1.25 StartY=-18 StartZ=0 EndX=-1.25 EndY=-2 EndZ=0
    g4: LineSegment StartX=-1.25 StartY=-21 StartZ=0 EndX=1.25 EndY=-21 EndZ=0
    g5: LineSegment StartX=1.25 StartY=-21 StartZ=0 EndX=1.25 EndY=-37 EndZ=0
    g6: LineSegment StartX=1.25 StartY=-37 StartZ=0 EndX=-1.25 EndY=-37 EndZ=0
    g7: LineSegment StartX=-1.25 StartY=-37 StartZ=0 EndX=-1.25 EndY=-21 EndZ=0
    g8: LineSegment StartX=-1.25 StartY=-40 StartZ=0 EndX=1.25 EndY=-40 EndZ=0
    g9: LineSegment StartX=1.25 StartY=-40 StartZ=0 EndX=1.25 EndY=-56 EndZ=0
    g10: LineSegment StartX=1.25 StartY=-56 StartZ=0 EndX=-1.25 EndY=-56 EndZ=0
    g11: LineSegment StartX=-1.25 StartY=-56 StartZ=0 EndX=-1.25 EndY=-40 EndZ=0
    g12: LineSegment StartX=-1.25 StartY=-59 StartZ=0 EndX=1.25 EndY=-59 EndZ=0
    g13: LineSegment StartX=1.25 StartY=-59 StartZ=0 EndX=1.25 EndY=-75 EndZ=0
    g14: LineSegment StartX=1.25 StartY=-75 StartZ=0 EndX=-1.25 EndY=-75 EndZ=0
    g15: LineSegment StartX=-1.25 StartY=-75 StartZ=0 EndX=-1.25 EndY=-59 EndZ=0
  constraints (44):
    c: Coincident(g0,g1)
    c: Coincident(g1,g2)
    c: Coincident(g2,g3)
    c: Coincident(g3,g0)
    c: Horizontal(g0)
    c: Vertical(g1)
    c: Vertical(g3)
    c: Coincident(g4,g5)
    c: Coincident(g5,g6)
    c: Coincident(g6,g7)
    c: Coincident(g7,g4)
    c: Horizontal(g4)
    c: Vertical(g5)
    c: Vertical(g7)
    c: Coincident(g8,g9)
    c: Coincident(g9,g10)
    c: Coincident(g10,g11)
    c: Coincident(g11,g8)
    c: Horizontal(g8)
    c: Vertical(g9)
    c: Vertical(g11)
    c: Coincident(g12,g13)
    c: Coincident(g13,g14)
    c: Coincident(g14,g15)
    c: Coincident(g15,g12)
    c: Horizontal(g12)
    c: Vertical(g13)
    c: Vertical(g15)
    c: Equal(g13,g9)
    c: Equal(g9,g5)
    c: Equal(g5,g1)
    c: Distance(g1) = 16
    c: Distance(g9,g12) = 3
    c: Distance(g8,g5) = 3
    c: Distance(g1,g4) = 3
    c: Equal(g2,g6)
    c: Equal(g6,g10)
    c: Equal(g10,g14)
    c: Symmetric(g14,g13,g-2)
    c: Symmetric(g10,g9,g-2)
    c: Symmetric(g5,g6,g-2)
    c: Symmetric(g1,g2,g-2)
    c: Distance(g0) = 2.5
    c: DistanceY(g0,g-1) = 2
FEATURE [PartDesign::Pocket] Pocket002
  BaseFeature = -> Pocket001
  Length = 2
  Length2 = 100
  Profile = -> Sketch006
  Type = 0
FEATURE [PartDesign::Body] Body
  Group = -> [Sketch,Pad,Sketch001,Pad001,Sketch002,Pad002,Sketch003,Pocket,Sketch004,Pad003,Fillet,Sketch005,Pocket001,DatumPlane,Sketch006,Pocket002]
  Origin = -> Origin
  Tip = -> Pocket002
FEATURE [PartDesign::CoordinateSystem] LCS_0
  AttacherType = Attacher::AttachEngine3D
  MapMode = 2
  Support = -> [X_Axis001]
FEATURE [PartDesign::CoordinateSystem] LCS_Base
  AttacherType = Attacher::AttachEngine3D
  MapMode = 45
  Placement = pos=(1.6e-15,-3.09644,-2) rot=(0,0,1;0rad)
  Support = -> [Pocket002]
FEATURE [PartDesign::CoordinateSystem] LCS_Shade
  AttacherType = Attacher::AttachEngine3D
  MapMode = 11
  Placement = pos=(1,-2.5,80.5) rot=(0,-1,0;1.5708rad)
  Support = -> [Pocket002]
FEATURE [App::Part] LampPost  label="lamp_post"
  Group = -> [LCS_0,Body,LCS_Base,LCS_Shade]
  Origin = -> Origin001
---- part ../Lamp_LED_5mm/Lamp_post_40.FCStd = doc fcstd_b7fd943e6be9 ----
FCSTD DOCUMENT  (FreeCAD 0.19R24344 (Git))
Label: Lamp_post_40
Comment: Lamp post to be used with a 5mm LED lamp shade. The foot can be plugged into a 1/4" breadboard.
License: Creative Commons Attribution-NonCommercial-ShareAlike
LicenseURL: http://creativecommons.org/licenses/by-nc-sa/4.0/
objects: Sketcher::SketchObject×7, PartDesign::Pad×4, PartDesign::Pocket×3, PartDesign::CoordinateSystem×3, PartDesign::Fillet×1, PartDesign::Plane×1, PartDesign::Body×1, App::Part×1
note: 28 computed .brp shape members not serialized (recipe doc carries the construction recipe); baked Part::Feature solids carry a one-line shape summary decoded from their .brp

FEATURE [Sketcher::SketchObject] Sketch
  FullyConstrained = true
  MapMode = 5
  Support = -> [XY_Plane]
  sketch-geometry (9):
    g0: LineSegment StartX=-2.5 StartY=0 StartZ=0 EndX=2.5 EndY=0 EndZ=0
    g1: LineSegment StartX=2.5 StartY=0 StartZ=0 EndX=2.5 EndY=-2.5 EndZ=0
    g2: LineSegment StartX=-2.5 StartY=-2.5 StartZ=0 EndX=-2.5 EndY=0 EndZ=0
    g3: ArcOfCircle CenterX=1e-16 CenterY=-2.5 CenterZ=0 NormalX=0 NormalY=0 NormalZ=1 AngleXU=0 Radius=2.5 StartAngle=3.14159 EndAngle=4.71239
    g4: ArcOfCircle CenterX=1e-16 CenterY=-2.5 CenterZ=0 NormalX=0 NormalY=0 NormalZ=1 AngleXU=0 Radius=2.5 StartAngle=4.71239 EndAngle=6.28319
    g5: ArcOfCircle CenterX=1e-16 CenterY=-2.5 CenterZ=0 NormalX=0 NormalY=0 NormalZ=1 AngleXU=0 Radius=1.5 StartAngle=3.14159 EndAngle=6.28319
    g6: LineSegment StartX=-1.5 StartY=-2.5 StartZ=0 EndX=-1.5 EndY=-1 EndZ=0
    g7: LineSegment StartX=-1.5 StartY=-1 StartZ=0 EndX=1.5 EndY=-1 EndZ=0
    g8: LineSegment StartX=1.5 StartY=-1 StartZ=0 EndX=1.5 EndY=-2.5 EndZ=0
  constraints (25):
    c: Equal(g4,g3)
    c: Tangent(g4,g1) = 1.5708
    c: Tangent(g2,g3) = 1.5708
    c: Vertical(g1)
    c: Vertical(g2)
    c: Coincident(g2,g0)
    c: Coincident(g0,g1)
    c: Symmetric(g0,g0,g-2)
    c: Tangent(g4,g3) = -1.5708
    c: PointOnObject(g3,g-2)
    c: PointOnObject(g0,g-1)
    c: Distance(g0) = 5
    c: DistanceY(g3,g-1) = 5
    c: Coincident(g5,g3)
    c: Coincident(g6,g5)
    c: Vertical(g6)
    c: Coincident(g7,g6)
    c: Horizontal(g7)
    c: Coincident(g8,g7)
    c: Coincident(g8,g5)
    c: Vertical(g8)
    c: DistanceX(g0,g6) = 1
    c: DistanceY(g6,g0) = 1
    c: Angle(g5) = 3.14159
    c: Horizontal(g5,g1)
FEATURE [PartDesign::Pad] Pad
  Direction = (1,1,1)
  Length = 33.5
  Length2 = 100
  Profile = -> Sketch
  Type = 0
FEATURE [Sketcher::SketchObject] Sketch001
  FullyConstrained = true
  MapMode = 5
  Placement = pos=(0,0,0) rot=(1,0,0;3.14159rad)
  Support = -> [Pad]
  sketch-geometry (4):
    g0: LineSegment StartX=-4 StartY=0 StartZ=0 EndX=4 EndY=0 EndZ=0
    g1: LineSegment StartX=4 StartY=0 StartZ=0 EndX=4 EndY=8 EndZ=0
    g2: LineSegment StartX=4 StartY=8 StartZ=0 EndX=-4 EndY=8 EndZ=0
    g3: LineSegment StartX=-4 StartY=8 StartZ=0 EndX=-4 EndY=0 EndZ=0
  constraints (11):
    c: Coincident(g0,g1)
    c: Coincident(g1,g2)
    c: Coincident(g2,g3)
    c: Coincident(g3,g0)
    c: Horizontal(g2)
    c: Vertical(g1)
    c: Vertical(g3)
    c: PointOnObject(g0,g-1)
    c: Distance(g0) = 8
    c: Distance(g1) = 8
    c: Symmetric(g0,g0,g-2)
FEATURE [PartDesign::Pad] Pad001
  BaseFeature = -> Pad
  Direction = (1,1,1)
  Length = 2
  Length2 = 100
  Profile = -> Sketch001
  Type = 0
FEATURE [Sketcher::SketchObject] Sketch002
  ExternalGeometry = -> [Pad]
  FullyConstrained = true
  MapMode = 5
  Placement = pos=(0,0,0) rot=(1,0,0;3.14159rad)
  Support = -> [Pad]
  sketch-geometry (2):
    g0: Circle CenterX=0 CenterY=3.15 CenterZ=0 NormalX=0 NormalY=0 NormalZ=1 AngleXU=0 Radius=3.15
    g1: Circle CenterX=0 CenterY=3.15 CenterZ=0 NormalX=0 NormalY=0 NormalZ=1 AngleXU=0 Radius=1.85
  constraints (5):
    c: Diameter(g0) = 6.3
    c: Coincident(g1,g0)
    c: PointOnObject(g-4,g1)
    c: PointOnObject(g-1,g0)
    c: PointOnObject(g0,g-2)
FEATURE [PartDesign::Pad] Pad002
  BaseFeature = -> Pad001
  Direction = (1,1,1)
  Length = 12
  Length2 = 100
  Profile = -> Sketch002
  Type = 0
FEATURE [Sketcher::SketchObject] Sketch003
  FullyConstrained = true
  MapMode = 5
  Placement = pos=(0,0,-12) rot=(1,0,0;3.14159rad)
  Support = -> [Pad002]
  sketch-geometry (8):
    g0: LineSegment StartX=-0.5 StartY=7 StartZ=0 EndX=0.5 EndY=7 EndZ=0
    g1: LineSegment StartX=0.5 StartY=7 StartZ=0 EndX=0.5 EndY=0 EndZ=0
    g2: LineSegment StartX=0.5 StartY=0 StartZ=0 EndX=-0.5 EndY=0 EndZ=0
    g3: LineSegment StartX=-0.5 StartY=0 StartZ=0 EndX=-0.5 EndY=7 EndZ=0
    g4: LineSegment StartX=-3.5 StartY=3.54 StartZ=0 EndX=3.5 EndY=3.54 EndZ=0
    g5: LineSegment StartX=3.5 StartY=3.54 StartZ=0 EndX=3.5 EndY=2.54 EndZ=0
    g6: LineSegment StartX=3.5 StartY=2.54 StartZ=0 EndX=-3.5 EndY=2.54 EndZ=0
    g7: LineSegment StartX=-3.5 StartY=2.54 StartZ=0 EndX=-3.5 EndY=3.54 EndZ=0
  constraints (22):
    c: Coincident(g0,g1)
    c: Coincident(g1,g2)
    c: Coincident(g2,g3)
    c: Coincident(g3,g0)
    c: Horizontal(g2)
    c: Vertical(g1)
    c: Vertical(g3)
    c: PointOnObject(g1,g-1)
    c: Symmetric(g0,g0,g-2)
    c: Distance(g3) = 7
    c: Distance(g0) = 1
    c: Coincident(g4,g5)
    c: Coincident(g5,g6)
    c: Coincident(g6,g7)
    c: Coincident(g7,g4)
    c: Horizontal(g6)
    c: Vertical(g5)
    c: Vertical(g7)
    c: Distance(g4) = 7
    c: Symmetric(g4,g4,g-2)
    c: DistanceY(g-1,g5) = 2.54
    c: Distance(g5) = 1
FEATURE [PartDesign::Pocket] Pocket
  BaseFeature = -> Pad002
  Length = 10
  Length2 = 100
  Profile = -> Sketch003
  Type = 0
FEATURE [Sketcher::SketchObject] Sketch004
  ExternalGeometry = -> [Pocket]
  FullyConstrained = true
  MapMode = 5
  Placement = pos=(0,0,33.5) rot=(0,0,1;0rad)
  Support = -> [Pocket]
  sketch-geometry (8):
    g0: LineSegment StartX=-3 StartY=0 StartZ=0 EndX=-1 EndY=0 EndZ=0
    g1: LineSegment StartX=-1 StartY=0 StartZ=0 EndX=-1 EndY=-5 EndZ=0
    g2: LineSegment StartX=-1 StartY=-5 StartZ=0 EndX=-3 EndY=-5 EndZ=0
    g3: LineSegment StartX=-3 StartY=-5 StartZ=0 EndX=-3 EndY=0 EndZ=0
    g4: LineSegment StartX=3 StartY=0 StartZ=0 EndX=1 EndY=0 EndZ=0
    g5: LineSegment StartX=1 StartY=0 StartZ=0 EndX=1 EndY=-5 EndZ=0
    g6: LineSegment StartX=1 StartY=-5 StartZ=0 EndX=3 EndY=-5 EndZ=0
    g7: LineSegment StartX=3 StartY=-5 StartZ=0 EndX=3 EndY=0 EndZ=0
  constraints (23):
    c: Coincident(g0,g1)
    c: Coincident(g1,g2)
    c: Coincident(g2,g3)
    c: Coincident(g3,g0)
    c: Horizontal(g0)
    c: Horizontal(g2)
    c: Vertical(g1)
    c: Vertical(g3)
    c: Coincident(g4,g5)
    c: Coincident(g5,g6)
    c: Coincident(g6,g7)
    c: Coincident(g7,g4)
    c: Horizontal(g4)
    c: Horizontal(g6)
    c: Vertical(g5)
    c: Vertical(g7)
    c: PointOnObject(g4,g-1)
    c: Symmetric(g0,g4,g-2)
    c: DistanceX(g0,g4) = 2
    c: Distance(g2) = 2
    c: Distance(g6) = 2
    c: Horizontal(g5,g1)
    c: Distance(g3) = 5
FEATURE [PartDesign::Pad] Pad003
  BaseFeature = -> Pocket
  Direction = (1,1,1)
  Length = 10
  Length2 = 100
  Profile = -> Sketch004
  Type = 0
FEATURE [PartDesign::Fillet] Fillet
  Base = -> Pad003 [Edge101,Edge113]
  BaseFeature = -> Pad003
  Radius = 3
  SupportTransform = false
FEATURE [Sketcher::SketchObject] Sketch005
  ExternalGeometry = -> [Fillet]
  FullyConstrained = true
  MapMode = 5
  Placement = pos=(-3,0,0) rot=(0.57735,-0.57735,-0.57735;2.0944rad)
  Support = -> [Fillet]
  sketch-geometry (1):
    g0: Circle CenterX=2.5 CenterY=40.5 CenterZ=0 NormalX=0 NormalY=0 NormalZ=1 AngleXU=0 Radius=1.5
  constraints (3):
    c: Diameter(g0) = 3
    c: DistanceX(g-1,g0) = 2.5
    c: DistanceY(g0,g-3) = 3
FEATURE [PartDesign::Pocket] Pocket001
  BaseFeature = -> Fillet
  Length = 5
  Length2 = 100
  Profile = -> Sketch005
  Type = 1
FEATURE [PartDesign::Plane] DatumPlane
  AttachmentOffset = pos=(0,0,0) rot=(1,0,0;1.5708rad)
  Length = 60
  MapMode = 7
  Placement = pos=(0,-5,0) rot=(0,0.707107,-0.707107;3.14159rad)
  ResizeMode = 0
  Support = -> [Pocket001]
  Width = 60
FEATURE [Sketcher::SketchObject] Sketch006
  FullyConstrained = true
  MapMode = 5
  Placement = pos=(0,-5,0) rot=(0,0.707107,-0.707107;3.14159rad)
  Support = -> [DatumPlane]
  sketch-geometry (16):
    g0: LineSegment StartX=-1.25 StartY=-2 StartZ=0 EndX=1.25 EndY=-2 EndZ=0
    g1: LineSegment StartX=1.25 StartY=-2 StartZ=0 EndX=1.25 EndY=-18 EndZ=0
    g2: LineSegment StartX=1.25 StartY=-18 StartZ=0 EndX=-1.25 EndY=-18 EndZ=0
    g3: LineSegment StartX=-1.25 StartY=-18 StartZ=0 EndX=-1.25 EndY=-2 EndZ=0
    g4: LineSegment StartX=-1.25 StartY=-21 StartZ=0 EndX=1.25 EndY=-21 EndZ=0
    g5: LineSegment StartX=1.25 StartY=-21 StartZ=0 EndX=1.25 EndY=-37 EndZ=0
    g6: LineSegment StartX=1.25 StartY=-37 StartZ=0 EndX=-1.25 EndY=-37 EndZ=0
    g7: LineSegment StartX=-1.25 StartY=-37 StartZ=0 EndX=-1.25 EndY=-21 EndZ=0
    g8: LineSegment StartX=-1.25 StartY=-40 StartZ=0 EndX=1.25 EndY=-40 EndZ=0
    g9: LineSegment StartX=1.25 StartY=-40 StartZ=0 EndX=1.25 EndY=-56 EndZ=0
    g10: LineSegment StartX=1.25 StartY=-56 StartZ=0 EndX=-1.25 EndY=-56 EndZ=0
    g11: LineSegment StartX=-1.25 StartY=-56 StartZ=0 EndX=-1.25 EndY=-40 EndZ=0
    g12: LineSegment StartX=-1.25 StartY=-59 StartZ=0 EndX=1.25 EndY=-59 EndZ=0
    g13: LineSegment StartX=1.25 StartY=-59 StartZ=0 EndX=1.25 EndY=-75 EndZ=0
    g14: LineSegment StartX=1.25 StartY=-75 StartZ=0 EndX=-1.25 EndY=-75 EndZ=0
    g15: LineSegment StartX=-1.25 StartY=-75 StartZ=0 EndX=-1.25 EndY=-59 EndZ=0
  constraints (44):
    c: Coincident(g0,g1)
    c: Coincident(g1,g2)
    c: Coincident(g2,g3)
    c: Coincident(g3,g0)
    c: Horizontal(g0)
    c: Vertical(g1)
    c: Vertical(g3)
    c: Coincident(g4,g5)
    c: Coincident(g5,g6)
    c: Coincident(g6,g7)
    c: Coincident(g7,g4)
    c: Horizontal(g4)
    c: Vertical(g5)
    c: Vertical(g7)
    c: Coincident(g8,g9)
    c: Coincident(g9,g10)
    c: Coincident(g10,g11)
    c: Coincident(g11,g8)
    c: Horizontal(g8)
    c: Vertical(g9)
    c: Vertical(g11)
    c: Coincident(g12,g13)
    c: Coincident(g13,g14)
    c: Coincident(g14,g15)
    c: Coincident(g15,g12)
    c: Horizontal(g12)
    c: Vertical(g13)
    c: Vertical(g15)
    c: Equal(g13,g9)
    c: Equal(g9,g5)
    c: Equal(g5,g1)
    c: Distance(g1) = 16
    c: Distance(g9,g12) = 3
    c: Distance(g8,g5) = 3
    c: Distance(g1,g4) = 3
    c: Equal(g2,g6)
    c: Equal(g6,g10)
    c: Equal(g10,g14)
    c: Symmetric(g14,g13,g-2)
    c: Symmetric(g10,g9,g-2)
    c: Symmetric(g5,g6,g-2)
    c: Symmetric(g1,g2,g-2)
    c: Distance(g0) = 2.5
    c: DistanceY(g0,g-1) = 2
FEATURE [PartDesign::Pocket] Pocket002
  BaseFeature = -> Pocket001
  Length = 2
  Length2 = 100
  Profile = -> Sketch006
  Type = 0
FEATURE [PartDesign::Body] Body
  Group = -> [Sketch,Pad,Sketch001,Pad001,Sketch002,Pad002,Sketch003,Pocket,Sketch004,Pad003,Fillet,Sketch005,Pocket001,DatumPlane,Sketch006,Pocket002]
  Origin = -> Origin
  Tip = -> Pocket002
FEATURE [PartDesign::CoordinateSystem] LCS_0
  AttacherType = Attacher::AttachEngine3D
  MapMode = 2
  Support = -> [X_Axis001]
FEATURE [PartDesign::CoordinateSystem] LCS_Base
  AttacherType = Attacher::AttachEngine3D
  MapMode = 45
  Placement = pos=(1.6e-15,-3.09644,-2) rot=(0,0,1;0rad)
  Support = -> [Pocket002]
FEATURE [PartDesign::CoordinateSystem] LCS_Shade
  AttacherType = Attacher::AttachEngine3D
  MapMode = 11
  Placement = pos=(1,-2.5,40.5) rot=(-0.5,-0.707107,0.5;1.91063rad)
  Support = -> [Pocket002]
FEATURE [App::Part] LampPost  label="lamp_post_40"
  Group = -> [LCS_0,Body,LCS_Base,LCS_Shade]
  Origin = -> Origin001
---- part ../Lamp_LED_5mm/Lamp_post_60.FCStd = doc fcstd_08b38a760882 ----
FCSTD DOCUMENT  (FreeCAD 0.21R29446 (Git))
Label: Lamp_post_60
Comment: Lamp post to be used with a 5mm LED lamp shade. The foot can be plugged into a 1/4" breadboard.
License: Creative Commons Attribution-NonCommercial-ShareAlike
LicenseURL: http://creativecommons.org/licenses/by-nc-sa/4.0/
objects: Sketcher::SketchObject×7, PartDesign::Pad×4, PartDesign::Pocket×3, PartDesign::CoordinateSystem×3, PartDesign::Fillet×1, PartDesign::Plane×1, PartDesign::Body×1, App::Part×1
note: 28 computed .brp shape members not serialized (recipe doc carries the construction recipe); baked Part::Feature solids carry a one-line shape summary decoded from their .brp

FEATURE [Sketcher::SketchObject] Sketch
  FullyConstrained = true
  MapMode = 5
  Support = -> [XY_Plane]
  sketch-geometry (9):
    g0: LineSegment StartX=-2.5 StartY=0 StartZ=0 EndX=2.5 EndY=0 EndZ=0
    g1: LineSegment StartX=2.5 StartY=0 StartZ=0 EndX=2.5 EndY=-2.5 EndZ=0
    g2: LineSegment StartX=-2.5 StartY=-2.5 StartZ=0 EndX=-2.5 EndY=0 EndZ=0
    g3: ArcOfCircle CenterX=1e-16 CenterY=-2.5 CenterZ=0 NormalX=0 NormalY=0 NormalZ=1 AngleXU=0 Radius=2.5 StartAngle=3.14159 EndAngle=4.71239
    g4: ArcOfCircle CenterX=1e-16 CenterY=-2.5 CenterZ=0 NormalX=0 NormalY=0 NormalZ=1 AngleXU=0 Radius=2.5 StartAngle=4.71239 EndAngle=6.28319
    g5: ArcOfCircle CenterX=1e-16 CenterY=-2.5 CenterZ=0 NormalX=0 NormalY=0 NormalZ=1 AngleXU=0 Radius=1.5 StartAngle=3.14159 EndAngle=6.28319
    g6: LineSegment StartX=-1.5 StartY=-2.5 StartZ=0 EndX=-1.5 EndY=-1 EndZ=0
    g7: LineSegment StartX=-1.5 StartY=-1 StartZ=0 EndX=1.5 EndY=-1 EndZ=0
    g8: LineSegment StartX=1.5 StartY=-1 StartZ=0 EndX=1.5 EndY=-2.5 EndZ=0
  constraints (25):
    c: Equal(g4,g3)
    c: Tangent(g4,g1) = 1.5708
    c: Tangent(g2,g3) = 1.5708
    c: Vertical(g1)
    c: Vertical(g2)
    c: Coincident(g2,g0)
    c: Coincident(g0,g1)
    c: Symmetric(g0,g0,g-2)
    c: Tangent(g4,g3) = -1.5708
    c: PointOnObject(g3,g-2)
    c: PointOnObject(g0,g-1)
    c: Distance(g0) = 5
    c: DistanceY(g3,g-1) = 5
    c: Coincident(g5,g3)
    c: Coincident(g6,g5)
    c: Vertical(g6)
    c: Coincident(g7,g6)
    c: Horizontal(g7)
    c: Coincident(g8,g7)
    c: Coincident(g8,g5)
    c: Vertical(g8)
    c: DistanceX(g0,g6) = 1
    c: DistanceY(g6,g0) = 1
    c: Angle(g5) = 3.14159
    c: Horizontal(g5,g1)
FEATURE [PartDesign::Pad] Pad
  Direction = (1,1,1)
  Length = 53.5
  Length2 = 100
  Profile = -> Sketch
  Type = 0
FEATURE [Sketcher::SketchObject] Sketch001
  FullyConstrained = true
  MapMode = 5
  Placement = pos=(0,0,0) rot=(1,0,0;3.14159rad)
  Support = -> [Pad]
  sketch-geometry (4):
    g0: LineSegment StartX=-4 StartY=0 StartZ=0 EndX=4 EndY=0 EndZ=0
    g1: LineSegment StartX=4 StartY=0 StartZ=0 EndX=4 EndY=8 EndZ=0
    g2: LineSegment StartX=4 StartY=8 StartZ=0 EndX=-4 EndY=8 EndZ=0
    g3: LineSegment StartX=-4 StartY=8 StartZ=0 EndX=-4 EndY=0 EndZ=0
  constraints (11):
    c: Coincident(g0,g1)
    c: Coincident(g1,g2)
    c: Coincident(g2,g3)
    c: Coincident(g3,g0)
    c: Horizontal(g2)
    c: Vertical(g1)
    c: Vertical(g3)
    c: PointOnObject(g0,g-1)
    c: Distance(g0) = 8
    c: Distance(g1) = 8
    c: Symmetric(g0,g0,g-2)
FEATURE [PartDesign::Pad] Pad001
  BaseFeature = -> Pad
  Direction = (0,0,-1)
  Length = 2
  Length2 = 100
  Profile = -> Sketch001
  Type = 0
FEATURE [Sketcher::SketchObject] Sketch002
  ExternalGeometry = -> [Pad]
  FullyConstrained = true
  MapMode = 5
  Placement = pos=(0,0,0) rot=(1,0,0;3.14159rad)
  Support = -> [Pad]
  sketch-geometry (2):
    g0: Circle CenterX=0 CenterY=2.5 CenterZ=0 NormalX=0 NormalY=0 NormalZ=1 AngleXU=0 Radius=2.5
    g1: Circle CenterX=0 CenterY=2.5 CenterZ=0 NormalX=0 NormalY=0 NormalZ=1 AngleXU=0 Radius=1.75
  constraints (5):
    c: Diameter(g0) = 5
    c: Coincident(g1,g0)
    c: Diameter(g1) = 3.5
    c: PointOnObject(g0,g-2)
    c: PointOnObject(g-1,g0)
FEATURE [PartDesign::Pad] Pad002
  BaseFeature = -> Pad001
  Direction = (0,0,-1)
  Length = 12
  Length2 = 100
  Profile = -> Sketch002
  Type = 0
FEATURE [Sketcher::SketchObject] Sketch003
  FullyConstrained = true
  MapMode = 5
  Support = -> [Pad002]
  sketch-geometry (8):
    g0: LineSegment StartX=-0.5 StartY=7 StartZ=0 EndX=0.5 EndY=7 EndZ=0
    g1: LineSegment StartX=0.5 StartY=7 StartZ=0 EndX=0.5 EndY=0 EndZ=0
    g2: LineSegment StartX=0.5 StartY=0 StartZ=0 EndX=-0.5 EndY=0 EndZ=0
    g3: LineSegment StartX=-0.5 StartY=0 StartZ=0 EndX=-0.5 EndY=7 EndZ=0
    g4: LineSegment StartX=-3.5 StartY=3.54 StartZ=0 EndX=3.5 EndY=3.54 EndZ=0
    g5: LineSegment StartX=3.5 StartY=3.54 StartZ=0 EndX=3.5 EndY=2.54 EndZ=0
    g6: LineSegment StartX=3.5 StartY=2.54 StartZ=0 EndX=-3.5 EndY=2.54 EndZ=0
    g7: LineSegment StartX=-3.5 StartY=2.54 StartZ=0 EndX=-3.5 EndY=3.54 EndZ=0
  constraints (22):
    c: Coincident(g0,g1)
    c: Coincident(g1,g2)
    c: Coincident(g2,g3)
    c: Coincident(g3,g0)
    c: Horizontal(g2)
    c: Vertical(g1)
    c: Vertical(g3)
    c: PointOnObject(g1,g-1)
    c: Symmetric(g0,g0,g-2)
    c: Distance(g3) = 7
    c: Distance(g0) = 1
    c: Coincident(g4,g5)
    c: Coincident(g5,g6)
    c: Coincident(g6,g7)
    c: Coincident(g7,g4)
    c: Horizontal(g6)
    c: Vertical(g5)
    c: Vertical(g7)
    c: Distance(g4) = 7
    c: Symmetric(g4,g4,g-2)
    c: DistanceY(g-1,g5) = 2.54
    c: Distance(g5) = 1
FEATURE [PartDesign::Pocket] Pocket
  BaseFeature = -> Pad002
  Direction = (0,0,-1)
  Length = 10
  Length2 = 100
  Profile = -> Sketch003
  Type = 0
FEATURE [Sketcher::SketchObject] Sketch004
  ExternalGeometry = -> [Pocket]
  FullyConstrained = true
  MapMode = 5
  Placement = pos=(4,0,0) rot=(0.57735,0.57735,0.57735;2.0944rad)
  Support = -> [Pocket]
  sketch-geometry (8):
    g0: LineSegment StartX=-3 StartY=0 StartZ=0 EndX=-1 EndY=0 EndZ=0
    g1: LineSegment StartX=-1 StartY=0 StartZ=0 EndX=-1 EndY=-5 EndZ=0
    g2: LineSegment StartX=-1 StartY=-5 StartZ=0 EndX=-3 EndY=-5 EndZ=0
    g3: LineSegment StartX=-3 StartY=-5 StartZ=0 EndX=-3 EndY=0 EndZ=0
    g4: LineSegment StartX=3 StartY=0 StartZ=0 EndX=1 EndY=0 EndZ=0
    g5: LineSegment StartX=1 StartY=0 StartZ=0 EndX=1 EndY=-5 EndZ=0
    g6: LineSegment StartX=1 StartY=-5 StartZ=0 EndX=3 EndY=-5 EndZ=0
    g7: LineSegment StartX=3 StartY=-5 StartZ=0 EndX=3 EndY=0 EndZ=0
  constraints (23):
    c: Coincident(g0,g1)
    c: Coincident(g1,g2)
    c: Coincident(g2,g3)
    c: Coincident(g3,g0)
    c: Horizontal(g0)
    c: Horizontal(g2)
    c: Vertical(g1)
    c: Vertical(g3)
    c: Coincident(g4,g5)
    c: Coincident(g5,g6)
    c: Coincident(g6,g7)
    c: Coincident(g7,g4)
    c: Horizontal(g4)
    c: Horizontal(g6)
    c: Vertical(g5)
    c: Vertical(g7)
    c: PointOnObject(g4,g-1)
    c: Symmetric(g0,g4,g-2)
    c: DistanceX(g0,g4) = 2
    c: Distance(g2) = 2
    c: Distance(g6) = 2
    c: Horizontal(g5,g1)
    c: Distance(g3) = 5
FEATURE [PartDesign::Pad] Pad003
  BaseFeature = -> Pocket
  Direction = (1,0,0)
  Length = 10
  Length2 = 100
  Profile = -> Sketch004
  Type = 0
FEATURE [PartDesign::Fillet] Fillet
  Base = -> Pad003 [Edge101,Edge113]
  BaseFeature = -> Pad003
  Radius = 3
  SupportTransform = false
  UseAllEdges = false
FEATURE [Sketcher::SketchObject] Sketch005
  ExternalGeometry = -> [Fillet]
  FullyConstrained = true
  MapMode = 5
  Placement = pos=(-3,0,0) rot=(0.57735,-0.57735,-0.57735;2.0944rad)
  Support = -> [Fillet]
  sketch-geometry (1):
    g0: Circle CenterX=2.5 CenterY=60.5 CenterZ=0 NormalX=0 NormalY=0 NormalZ=1 AngleXU=0 Radius=1.5
  constraints (3):
    c: Diameter(g0) = 3
    c: DistanceX(g-1,g0) = 2.5
    c: DistanceY(g0,g-3) = 3
FEATURE [PartDesign::Pocket] Pocket001
  BaseFeature = -> Fillet
  Direction = (1,0,0)
  Length = 5
  Length2 = 100
  Profile = -> Sketch005
  Type = 1
FEATURE [PartDesign::Plane] DatumPlane
  AttachmentOffset = pos=(0,0,0) rot=(1,0,0;1.5708rad)
  Length = 63.3041
  MapMode = 7
  Placement = pos=(-2.5,0,0) rot=(0,0.707107,-0.707107;3.14159rad)
  ResizeMode = 0
  Support = -> [Pocket001]
  Width = 101.804
FEATURE [Sketcher::SketchObject] Sketch006
  FullyConstrained = true
  MapMode = 5
  Placement = pos=(-2.5,0,0) rot=(0,0.707107,-0.707107;3.14159rad)
  Support = -> [DatumPlane]
  sketch-geometry (16):
    g0: LineSegment StartX=-1.25 StartY=-2 StartZ=0 EndX=1.25 EndY=-2 EndZ=0
    g1: LineSegment StartX=1.25 StartY=-2 StartZ=0 EndX=1.25 EndY=-18 EndZ=0
    g2: LineSegment StartX=1.25 StartY=-18 StartZ=0 EndX=-1.25 EndY=-18 EndZ=0
    g3: LineSegment StartX=-1.25 StartY=-18 StartZ=0 EndX=-1.25 EndY=-2 EndZ=0
    g4: LineSegment StartX=-1.25 StartY=-21 StartZ=0 EndX=1.25 EndY=-21 EndZ=0
    g5: LineSegment StartX=1.25 StartY=-21 StartZ=0 EndX=1.25 EndY=-37 EndZ=0
    g6: LineSegment StartX=1.25 StartY=-37 StartZ=0 EndX=-1.25 EndY=-37 EndZ=0
    g7: LineSegment StartX=-1.25 StartY=-37 StartZ=0 EndX=-1.25 EndY=-21 EndZ=0
    g8: LineSegment StartX=-1.25 StartY=-40 StartZ=0 EndX=1.25 EndY=-40 EndZ=0
    g9: LineSegment StartX=1.25 StartY=-40 StartZ=0 EndX=1.25 EndY=-56 EndZ=0
    g10: LineSegment StartX=1.25 StartY=-56 StartZ=0 EndX=-1.25 EndY=-56 EndZ=0
    g11: LineSegment StartX=-1.25 StartY=-56 StartZ=0 EndX=-1.25 EndY=-40 EndZ=0
    g12: LineSegment StartX=-1.25 StartY=-59 StartZ=0 EndX=1.25 EndY=-59 EndZ=0
    g13: LineSegment StartX=1.25 StartY=-59 StartZ=0 EndX=1.25 EndY=-75 EndZ=0
    g14: LineSegment StartX=1.25 StartY=-75 StartZ=0 EndX=-1.25 EndY=-75 EndZ=0
    g15: LineSegment StartX=-1.25 StartY=-75 StartZ=0 EndX=-1.25 EndY=-59 EndZ=0
  constraints (44):
    c: Coincident(g0,g1)
    c: Coincident(g1,g2)
    c: Coincident(g2,g3)
    c: Coincident(g3,g0)
    c: Horizontal(g0)
    c: Vertical(g1)
    c: Vertical(g3)
    c: Coincident(g4,g5)
    c: Coincident(g5,g6)
    c: Coincident(g6,g7)
    c: Coincident(g7,g4)
    c: Horizontal(g4)
    c: Vertical(g5)
    c: Vertical(g7)
    c: Coincident(g8,g9)
    c: Coincident(g9,g10)
    c: Coincident(g10,g11)
    c: Coincident(g11,g8)
    c: Horizontal(g8)
    c: Vertical(g9)
    c: Vertical(g11)
    c: Coincident(g12,g13)
    c: Coincident(g13,g14)
    c: Coincident(g14,g15)
    c: Coincident(g15,g12)
    c: Horizontal(g12)
    c: Vertical(g13)
    c: Vertical(g15)
    c: Equal(g13,g9)
    c: Equal(g9,g5)
    c: Equal(g5,g1)
    c: Distance(g1) = 16
    c: Distance(g9,g12) = 3
    c: Distance(g8,g5) = 3
    c: Distance(g1,g4) = 3
    c: Equal(g2,g6)
    c: Equal(g6,g10)
    c: Equal(g10,g14)
    c: Symmetric(g14,g13,g-2)
    c: Symmetric(g10,g9,g-2)
    c: Symmetric(g5,g6,g-2)
    c: Symmetric(g1,g2,g-2)
    c: Distance(g0) = 2.5
    c: DistanceY(g0,g-1) = 2
FEATURE [PartDesign::Pocket] Pocket002
  BaseFeature = -> Pocket001
  Direction = (0,1,2e-16)
  Length = 2
  Length2 = 100
  Profile = -> Sketch006
  Type = 0
FEATURE [PartDesign::Body] Body
  Group = -> [Sketch,Pad,Sketch001,Pad001,Sketch002,Pad002,Sketch003,Pocket,Sketch004,Pad003,Fillet,Sketch005,Pocket001,DatumPlane,Sketch006,Pocket002]
  Origin = -> Origin
  Tip = -> Pocket002
FEATURE [PartDesign::CoordinateSystem] LCS_0
  AttacherType = Attacher::AttachEngine3D
  MapMode = 2
  Support = -> [X_Axis001]
FEATURE [PartDesign::CoordinateSystem] LCS_Base
  AttacherType = Attacher::AttachEngine3D
  MapMode = 45
  Placement = pos=(1.6e-15,-3.09644,-2) rot=(0,0,1;0rad)
  Support = -> [Pocket002]
FEATURE [PartDesign::CoordinateSystem] LCS_Shade
  AttacherType = Attacher::AttachEngine3D
  MapMode = 45
  Placement = pos=(3.12576,-3.54,-7) rot=(0,0,1;0rad)
  Support = -> [Pocket002]
FEATURE [App::Part] LampPost  label="lamp_post_60"
  Group = -> [LCS_0,Body,LCS_Base,LCS_Shade]
  Origin = -> Origin001
---- part ../Lamp_LED_5mm/Lamp_shade.FCStd = doc fcstd_7dee92e57772 ----
FCSTD DOCUMENT  (FreeCAD 0.19R24344 (Git))
Label: Lamp_shade
Comment: Shade to house a 5mm LED and shield any light dissemination outside the main cone.
License: Creative Commons Attribution-NonCommercial-ShareAlike
LicenseURL: http://creativecommons.org/licenses/by-nc-sa/4.0/
objects: PartDesign::Fillet×5, Sketcher::SketchObject×4, PartDesign::Pocket×2, PartDesign::Revolution×1, PartDesign::Pad×1, PartDesign::CoordinateSystem×1, PartDesign::Body×1
note: 24 computed .brp shape members not serialized (recipe doc carries the construction recipe); baked Part::Feature solids carry a one-line shape summary decoded from their .brp

FEATURE [Sketcher::SketchObject] Sketch
  FullyConstrained = true
  MapMode = 5
  Placement = pos=(0,0,0) rot=(1,0,0;1.5708rad)
  Support = -> [XZ_Plane]
  sketch-geometry (6):
    g0: LineSegment StartX=0 StartY=0 StartZ=0 EndX=0 EndY=2 EndZ=0
    g1: LineSegment StartX=0 StartY=2 StartZ=0 EndX=3 EndY=2 EndZ=0
    g2: LineSegment StartX=3 StartY=2 StartZ=0 EndX=5 EndY=15 EndZ=0
    g3: LineSegment StartX=5 StartY=15 StartZ=0 EndX=7 EndY=15 EndZ=0
    g4: LineSegment StartX=7 StartY=15 StartZ=0 EndX=7 EndY=0 EndZ=0
    g5: LineSegment StartX=7 StartY=0 StartZ=0 EndX=0 EndY=0 EndZ=0
  constraints (17):
    c: Coincident(g-1,g0)
    c: PointOnObject(g0,g-2)
    c: Coincident(g0,g1)
    c: Horizontal(g1)
    c: Coincident(g1,g2)
    c: Coincident(g2,g3)
    c: Horizontal(g3)
    c: Coincident(g3,g4)
    c: PointOnObject(g4,g-1)
    c: Vertical(g4)
    c: Coincident(g4,g5)
    c: Coincident(g5,g0)
    c: Distance(g1) = 3
    c: Distance(g4) = 15
    c: Distance(g5) = 7
    c: Distance(g0) = 2
    c: Distance(g3) = 2
FEATURE [PartDesign::Revolution] Revolution
  Angle = 360
  Axis = (0,2e-16,1)
  Base = (0,0,0)
  Placement = pos=(0,0,0) rot=(1,0,0;1.5708rad)
  Profile = -> Sketch
  ReferenceAxis = -> Sketch [V_Axis]
  Reversed = true
FEATURE [Sketcher::SketchObject] Sketch001
  FullyConstrained = true
  MapMode = 5
  Placement = pos=(0,0,0) rot=(1,0,0;3.14159rad)
  Support = -> [Revolution]
  sketch-geometry (4):
    g0: LineSegment StartX=-1 StartY=3.5 StartZ=0 EndX=1 EndY=3.5 EndZ=0
    g1: LineSegment StartX=1 StartY=3.5 StartZ=0 EndX=1 EndY=-3.5 EndZ=0
    g2: LineSegment StartX=1 StartY=-3.5 StartZ=0 EndX=-1 EndY=-3.5 EndZ=0
    g3: LineSegment StartX=-1 StartY=-3.5 StartZ=0 EndX=-1 EndY=3.5 EndZ=0
  constraints (10):
    c: Coincident(g0,g1)
    c: Coincident(g1,g2)
    c: Coincident(g2,g3)
    c: Coincident(g3,g0)
    c: Horizontal(g0)
    c: Vertical(g1)
    c: Distance(g0) = 2
    c: Distance(g3) = 7
    c: Symmetric(g0,g2,g-1)
    c: Symmetric(g1,g2,g-2)
FEATURE [PartDesign::Pad] Pad
  BaseFeature = -> Revolution
  Direction = (1,1,1)
  Length = 10
  Length2 = 100
  Placement = pos=(0,0,0) rot=(1,0,0;1.5708rad)
  Profile = -> Sketch001
  Type = 0
FEATURE [PartDesign::Fillet] Fillet
  Base = -> Pad [Edge9]
  BaseFeature = -> Pad
  Placement = pos=(0,0,0) rot=(1,0,0;1.5708rad)
  Radius = 1
  SupportTransform = false
FEATURE [PartDesign::Fillet] Fillet001
  Base = -> Fillet [Edge4]
  BaseFeature = -> Fillet
  Placement = pos=(0,0,0) rot=(1,0,0;1.5708rad)
  Radius = 1
  SupportTransform = false
FEATURE [PartDesign::Fillet] Fillet002
  Base = -> Fillet001 [Edge7]
  BaseFeature = -> Fillet001
  Placement = pos=(0,0,0) rot=(1,0,0;1.5708rad)
  Radius = 1
  SupportTransform = false
FEATURE [PartDesign::Fillet] Fillet003
  Base = -> Fillet002 [Edge6]
  BaseFeature = -> Fillet002
  Placement = pos=(0,0,0) rot=(1,0,0;1.5708rad)
  Radius = 1
  SupportTransform = false
FEATURE [PartDesign::Fillet] Fillet004
  Base = -> Fillet003 [Edge36,Edge32,Edge34]
  BaseFeature = -> Fillet003
  Placement = pos=(0,0,0) rot=(1,0,0;1.5708rad)
  Radius = 2
  SupportTransform = false
FEATURE [Sketcher::SketchObject] Sketch002
  FullyConstrained = false
  MapMode = 5
  Placement = pos=(-1,0,0) rot=(0.707107,0,-0.707107;3.14159rad)
  sketch-geometry (1):
    g0: Circle CenterX=6 CenterY=0 CenterZ=0 NormalX=0 NormalY=0 NormalZ=1 AngleXU=0 Radius=1.55
  constraints (2):
    c: PointOnObject(g0,g-1)
    c: Diameter(g0) = 3.1
FEATURE [PartDesign::Pocket] Pocket
  BaseFeature = -> Fillet004
  Length = 5
  Length2 = 100
  Placement = pos=(0,0,0) rot=(1,0,0;1.5708rad)
  Profile = -> Sketch002
  Type = 0
FEATURE [Sketcher::SketchObject] Sketch003
  FullyConstrained = true
  MapMode = 5
  Placement = pos=(0,0,0) rot=(1,0,0;3.14159rad)
  Support = -> [Pocket]
  sketch-geometry (8):
    g0: LineSegment StartX=-3 StartY=1 StartZ=0 EndX=-1 EndY=1 EndZ=0
    g1: LineSegment StartX=-1 StartY=1 StartZ=0 EndX=-1 EndY=-1 EndZ=0
    g2: LineSegment StartX=-1 StartY=-1 StartZ=0 EndX=-3 EndY=-1 EndZ=0
    g3: LineSegment StartX=-3 StartY=-1 StartZ=0 EndX=-3 EndY=1 EndZ=0
    g4: LineSegment StartX=1 StartY=1 StartZ=0 EndX=3 EndY=1 EndZ=0
    g5: LineSegment StartX=3 StartY=1 StartZ=0 EndX=3 EndY=-1 EndZ=0
    g6: LineSegment StartX=3 StartY=-1 StartZ=0 EndX=1 EndY=-1 EndZ=0
    g7: LineSegment StartX=1 StartY=-1 StartZ=0 EndX=1 EndY=1 EndZ=0
  constraints (21):
    c: Coincident(g0,g1)
    c: Coincident(g1,g2)
    c: Coincident(g2,g3)
    c: Coincident(g3,g0)
    c: Horizontal(g0)
    c: Horizontal(g2)
    c: Vertical(g1)
    c: Coincident(g4,g5)
    c: Coincident(g5,g6)
    c: Coincident(g6,g7)
    c: Coincident(g7,g4)
    c: Horizontal(g4)
    c: Vertical(g7)
    c: Distance(g0) = 2
    c: Distance(g3) = 2
    c: Equal(g1,g7)
    c: Equal(g0,g4)
    c: DistanceX(g1,g6) = 2
    c: Symmetric(g0,g2,g-1)
    c: Symmetric(g4,g5,g-1)
    c: Symmetric(g5,g2,g-2)
FEATURE [PartDesign::Pocket] Pocket001
  BaseFeature = -> Pocket
  Length = 5
  Length2 = 100
  Midplane = true
  Placement = pos=(0,0,0) rot=(1,0,0;1.5708rad)
  Profile = -> Sketch003
  Type = 0
FEATURE [PartDesign::CoordinateSystem] LCS_Shade
  AttacherType = Attacher::AttachEngine3D
  MapMode = 11
  Placement = pos=(1,-7e-16,-6) rot=(-0.57735,0.57735,0.57735;4.18879rad)
  Support = -> [Pocket001]
FEATURE [PartDesign::Body] Body  label="lamp_shade"
  Group = -> [Sketch,Revolution,Sketch001,Pad,Fillet,Fillet001,Fillet002,Fillet003,Fillet004,Sketch002,Pocket,Sketch003,Pocket001,LCS_Shade]
  Origin = -> Origin
  Tip = -> Pocket001
---- part ../Stand_Camera-Case/Stand_Camera-Case.FCStd = doc fcstd_833851f726c5 ----
FCSTD DOCUMENT  (FreeCAD 0.19R24344 (Git))
Label: Stand_Camera-Case
Comment: Stand for PS3 Camera Case
License: Creative Commons Attribution-NonCommercial-ShareAlike
LicenseURL: http://creativecommons.org/licenses/by-nc-sa/4.0/
objects: Sketcher::SketchObject×5, PartDesign::Fillet×5, PartDesign::Pocket×3, PartDesign::Pad×2, PartDesign::CoordinateSystem×2, PartDesign::Body×1
note: 28 computed .brp shape members not serialized (recipe doc carries the construction recipe); baked Part::Feature solids carry a one-line shape summary decoded from their .brp

FEATURE [Sketcher::SketchObject] Sketch
  FullyConstrained = true
  MapMode = 5
  Placement = pos=(0,0,0) rot=(0.57735,0.57735,0.57735;2.0944rad)
  Support = -> [YZ_Plane]
  sketch-geometry (8):
    g0: LineSegment StartX=34.3 StartY=-18 StartZ=0 EndX=34.3 EndY=-21 EndZ=0
    g1: LineSegment StartX=34.3 StartY=-21 StartZ=0 EndX=-16.5 EndY=-21 EndZ=0
    g2: LineSegment StartX=-16.5 StartY=-21 StartZ=0 EndX=-16.5 EndY=21 EndZ=0
    g3: LineSegment StartX=-16.5 StartY=21 StartZ=0 EndX=12.5 EndY=21 EndZ=0
    g4: LineSegment StartX=12.5 StartY=21 StartZ=0 EndX=12.5 EndY=18 EndZ=0
    g5: LineSegment StartX=12.5 StartY=18 StartZ=0 EndX=-12.5 EndY=18 EndZ=0
    g6: LineSegment StartX=-12.5 StartY=18 StartZ=0 EndX=-12.5 EndY=-18 EndZ=0
    g7: LineSegment StartX=-12.5 StartY=-18 StartZ=0 EndX=34.3 EndY=-18 EndZ=0
  constraints (22):
    c: Vertical(g0)
    c: Coincident(g0,g1)
    c: Horizontal(g1)
    c: Coincident(g1,g2)
    c: Vertical(g2)
    c: Coincident(g2,g3)
    c: Horizontal(g3)
    c: Coincident(g3,g4)
    c: Vertical(g4)
    c: Coincident(g4,g5)
    c: Coincident(g5,g6)
    c: Coincident(g6,g7)
    c: Coincident(g7,g0)
    c: Horizontal(g7)
    c: Distance(g0) = 3
    c: Distance(g4) = 3
    c: DistanceX(g2,g5) = 4
    c: Distance(g5) = 25
    c: Distance(g2) = 42
    c: Distance(g1) = 50.8
    c: Symmetric(g5,g6,g-1)
    c: Symmetric(g4,g5,g-2)
FEATURE [PartDesign::Pad] Pad
  Direction = (1,1,1)
  Length = 70
  Length2 = 100
  Midplane = true
  Placement = pos=(0,0,0) rot=(0.57735,0.57735,0.57735;2.0944rad)
  Profile = -> Sketch
  Type = 0
FEATURE [Sketcher::SketchObject] Sketch001
  ExternalGeometry = -> [Pad]
  FullyConstrained = true
  MapMode = 5
  Placement = pos=(-7.3e-15,-16.5,3.6e-15) rot=(-0.57735,-0.57735,0.57735;4.18879rad)
  Support = -> [Pad]
  sketch-geometry (8):
    g0: Circle CenterX=0 CenterY=33 CenterZ=0 NormalX=0 NormalY=0 NormalZ=1 AngleXU=0 Radius=16.5
    g1: Circle CenterX=0 CenterY=-33 CenterZ=0 NormalX=0 NormalY=0 NormalZ=1 AngleXU=0 Radius=16.5
    g2: ArcOfCircle CenterX=-8.5 CenterY=0 CenterZ=0 NormalX=0 NormalY=0 NormalZ=1 AngleXU=0 Radius=8 StartAngle=1.5708 EndAngle=4.71239
    g3: ArcOfCircle CenterX=8.5 CenterY=1e-16 CenterZ=0 NormalX=0 NormalY=0 NormalZ=1 AngleXU=0 Radius=8 StartAngle=4.71239 EndAngle=7.85398
    g4: LineSegment StartX=-8.5 StartY=-8 StartZ=0 EndX=8.5 EndY=-8 EndZ=0
    g5: LineSegment StartX=-8.5 StartY=8 StartZ=0 EndX=8.5 EndY=8 EndZ=0
    g6: LineSegment StartX=-16.5 StartY=2.21473e-05 StartZ=0 EndX=-16.5 EndY=10 EndZ=0
    g7: LineSegment StartX=16.5 StartY=0 StartZ=0 EndX=16.5 EndY=10 EndZ=0
  constraints (22):
    c: Diameter(g0) = 33
    c: Diameter(g1) = 33
    c: PointOnObject(g1,g-2)
    c: Tangent(g2,g5) = 1.5708
    c: Tangent(g2,g4) = -1.5708
    c: Tangent(g4,g3) = -1.5708
    c: Tangent(g5,g3) = 1.5708
    c: Horizontal(g4)
    c: PointOnObject(g2,g-1)
    c: Symmetric(g2,g3,g-2)
    c: PointOnObject(g6,g2)
    c: Vertical(g6)
    c: Tangent(g6,g2)
    c: PointOnObject(g7,g3)
    c: Vertical(g7)
    c: PointOnObject(g7,g-1)
    c: Diameter(g3) = 16
    c: DistanceX(g6,g7) = 33
    c: Distance(g-1,g1) = 33
    c: Symmetric(g0,g1,g-1)
    c: Distance(g7) = 10
    c: Distance(g6) = 10
FEATURE [PartDesign::Pocket] Pocket
  BaseFeature = -> Pad
  Length = 5
  Length2 = 100
  Placement = pos=(0,0,0) rot=(0.57735,0.57735,0.57735;2.0944rad)
  Profile = -> Sketch001
  Type = 0
FEATURE [Sketcher::SketchObject] Sketch002
  ExternalGeometry = -> [Pocket]
  FullyConstrained = true
  MapMode = 5
  Placement = pos=(5.9e-15,-9.2e-15,-21) rot=(0.707107,0.707107,0;3.14159rad)
  Support = -> [Pocket]
  sketch-geometry (13):
    g0: ArcOfCircle CenterX=-6.5 CenterY=-25.4 CenterZ=0 NormalX=0 NormalY=0 NormalZ=1 AngleXU=0 Radius=3.2 StartAngle=1.5708 EndAngle=4.71239
    g1: ArcOfCircle CenterX=26.5 CenterY=-25.4 CenterZ=0 NormalX=0 NormalY=0 NormalZ=1 AngleXU=0 Radius=3.2 StartAngle=4.71239 EndAngle=7.85398
    g2: LineSegment StartX=-6.5 StartY=-28.6 StartZ=0 EndX=26.5 EndY=-28.6 EndZ=0
    g3: LineSegment StartX=-6.5 StartY=-22.2 StartZ=0 EndX=26.5 EndY=-22.2 EndZ=0
    g4: ArcOfCircle CenterX=-6.5 CenterY=25.4 CenterZ=0 NormalX=0 NormalY=0 NormalZ=1 AngleXU=0 Radius=3.2 StartAngle=1.5708 EndAngle=4.71239
    g5: ArcOfCircle CenterX=26.5 CenterY=25.4 CenterZ=0 NormalX=0 NormalY=0 NormalZ=1 AngleXU=0 Radius=3.2 StartAngle=4.71239 EndAngle=7.85398
    g6: LineSegment StartX=-6.5 StartY=22.2 StartZ=0 EndX=26.5 EndY=22.2 EndZ=0
    g7: LineSegment StartX=-6.5 StartY=28.6 StartZ=0 EndX=26.5 EndY=28.6 EndZ=0
    g8: ArcOfCircle CenterX=-1.4982 CenterY=0 CenterZ=0 NormalX=0 NormalY=0 NormalZ=1 AngleXU=0 Radius=8.2018 StartAngle=1.79309 EndAngle=4.4901
    g9: ArcOfCircle CenterX=38.0294 CenterY=-3e-16 CenterZ=0 NormalX=0 NormalY=0 NormalZ=1 AngleXU=0 Radius=16.9162 StartAngle=4.4901 EndAngle=8.07627
    g10: LineSegment StartX=-3.3064 StartY=-8 StartZ=0 EndX=34.3 EndY=-16.5 EndZ=0
    g11: LineSegment StartX=-3.3064 StartY=8 StartZ=0 EndX=34.3 EndY=16.5 EndZ=0
    g12: LineSegment StartX=-9.7 StartY=25.4 StartZ=0 EndX=-9.7 EndY=-25.4 EndZ=0
  constraints (33):
    c: Tangent(g0,g3) = 1.5708
    c: Tangent(g0,g2) = -1.5708
    c: Tangent(g2,g1) = -1.5708
    c: Tangent(g3,g1) = 1.5708
    c: Horizontal(g2)
    c: Equal(g0,g1)
    c: Tangent(g4,g7) = 1.5708
    c: Tangent(g4,g6) = -1.5708
    c: Tangent(g6,g5) = -1.5708
    c: Tangent(g7,g5) = 1.5708
    c: Horizontal(g6)
    c: Equal(g4,g5)
    c: DistanceY(g0,g4) = 50.8
    c: Symmetric(g4,g0,g-1)
    c: Distance(g5,g5) = 6.4
    c: Distance(g1,g1) = 6.4
    c: Distance(g6) = 33
    c: Distance(g3) = 33
    c: DistanceX(g-3,g4) = 10
    c: Tangent(g8,g11) = 1.5708
    c: Tangent(g8,g10) = -1.5708
    c: Tangent(g10,g9) = -1.5708
    c: Tangent(g11,g9) = 1.5708
    c: PointOnObject(g8,g-1)
    c: Vertical(g8,g8)
    c: PointOnObject(g12,g4)
    c: PointOnObject(g12,g0)
    c: Vertical(g12)
    c: Tangent(g12,g4)
    c: Tangent(g8,g12)
    c: PointOnObject(g9,g-4)
    c: Distance(g8,g8) = 16
    c: Distance(g9,g9) = 33
FEATURE [PartDesign::Pocket] Pocket001
  BaseFeature = -> Pocket
  Length = 5
  Length2 = 100
  Placement = pos=(0,0,0) rot=(0.57735,0.57735,0.57735;2.0944rad)
  Profile = -> Sketch002
  Type = 0
FEATURE [PartDesign::Fillet] Fillet
  Base = -> Pocket001 [Edge81,Edge79,Edge7,Edge64]
  BaseFeature = -> Pocket001
  Placement = pos=(0,0,0) rot=(0.57735,0.57735,0.57735;2.0944rad)
  Radius = 1
  SupportTransform = false
FEATURE [PartDesign::Fillet] Fillet001
  Base = -> Fillet [Edge86,Edge93,Edge57,Edge5]
  BaseFeature = -> Fillet
  Placement = pos=(0,0,0) rot=(0.57735,0.57735,0.57735;2.0944rad)
  Radius = 5
  SupportTransform = false
FEATURE [Sketcher::SketchObject] Sketch003
  FullyConstrained = true
  MapMode = 5
  Placement = pos=(-5.9e-15,9.2e-15,21) rot=(0,0,-1;1.5708rad)
  Support = -> [Fillet001]
  sketch-geometry (2):
    g0: Circle CenterX=0 CenterY=20 CenterZ=0 NormalX=0 NormalY=0 NormalZ=1 AngleXU=0 Radius=2.6
    g1: Circle CenterX=0 CenterY=-20 CenterZ=0 NormalX=0 NormalY=0 NormalZ=1 AngleXU=0 Radius=2.6
  constraints (5):
    c: PointOnObject(g0,g-2)
    c: Equal(g1,g0)
    c: Diameter(g0) = 5.2
    c: Distance(g0,g1) = 40
    c: Symmetric(g0,g1,g-1)
FEATURE [PartDesign::Pocket] Pocket002
  BaseFeature = -> Fillet001
  Length = 5
  Length2 = 100
  Placement = pos=(0,0,0) rot=(0.57735,0.57735,0.57735;2.0944rad)
  Profile = -> Sketch003
  Type = 0
FEATURE [Sketcher::SketchObject] Sketch004
  ExternalGeometry = -> [Pocket002]
  FullyConstrained = true
  MapMode = 5
  Placement = pos=(-5.5e-15,-12.5,2.8e-15) rot=(0.57735,0.57735,0.57735;4.18879rad)
  Support = -> [Pocket002]
  sketch-geometry (8):
    g0: LineSegment StartX=-18 StartY=-11.119 StartZ=0 EndX=18 EndY=-11.119 EndZ=0
    g1: LineSegment StartX=18 StartY=-11.119 StartZ=0 EndX=18 EndY=-14.119 EndZ=0
    g2: LineSegment StartX=18 StartY=-14.119 StartZ=0 EndX=-18 EndY=-14.119 EndZ=0
    g3: LineSegment StartX=-18 StartY=-14.119 StartZ=0 EndX=-18 EndY=-11.119 EndZ=0
    g4: LineSegment StartX=-18 StartY=14.119 StartZ=0 EndX=18 EndY=14.119 EndZ=0
    g5: LineSegment StartX=18 StartY=14.119 StartZ=0 EndX=18 EndY=11.119 EndZ=0
    g6: LineSegment StartX=18 StartY=11.119 StartZ=0 EndX=-18 EndY=11.119 EndZ=0
    g7: LineSegment StartX=-18 StartY=11.119 StartZ=0 EndX=-18 EndY=14.119 EndZ=0
  constraints (24):
    c: Coincident(g0,g1)
    c: Coincident(g1,g2)
    c: Coincident(g2,g3)
    c: Coincident(g3,g0)
    c: Horizontal(g0)
    c: Horizontal(g2)
    c: Vertical(g1)
    c: Vertical(g3)
    c: PointOnObject(g1,g-4)
    c: Distance(g1) = 3
    c: Coincident(g4,g5)
    c: Coincident(g5,g6)
    c: Coincident(g6,g7)
    c: Coincident(g7,g4)
    c: Horizontal(g4)
    c: Horizontal(g6)
    c: Vertical(g5)
    c: Vertical(g7)
    c: PointOnObject(g5,g-4)
    c: Distance(g5) = 3
    c: DistanceY(g4,g-5) = 1.5
    c: Vertical(g4,g-5)
    c: DistanceY(g-3,g2) = 1.5
    c: Vertical(g2,g-3)
FEATURE [PartDesign::Pad] Pad001
  BaseFeature = -> Pocket002
  Direction = (1,1,1)
  Length = 19
  Length2 = 100
  Placement = pos=(0,0,0) rot=(0.57735,0.57735,0.57735;2.0944rad)
  Profile = -> Sketch004
  Type = 0
FEATURE [PartDesign::Fillet] Fillet002
  Base = -> Pad001 [Edge88,Edge101,Edge100,Edge40]
  BaseFeature = -> Pad001
  Placement = pos=(0,0,0) rot=(0.57735,0.57735,0.57735;2.0944rad)
  Radius = 2
  SupportTransform = false
FEATURE [PartDesign::Fillet] Fillet003
  Base = -> Fillet002 [Edge93,Edge64,Edge35]
  BaseFeature = -> Fillet002
  Placement = pos=(0,0,0) rot=(0.57735,0.57735,0.57735;2.0944rad)
  Radius = 2
  SupportTransform = false
FEATURE [PartDesign::Fillet] Fillet004
  Base = -> Fillet003 [Edge3,Edge37]
  BaseFeature = -> Fillet003
  Placement = pos=(0,0,0) rot=(0.57735,0.57735,0.57735;2.0944rad)
  Radius = 1
  SupportTransform = false
FEATURE [PartDesign::CoordinateSystem] LCS_Baseplate_Right
  AttacherType = Attacher::AttachEngine3D
  MapMode = 45
  Placement = pos=(25.4,-8.53718,-21) rot=(0,0,1;1.5708rad)
  Support = -> [Fillet004]
FEATURE [PartDesign::CoordinateSystem] LCS_Top_Mount
  AttacherType = Attacher::AttachEngine3D
  MapMode = 45
  Placement = pos=(-1.11e-14,-2.04274,21) rot=(0,0,1;1.5708rad)
  Support = -> [Fillet004]
FEATURE [PartDesign::Body] Body  label="Stand_Camera"
  Group = -> [Sketch,Pad,Sketch001,Pocket,Sketch002,Pocket001,Fillet,Fillet001,Sketch003,Pocket002,Sketch004,Pad001,Fillet002,Fillet003,Fillet004,LCS_Baseplate_Right,LCS_Top_Mount]
  Origin = -> Origin
  Tip = -> Fillet004
---- part ../Stand_MicroManipulator/Stand_MicroManipulator.FCStd = doc fcstd_fb022970c366 ----
FCSTD DOCUMENT  (FreeCAD 0.19R24344 (Git))
Label: Stand_MicroManipulator
License: All rights reserved
LicenseURL: http://en.wikipedia.org/wiki/All_rights_reserved
objects: Sketcher::SketchObject×3, PartDesign::Pad×3, PartDesign::CoordinateSystem×2, PartDesign::Fillet×1, PartDesign::Body×1
note: 14 computed .brp shape members not serialized (recipe doc carries the construction recipe); baked Part::Feature solids carry a one-line shape summary decoded from their .brp

FEATURE [Sketcher::SketchObject] Sketch
  FullyConstrained = true
  MapMode = 5
  Support = -> [XY_Plane]
  sketch-geometry (12):
    g0: LineSegment StartX=-12.7 StartY=19.05 StartZ=0 EndX=12.7 EndY=19.05 EndZ=0
    g1: LineSegment StartX=19.05 StartY=12.7 StartZ=0 EndX=19.05 EndY=-12.7 EndZ=0
    g2: LineSegment StartX=12.7 StartY=-19.05 StartZ=0 EndX=-12.7 EndY=-19.05 EndZ=0
    g3: LineSegment StartX=-19.05 StartY=-12.7 StartZ=0 EndX=-19.05 EndY=12.7 EndZ=0
    g4: Circle CenterX=-12.7 CenterY=12.7 CenterZ=0 NormalX=0 NormalY=0 NormalZ=1 AngleXU=0 Radius=3.2
    g5: Circle CenterX=12.7 CenterY=12.7 CenterZ=0 NormalX=0 NormalY=0 NormalZ=1 AngleXU=0 Radius=3.2
    g6: Circle CenterX=12.7 CenterY=-12.7 CenterZ=0 NormalX=0 NormalY=0 NormalZ=1 AngleXU=0 Radius=3.2
    g7: Circle CenterX=-12.7 CenterY=-12.7 CenterZ=0 NormalX=0 NormalY=0 NormalZ=1 AngleXU=0 Radius=3.2
    g8: ArcOfCircle CenterX=-12.7 CenterY=12.7 CenterZ=0 NormalX=0 NormalY=0 NormalZ=1 AngleXU=0 Radius=6.35 StartAngle=1.5708 EndAngle=3.14159
    g9: ArcOfCircle CenterX=-12.7 CenterY=-12.7 CenterZ=0 NormalX=0 NormalY=0 NormalZ=1 AngleXU=0 Radius=6.35 StartAngle=3.14159 EndAngle=4.71239
    g10: ArcOfCircle CenterX=12.7 CenterY=-12.7 CenterZ=0 NormalX=0 NormalY=0 NormalZ=1 AngleXU=0 Radius=6.35 StartAngle=4.71239 EndAngle=6.28319
    g11: ArcOfCircle CenterX=12.7 CenterY=12.7 CenterZ=0 NormalX=0 NormalY=0 NormalZ=1 AngleXU=0 Radius=6.35 StartAngle=0 EndAngle=1.5708
  constraints (26):
    c: Horizontal(g0)
    c: Horizontal(g2)
    c: Vertical(g1)
    c: Vertical(g3)
    c: Equal(g6,g7)
    c: Equal(g7,g4)
    c: Equal(g4,g5)
    c: Diameter(g4) = 6.4
    c: DistanceX(g4,g5) = 25.4
    c: DistanceY(g7,g4) = 25.4
    c: Symmetric(g4,g7,g-1)
    c: Symmetric(g4,g5,g-2)
    c: Symmetric(g6,g5,g-1)
    c: Tangent(g0,g8) = 1.5708
    c: Tangent(g3,g8) = 1.5708
    c: Tangent(g3,g9) = 1.5708
    c: Tangent(g2,g9) = 1.5708
    c: Tangent(g2,g10) = 1.5708
    c: Tangent(g1,g10) = 1.5708
    c: Tangent(g0,g11) = 1.5708
    c: Tangent(g1,g11) = 1.5708
    c: Equal(g11,g10)
    c: Coincident(g11,g5)
    c: Diameter(g11) = 12.7
    c: Coincident(g8,g4)
    c: Coincident(g9,g7)
FEATURE [PartDesign::Pad] Pad
  Direction = (1,1,1)
  Length = 3
  Length2 = 100
  Profile = -> Sketch
  Type = 0
FEATURE [Sketcher::SketchObject] Sketch001
  ExternalGeometry = -> [Pad]
  FullyConstrained = true
  MapMode = 5
  Placement = pos=(0,0,3) rot=(0,0,1;0rad)
  Support = -> [Pad]
  sketch-geometry (8):
    g0: LineSegment StartX=-7.1 StartY=19.05 StartZ=0 EndX=-4.56 EndY=19.05 EndZ=0
    g1: LineSegment StartX=-4.56 StartY=19.05 StartZ=0 EndX=-4.56 EndY=-19.05 EndZ=0
    g2: LineSegment StartX=-4.56 StartY=-19.05 StartZ=0 EndX=-7.1 EndY=-19.05 EndZ=0
    g3: LineSegment StartX=-7.1 StartY=-19.05 StartZ=0 EndX=-7.1 EndY=19.05 EndZ=0
    g4: LineSegment StartX=4.56 StartY=19.05 StartZ=0 EndX=7.1 EndY=19.05 EndZ=0
    g5: LineSegment StartX=7.1 StartY=19.05 StartZ=0 EndX=7.1 EndY=-19.05 EndZ=0
    g6: LineSegment StartX=7.1 StartY=-19.05 StartZ=0 EndX=4.56 EndY=-19.05 EndZ=0
    g7: LineSegment StartX=4.56 StartY=-19.05 StartZ=0 EndX=4.56 EndY=19.05 EndZ=0
  constraints (23):
    c: Coincident(g0,g1)
    c: Coincident(g1,g2)
    c: Coincident(g2,g3)
    c: Coincident(g3,g0)
    c: Horizontal(g0)
    c: Horizontal(g2)
    c: Vertical(g1)
    c: Vertical(g3)
    c: PointOnObject(g0,g-3)
    c: PointOnObject(g1,g-4)
    c: Coincident(g4,g5)
    c: Coincident(g5,g6)
    c: Coincident(g6,g7)
    c: Coincident(g7,g4)
    c: Horizontal(g4)
    c: Horizontal(g6)
    c: Vertical(g5)
    c: Vertical(g7)
    c: PointOnObject(g5,g-4)
    c: Distance(g0) = 2.54
    c: Distance(g4) = 2.54
    c: Symmetric(g0,g4,g-2)
    c: DistanceX(g-5,g0) = 5.6
FEATURE [PartDesign::Pad] Pad001
  BaseFeature = -> Pad
  Direction = (1,1,1)
  Length = 44
  Length2 = 100
  Profile = -> Sketch001
  Type = 0
FEATURE [Sketcher::SketchObject] Sketch002
  FullyConstrained = true
  MapMode = 5
  Placement = pos=(0,0,47) rot=(0,0,1;0rad)
  Support = -> [Pad001]
  sketch-geometry (12):
    g0: LineSegment StartX=-12.7 StartY=19.05 StartZ=0 EndX=12.7 EndY=19.05 EndZ=0
    g1: LineSegment StartX=19.05 StartY=12.7 StartZ=0 EndX=19.05 EndY=-12.7 EndZ=0
    g2: LineSegment StartX=12.7 StartY=-19.05 StartZ=0 EndX=-12.7 EndY=-19.05 EndZ=0
    g3: LineSegment StartX=-19.05 StartY=-12.7 StartZ=0 EndX=-19.05 EndY=12.7 EndZ=0
    g4: Circle CenterX=-12.7 CenterY=12.7 CenterZ=0 NormalX=0 NormalY=0 NormalZ=1 AngleXU=0 Radius=3.2
    g5: Circle CenterX=12.7 CenterY=12.7 CenterZ=0 NormalX=0 NormalY=0 NormalZ=1 AngleXU=0 Radius=3.2
    g6: Circle CenterX=12.7 CenterY=-12.7 CenterZ=0 NormalX=0 NormalY=0 NormalZ=1 AngleXU=0 Radius=3.2
    g7: Circle CenterX=-12.7 CenterY=-12.7 CenterZ=0 NormalX=0 NormalY=0 NormalZ=1 AngleXU=0 Radius=3.2
    g8: ArcOfCircle CenterX=-12.7 CenterY=12.7 CenterZ=0 NormalX=0 NormalY=0 NormalZ=1 AngleXU=0 Radius=6.35 StartAngle=1.5708 EndAngle=3.14159
    g9: ArcOfCircle CenterX=-12.7 CenterY=-12.7 CenterZ=0 NormalX=0 NormalY=0 NormalZ=1 AngleXU=0 Radius=6.35 StartAngle=3.14159 EndAngle=4.71239
    g10: ArcOfCircle CenterX=12.7 CenterY=-12.7 CenterZ=0 NormalX=0 NormalY=0 NormalZ=1 AngleXU=0 Radius=6.35 StartAngle=4.71239 EndAngle=6.28319
    g11: ArcOfCircle CenterX=12.7 CenterY=12.7 CenterZ=0 NormalX=0 NormalY=0 NormalZ=1 AngleXU=0 Radius=6.35 StartAngle=4.08e-14 EndAngle=1.5708
  constraints (25):
    c: Horizontal(g0)
    c: Horizontal(g2)
    c: Vertical(g1)
    c: DistanceX(g4,g5) = 25.4
    c: DistanceY(g7,g4) = 25.4
    c: Symmetric(g4,g7,g-1)
    c: Symmetric(g4,g5,g-2)
    c: Equal(g6,g7)
    c: Equal(g7,g4)
    c: Equal(g4,g5)
    c: Diameter(g4) = 6.4
    c: Symmetric(g5,g6,g-1)
    c: Tangent(g0,g8) = 1.5708
    c: Tangent(g3,g8) = 1.5708
    c: Tangent(g3,g9) = 1.5708
    c: Tangent(g2,g9) = 1.5708
    c: Tangent(g2,g10) = 1.5708
    c: Tangent(g1,g10) = 1.5708
    c: Tangent(g1,g11) = 1.5708
    c: Tangent(g0,g11) = 1.5708
    c: Coincident(g8,g4)
    c: Coincident(g5,g11)
    c: Coincident(g7,g9)
    c: Coincident(g6,g10)
    c: Diameter(g11) = 12.7
FEATURE [PartDesign::Pad] Pad002
  BaseFeature = -> Pad001
  Direction = (1,1,1)
  Length = 3
  Length2 = 100
  Profile = -> Sketch002
  Type = 0
FEATURE [PartDesign::Fillet] Fillet
  Base = -> Pad002 [Edge70,Edge37,Edge76,Edge69,Edge49,Edge54,Edge53,Edge12]
  BaseFeature = -> Pad002
  Radius = 3
  SupportTransform = false
FEATURE [PartDesign::CoordinateSystem] LCS_Base
  AttacherType = Attacher::AttachEngine3D
  MapMode = 11
  Placement = pos=(-12.7,-12.7,0) rot=(0,0,1;1.5708rad)
  Support = -> [Fillet]
FEATURE [PartDesign::CoordinateSystem] LCS_Top
  AttacherType = Attacher::AttachEngine3D
  MapMode = 11
  Placement = pos=(-12.7,-12.7,50) rot=(0,0,1;1.5708rad)
  Support = -> [Fillet]
FEATURE [PartDesign::Body] Body  label="Stand"
  Group = -> [Sketch,Pad,Sketch001,Pad001,Sketch002,Pad002,Fillet,LCS_Base,LCS_Top]
  Origin = -> Origin
  Tip = -> Fillet
---- part ../Stand_Treadmill_Sphere_Holder/Stand_Treadmill_Sphere_Holder.FCStd = doc fcstd_0410ced7c6b9 ----
FCSTD DOCUMENT  (FreeCAD 0.19R24291 (Git))
Label: Stand_Treadmill_Sphere_Holder
Comment: A stand for the Sphere Holder. It uses a wide footprint to allow a heating mat to be placed below the holder. The feet can be used to position the stand on a breadboard. The feet are printed separatel... (+53 chars)
License: Creative Commons Attribution-NonCommercial-ShareAlike
LicenseURL: http://creativecommons.org/licenses/by-nc-sa/4.0/
objects: Sketcher::SketchObject×5, PartDesign::Pad×4, PartDesign::CoordinateSystem×4, PartDesign::Body×2, PartDesign::ShapeBinder×1, PartDesign::Hole×1, PartDesign::Pocket×1, PartDesign::Fillet×1
note: 26 computed .brp shape members not serialized (recipe doc carries the construction recipe); baked Part::Feature solids carry a one-line shape summary decoded from their .brp

FEATURE [Sketcher::SketchObject] Sketch
  FullyConstrained = true
  MapMode = 5
  Support = -> [XY_Plane]
  sketch-geometry (10):
    g0: Circle CenterX=-25.4 CenterY=0 CenterZ=0 NormalX=0 NormalY=0 NormalZ=1 AngleXU=0 Radius=3.2
    g1: Circle CenterX=25.4 CenterY=0 CenterZ=0 NormalX=0 NormalY=0 NormalZ=1 AngleXU=0 Radius=3.2
    g2: ArcOfCircle CenterX=1.6e-15 CenterY=34.5278 CenterZ=0 NormalX=0 NormalY=0 NormalZ=1 AngleXU=0 Radius=28.3713 StartAngle=3.22886 EndAngle=6.19592
    g3: ArcOfCircle CenterX=-31.75 CenterY=31.75 CenterZ=0 NormalX=0 NormalY=0 NormalZ=1 AngleXU=0 Radius=3.5 StartAngle=0.0872665 EndAngle=3.40339
    g4: ArcOfCircle CenterX=31.75 CenterY=31.75 CenterZ=0 NormalX=0 NormalY=0 NormalZ=1 AngleXU=0 Radius=3.5 StartAngle=6.02139 EndAngle=9.33751
    g5: ArcOfCircle CenterX=150.243 CenterY=1.21e-14 CenterZ=0 NormalX=0 NormalY=0 NormalZ=1 AngleXU=0 Radius=119.173 StartAngle=2.87979 EndAngle=3.40339
    g6: ArcOfCircle CenterX=31.75 CenterY=-31.75 CenterZ=0 NormalX=0 NormalY=0 NormalZ=1 AngleXU=0 Radius=3.5 StartAngle=3.22886 EndAngle=6.54498
    g7: ArcOfCircle CenterX=8e-16 CenterY=-34.5278 CenterZ=0 NormalX=0 NormalY=0 NormalZ=1 AngleXU=0 Radius=28.3713 StartAngle=0.0872665 EndAngle=3.05433
    g8: ArcOfCircle CenterX=-31.75 CenterY=-31.75 CenterZ=0 NormalX=0 NormalY=0 NormalZ=1 AngleXU=0 Radius=3.5 StartAngle=2.87979 EndAngle=6.19592
    g9: ArcOfCircle CenterX=-150.243 CenterY=1e-16 CenterZ=0 NormalX=0 NormalY=0 NormalZ=1 AngleXU=0 Radius=119.173 StartAngle=6.02139 EndAngle=6.54498
  constraints (26):
    c: Equal(g0,g1)
    c: Diameter(g0) = 6.4
    c: DistanceX(g0,g1) = 50.8
    c: PointOnObject(g1,g-1)
    c: Symmetric(g1,g0,g-2)
    c: DistanceX(g3,g4) = 63.5
    c: Tangent(g3,g2) = 1.5708
    c: Tangent(g4,g2) = 1.5708
    c: Tangent(g5,g4) = 1.5708
    c: DistanceY(g6,g4) = 63.5
    c: Tangent(g6,g5) = 1.5708
    c: Diameter(g4) = 7
    c: Diameter(g6) = 7
    c: Diameter(g8) = 7
    c: Diameter(g3) = 7
    c: Tangent(g9,g3) = 1.5708
    c: Tangent(g8,g7) = 1.5708
    c: Tangent(g9,g8) = 1.5708
    c: Tangent(g7,g6) = 1.5708
    c: Symmetric(g6,g4,g-1)
    c: Symmetric(g4,g3,g-2)
    c: Symmetric(g8,g6,g-2)
    c: Angle(g9) = 0.523599
    c: Angle(g5) = 0.523599
    c: Angle(g7) = 2.96706
    c: Angle(g2) = 2.96706
FEATURE [PartDesign::Pad] Pad
  Direction = (1,1,1)
  Length = 3
  Length2 = 100
  Profile = -> Sketch
  Type = 0
FEATURE [Sketcher::SketchObject] Sketch001
  FullyConstrained = true
  MapMode = 5
  Placement = pos=(0,0,0) rot=(1,0,0;3.14159rad)
  sketch-geometry (4):
    g0: Circle CenterX=-31.75 CenterY=31.75 CenterZ=0 NormalX=0 NormalY=0 NormalZ=1 AngleXU=0 Radius=2
    g1: Circle CenterX=31.75 CenterY=31.75 CenterZ=0 NormalX=0 NormalY=0 NormalZ=1 AngleXU=0 Radius=2
    g2: Circle CenterX=-31.75 CenterY=-31.75 CenterZ=0 NormalX=0 NormalY=0 NormalZ=1 AngleXU=0 Radius=2
    g3: Circle CenterX=31.75 CenterY=-31.75 CenterZ=0 NormalX=0 NormalY=0 NormalZ=1 AngleXU=0 Radius=2
  constraints (9):
    c: Equal(g0,g2)
    c: Equal(g2,g3)
    c: Equal(g3,g1)
    c: Diameter(g0) = 4
    c: DistanceX(g0,g1) = 63.5
    c: Symmetric(g0,g1,g-2)
    c: Symmetric(g0,g2,g-1)
    c: DistanceY(g2,g0) = 63.5
    c: Symmetric(g2,g3,g-2)
FEATURE [PartDesign::Pad] Pad001
  BaseFeature = -> Pad
  Direction = (1,1,1)
  Length = 35.2
  Length2 = 100
  Profile = -> Sketch001
  Type = 0
FEATURE [PartDesign::ShapeBinder] CopyPad001
  Placement = pos=(0,0,-35.2) rot=(0,0,1;0rad)
  TraceSupport = false
FEATURE [Sketcher::SketchObject] Sketch002
  ExternalGeometry = -> [CopyPad001]
  FullyConstrained = true
  MapMode = 5
  Placement = pos=(0,0,-35.2) rot=(1,0,0;3.14159rad)
  Support = -> [CopyPad001]
  sketch-geometry (5):
    g0: Circle CenterX=31.75 CenterY=-31.75 CenterZ=0 NormalX=0 NormalY=0 NormalZ=1 AngleXU=0 Radius=2.05
    g1: ArcOfCircle CenterX=31.75 CenterY=-31.75 CenterZ=0 NormalX=0 NormalY=0 NormalZ=1 AngleXU=0 Radius=3.15 StartAngle=3.92699 EndAngle=7.06858
    g2: ArcOfCircle CenterX=25.4 CenterY=-25.4 CenterZ=0 NormalX=0 NormalY=0 NormalZ=1 AngleXU=0 Radius=3.15 StartAngle=0.785398 EndAngle=3.92699
    g3: LineSegment StartX=33.9774 StartY=-29.5226 StartZ=0 EndX=27.6274 EndY=-23.1726 EndZ=0
    g4: LineSegment StartX=29.5226 StartY=-33.9774 StartZ=0 EndX=23.1726 EndY=-27.6274 EndZ=0
  constraints (11):
    c: Tangent(g1,g4) = 1.5708
    c: Tangent(g1,g3) = -1.5708
    c: Tangent(g3,g2) = -1.5708
    c: Tangent(g4,g2) = 1.5708
    c: Equal(g1,g2)
    c: Coincident(g1,g0)
    c: Coincident(g0,g-3)
    c: Diameter(g0) = 4.1
    c: Diameter(g1) = 6.3
    c: DistanceX(g-1,g2) = 25.4
    c: DistanceY(g2,g-1) = 25.4
FEATURE [PartDesign::Pad] Pad002
  Direction = (1,1,1)
  Length = 3
  Length2 = 100
  Placement = pos=(0,0,-35.2) rot=(0,0,1;0rad)
  Profile = -> Sketch002
  Type = 0
FEATURE [Sketcher::SketchObject] Sketch003
  ExternalGeometry = -> [Pad002]
  FullyConstrained = true
  MapMode = 5
  Placement = pos=(0,0,-38.2) rot=(1,0,0;3.14159rad)
  Support = -> [Pad002]
  sketch-geometry (1):
    g0: Circle CenterX=25.4 CenterY=-25.4 CenterZ=0 NormalX=0 NormalY=0 NormalZ=1 AngleXU=0 Radius=3.15
  constraints (2):
    c: Coincident(g0,g-3)
    c: PointOnObject(g-3,g0)
FEATURE [PartDesign::Pad] Pad003
  BaseFeature = -> Pad002
  Direction = (1,1,1)
  Length = 12
  Length2 = 100
  Placement = pos=(0,0,-35.2) rot=(0,0,1;0rad)
  Profile = -> Sketch003
  Type = 0
FEATURE [PartDesign::Hole] Hole
  BaseFeature = -> Pad003
  Depth = 20
  DepthType = 0
  Diameter = 4
  DrillForDepth = false
  DrillPoint = 1
  DrillPointAngle = 118
  HoleCutCountersinkAngle = 90
  HoleCutCustomValues = false
  HoleCutDepth = 0
  HoleCutDiameter = 0
  HoleCutType = 0
  ModelActualThread = false
  Placement = pos=(0,0,-35.2) rot=(0,0,1;0rad)
  Profile = -> Pad003 [Face9]
  Tapered = false
  TaperedAngle = 90
  ThreadAngle = 0
  ThreadClass = 0
  ThreadCutOffInner = 0
  ThreadCutOffOuter = 0
  ThreadDirection = 0
  ThreadFit = 0
  ThreadPitch = 0
  ThreadSize = 0
  ThreadType = 0
  Threaded = false
FEATURE [Sketcher::SketchObject] Sketch004
  FullyConstrained = true
  MapMode = 5
  Placement = pos=(0,0,-50.2) rot=(1,0,0;3.14159rad)
  Support = -> [Hole]
  sketch-geometry (8):
    g0: LineSegment StartX=20 StartY=-24.9 StartZ=0 EndX=30 EndY=-24.9 EndZ=0
    g1: LineSegment StartX=30 StartY=-24.9 StartZ=0 EndX=30 EndY=-25.9 EndZ=0
    g2: LineSegment StartX=30 StartY=-25.9 StartZ=0 EndX=20 EndY=-25.9 EndZ=0
    g3: LineSegment StartX=20 StartY=-25.9 StartZ=0 EndX=20 EndY=-24.9 EndZ=0
    g4: LineSegment StartX=24.9 StartY=-20 StartZ=0 EndX=25.9 EndY=-20 EndZ=0
    g5: LineSegment StartX=25.9 StartY=-20 StartZ=0 EndX=25.9 EndY=-30 EndZ=0
    g6: LineSegment StartX=25.9 StartY=-30 StartZ=0 EndX=24.9 EndY=-30 EndZ=0
    g7: LineSegment StartX=24.9 StartY=-30 StartZ=0 EndX=24.9 EndY=-20 EndZ=0
  constraints (24):
    c: Coincident(g0,g1)
    c: Coincident(g1,g2)
    c: Coincident(g2,g3)
    c: Coincident(g3,g0)
    c: Horizontal(g0)
    c: Horizontal(g2)
    c: Vertical(g1)
    c: Vertical(g3)
    c: Coincident(g4,g5)
    c: Coincident(g5,g6)
    c: Coincident(g6,g7)
    c: Coincident(g7,g4)
    c: Horizontal(g4)
    c: Horizontal(g6)
    c: Vertical(g5)
    c: Vertical(g7)
    c: Distance(g1) = 1
    c: Distance(g4) = 1
    c: DistanceY(g0,g-1) = 24.9
    c: Distance(g0) = 10
    c: DistanceX(g-1,g0) = 20
    c: DistanceX(g-1,g4) = 24.9
    c: DistanceY(g4,g-1) = 20
    c: Distance(g7) = 10
FEATURE [PartDesign::Pocket] Pocket
  BaseFeature = -> Hole
  Length = 12
  Length2 = 100
  Placement = pos=(0,0,-35.2) rot=(0,0,1;0rad)
  Profile = -> Sketch004
  Type = 0
FEATURE [PartDesign::Fillet] Fillet
  Base = -> Pad001 [Edge19,Edge16,Edge21,Edge17]
  BaseFeature = -> Pad001
  Radius = 1
  SupportTransform = false
FEATURE [PartDesign::CoordinateSystem] LCS_Base
  AttacherType = Attacher::AttachEngine3D
  MapMode = 45
  Placement = pos=(31.75,-31.75,-35.2) rot=(0,0,1;0rad)
  Support = -> [Fillet]
FEATURE [PartDesign::CoordinateSystem] LCS_Top
  AttacherType = Attacher::AttachEngine3D
  MapMode = 45
  Placement = pos=(-25.4,1e-16,3) rot=(0,0,1;0rad)
  Support = -> [Fillet]
FEATURE [PartDesign::Body] Body  label="Stand"
  Group = -> [Sketch,Pad,Sketch001,Pad001,Fillet,LCS_Base,LCS_Top]
  Origin = -> Origin
  Tip = -> Fillet
FEATURE [PartDesign::CoordinateSystem] LCS_Foot_Base
  AttacherType = Attacher::AttachEngine3D
  AttachmentOffset = pos=(-1,0.6,0) rot=(0,0,1;0.366519rad)
  MapMode = 45
  Placement = pos=(25.3288,25.2836,-38.2) rot=(0,0,1;1.56983rad)
  Support = -> [Pocket]
FEATURE [PartDesign::CoordinateSystem] LCS_Top001
  AttacherType = Attacher::AttachEngine3D
  MapMode = 45
  Placement = pos=(31.75,31.75,-38.2) rot=(0,0,-1;1e-05rad)
  Support = -> [Pocket]
FEATURE [PartDesign::Body] Body001  label="Stand_Foot"
  Group = -> [CopyPad001,Sketch002,Pad002,Sketch003,Pad003,Hole,Sketch004,Pocket,LCS_Foot_Base,LCS_Top001]
  Origin = -> Origin001
  Tip = -> Pocket
